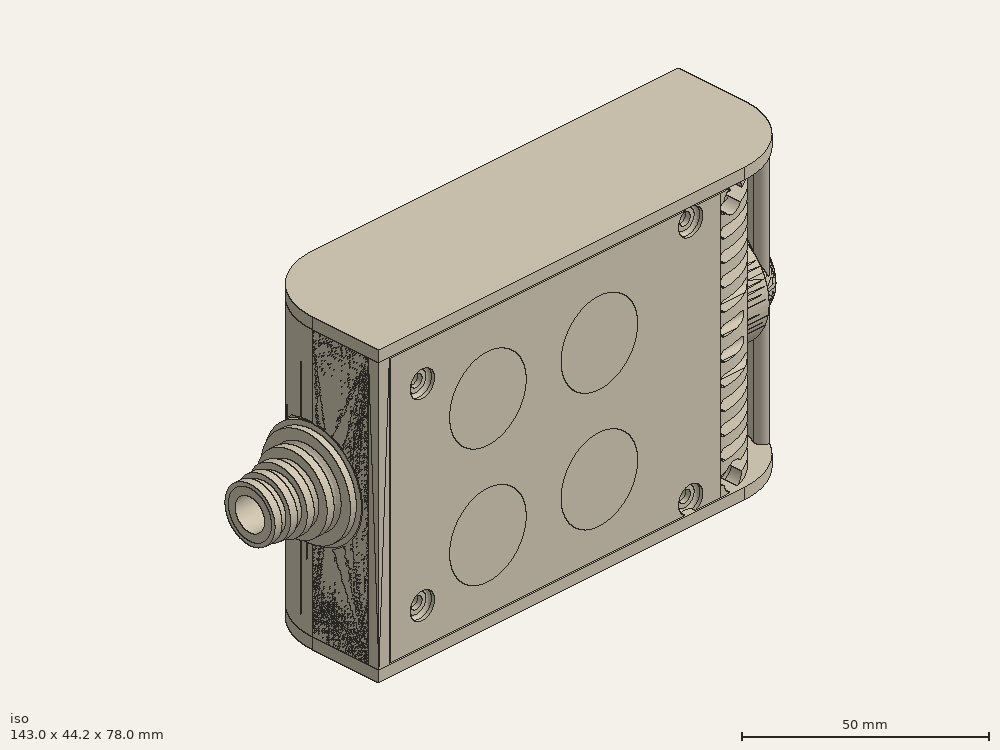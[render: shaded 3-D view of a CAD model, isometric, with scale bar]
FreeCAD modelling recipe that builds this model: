
FCSTD DOCUMENT  (FreeCAD 0.19R0.19.2)
Label: enclosure_134
License: All rights reserved
LicenseURL: http://en.wikipedia.org/wiki/All_rights_reserved
objects: Part::Feature×86, Part::Revolution×86, Part::MultiFuse×65, Sketcher::SketchObject×48, Part::Extrusion×36, Part::Cut×29, Part::Fillet×27, Part::Cylinder×24, Part::Box×17, App::MeasureDistance×4
note: 418 computed .brp shape members not serialized (recipe doc carries the construction recipe); baked Part::Feature solids carry a one-line shape summary decoded from their .brp

FEATURE [Sketcher::SketchObject] Sketch  label="topSketch"
  FullyConstrained = true
  sketch-geometry (20):
    g0: LineSegment StartX=5.21097e-06 StartY=3 StartZ=0 EndX=5.21097e-06 EndY=19 EndZ=0
    g1: ArcOfCircle CenterX=19 CenterY=19 CenterZ=0 NormalX=0 NormalY=0 NormalZ=1 AngleXU=0 Radius=19 StartAngle=1.5708 EndAngle=3.14159
    g2: ArcOfCircle CenterX=19 CenterY=19 CenterZ=0 NormalX=0 NormalY=0 NormalZ=1 AngleXU=0 Radius=16 StartAngle=1.5708 EndAngle=3.14159
    g3: LineSegment StartX=114 StartY=35 StartZ=0 EndX=19 EndY=35 EndZ=0
    g4: LineSegment StartX=5.21097e-06 StartY=3 StartZ=0 EndX=5.21097e-06 EndY=0 EndZ=0
    g5: LineSegment StartX=3 StartY=0 StartZ=0 EndX=5.21097e-06 EndY=0 EndZ=0
    g6: LineSegment StartX=3 StartY=19 StartZ=0 EndX=3 EndY=0 EndZ=0
    g7: LineSegment StartX=19 StartY=38 StartZ=0 EndX=124 EndY=38 EndZ=0
    g8: Circle CenterX=119 CenterY=35 CenterZ=0 NormalX=0 NormalY=0 NormalZ=1 AngleXU=0 Radius=1
    g9: Circle CenterX=121 CenterY=35 CenterZ=0 NormalX=0 NormalY=0 NormalZ=1 AngleXU=0 Radius=1
    g10: Circle CenterX=121 CenterY=33 CenterZ=0 NormalX=0 NormalY=0 NormalZ=1 AngleXU=0 Radius=1
    g11: BSplineCurve PolesCount=3 KnotsCount=2 Degree=2 IsPeriodic=0
    g12: GeomPoint X=119 Y=35 Z=0
    g13: GeomPoint X=121 Y=33 Z=0
    g14: LineSegment StartX=119 StartY=35 StartZ=0 EndX=114 EndY=35 EndZ=0
    g15: ArcOfCircle CenterX=105 CenterY=19 CenterZ=0 NormalX=0 NormalY=0 NormalZ=1 AngleXU=0 Radius=19 StartAngle=5.7297 EndAngle=6.28319
    g16: ArcOfCircle CenterX=105 CenterY=19 CenterZ=0 NormalX=0 NormalY=0 NormalZ=1 AngleXU=0 Radius=16 StartAngle=5.60905 EndAngle=6.28319
    g17: LineSegment StartX=121 StartY=33 StartZ=0 EndX=121 EndY=19 EndZ=0
    g18: LineSegment StartX=124 StartY=38 StartZ=0 EndX=124 EndY=19 EndZ=0
    g19: LineSegment StartX=117.5 StartY=9.01251 StartZ=0 EndX=121.163 EndY=9.0125 EndZ=0
  constraints (46):
    c: Vertical(g0)
    c: Block(g0)
    c: Coincident(g1,g0)
    c: Block(g1)
    c: Coincident(g2,g1)
    c: Block(g2)
    c: Coincident(g3,g2)
    c: Horizontal(g3)
    c: Tangent(g3,g2)
    c: Coincident(g4,g0)
    c: Distance(g4) = 3
    c: Vertical(g4)
    c: Coincident(g5,g4)
    c: Horizontal(g5)
    c: Coincident(g6,g2)
    c: Coincident(g6,g5)
    c: Vertical(g6)
    c: Horizontal(g7)
    c: Distance(g7) = 105
    c: Coincident(g7,g1)
    c: Block(g3)
    c: Weight(g8) = 1
    c: Equal(g8,g9)
    c: Equal(g8,g10)
    c: InternalAlignment(g8,g11)
    c: InternalAlignment(g9,g11)
    c: InternalAlignment(g10,g11)
    c: InternalAlignment(g12,g11)
    c: InternalAlignment(g13,g11)
    c: Block(g11)
    c: Coincident(g14,g11)
    c: Coincident(g14,g3)
    c: Horizontal(g14)
    c: Block(g15)
    c: Coincident(g16,g15)
    c: Block(g16)
    c: Coincident(g17,g11)
    c: Coincident(g17,g16)
    c: Vertical(g17)
    c: Distance(g17) = 14
    c: Coincident(g18,g7)
    c: Coincident(g18,g15)
    c: Vertical(g18)
    c: Distance(g18) = 19
    c: Coincident(g19,g16)
    c: Coincident(g19,g15)
FEATURE [Sketcher::SketchObject] Sketch001  label="bottomSketch"
  FullyConstrained = true
  sketch-geometry (32):
    g0: LineSegment StartX=3.3 StartY=-6.03275e-07 StartZ=0 EndX=98 EndY=-6.03275e-07 EndZ=0
    g1: ArcOfCircle CenterX=98 CenterY=19 CenterZ=0 NormalX=0 NormalY=0 NormalZ=1 AngleXU=0 Radius=19 StartAngle=4.71239 EndAngle=5.71103
    g2: LineSegment StartX=6.3 StartY=8 StartZ=0 EndX=3.3 EndY=8 EndZ=0
    g3: LineSegment StartX=3.3 StartY=8 StartZ=0 EndX=3.3 EndY=-6.03275e-07 EndZ=0
    g4: ArcOfCircle CenterX=8.3 CenterY=5 CenterZ=0 NormalX=0 NormalY=0 NormalZ=1 AngleXU=0 Radius=2 StartAngle=3.14159 EndAngle=4.71239
    g5: LineSegment StartX=6.3 StartY=8 StartZ=0 EndX=6.3 EndY=5 EndZ=0
    g6: ArcOfCircle CenterX=98 CenterY=19 CenterZ=0 NormalX=0 NormalY=0 NormalZ=1 AngleXU=0 Radius=12.7 StartAngle=4.71239 EndAngle=6.28319
    g7: LineSegment StartX=94.7 StartY=3 StartZ=0 EndX=8.3 EndY=3 EndZ=0
    g8-g12: Circle x5 (B-spline internal-alignment scaffolding for g13; pole/knot coordinates omitted)
    g13: BSplineCurve PolesCount=5 KnotsCount=3 Degree=3 IsPeriodic=0
    g14: GeomPoint X=98 Y=6.3 Z=0
    g15: GeomPoint X=96.3938 Y=4.71946 Z=0
    g16: GeomPoint X=94.7 Y=3 Z=0
    g17-g23: Circle x7 (B-spline internal-alignment scaffolding for g24; pole/knot coordinates omitted)
    g24: BSplineCurve PolesCount=7 KnotsCount=5 Degree=3 IsPeriodic=0
    g25-g29: GeomPoint x5 (B-spline internal-alignment scaffolding for g24; pole/knot coordinates omitted)
    g30: ArcOfCircle CenterX=98 CenterY=19 CenterZ=0 NormalX=0 NormalY=0 NormalZ=1 AngleXU=0 Radius=15.7 StartAngle=5.81226 EndAngle=6.28319
    g31: LineSegment StartX=110.7 StartY=19 StartZ=0 EndX=113.7 EndY=19 EndZ=0
  constraints (41):
    c: Horizontal(g0)
    c: Coincident(g1,g0)
    c: Block(g1)
    c: Horizontal(g2)
    c: Distance(g2) = 3
    c: Coincident(g3,g2)
    c: Vertical(g3)
    c: Coincident(g3,g0)
    c: Block(g4)
    c: Block(g2)
    c: Coincident(g5,g2)
    c: Coincident(g5,g4)
    c: Vertical(g5)
    c: Coincident(g6,g1)
    c: Block(g6)
    c: Coincident(g7,g4)
    c: Horizontal(g7)
    c: Block(g0)
    c: Block(g7)
    c: Block(g3)
    c: Coincident(g13,g6)
    c: Weight(g8) = 1
    c: Equal(g8, g9-g12) x4
    c: Coincident(g13,g7)
    c: InternalAlignment(g8-g12 -> g13) x5
    c: InternalAlignment(g14,g13)
    c: InternalAlignment(g15,g13)
    c: InternalAlignment(g16,g13)
    c: Block(g13)
    c: Weight(g17) = 1
    c: Equal(g17, g18-g23) x6
    c: Coincident(g24,g1)
    c: InternalAlignment(g17-g23 -> g24) x7
    c: InternalAlignment(g25-g29 -> g24) x5
    c: Block(g24)
    c: Coincident(g30,g24)
    c: Coincident(g31,g6)
    c: Coincident(g31,g30)
    c: Horizontal(g31)
    c: Block(g31)
    c: Block(g30)
FEATURE [Part::Extrusion] Extrude  label="top"
  Base = -> Sketch
  Dir = (0,0,1)
  DirMode = 2
  FaceMakerClass = Part::FaceMakerBullseye
  LengthFwd = 72
  LengthRev = 0
  Solid = true
  Symmetric = false
FEATURE [Part::Extrusion] Extrude001  label="bottom"
  Base = -> Sketch001
  Dir = (0,0,1)
  DirMode = 2
  FaceMakerClass = Part::FaceMakerBullseye
  LengthFwd = 71.4
  LengthRev = 0
  Placement = pos=(0,0,0.3) rot=(0,0,1;0rad)
  Solid = true
  Symmetric = false
FEATURE [Sketcher::SketchObject] Sketch002  label="topSketch001"
  FullyConstrained = true
  sketch-geometry (6):
    g0: ArcOfCircle CenterX=19 CenterY=19 CenterZ=0 NormalX=0 NormalY=0 NormalZ=1 AngleXU=0 Radius=19 StartAngle=1.5708 EndAngle=3.14159
    g1: LineSegment StartX=5.22862e-06 StartY=19 StartZ=0 EndX=5.22862e-06 EndY=1.19904e-11 EndZ=0
    g2: LineSegment StartX=19 StartY=38 StartZ=0 EndX=124 EndY=38 EndZ=0
    g3: LineSegment StartX=5.22862e-06 StartY=1.19904e-11 StartZ=0 EndX=105 EndY=1.19904e-11 EndZ=0
    g4: ArcOfCircle CenterX=105 CenterY=19 CenterZ=0 NormalX=0 NormalY=0 NormalZ=1 AngleXU=0 Radius=19 StartAngle=4.71239 EndAngle=6.28319
    g5: LineSegment StartX=124 StartY=38 StartZ=0 EndX=124 EndY=19 EndZ=0
  constraints (16):
    c: Block(g0)
    c: Coincident(g1,g0)
    c: Vertical(g1)
    c: Horizontal(g2)
    c: Distance(g2) = 105
    c: Coincident(g2,g0)
    c: Distance(g1) = 19
    c: Coincident(g3,g1)
    c: Horizontal(g3)
    c: Distance(g3) = 105
    c: Block(g4)
    c: Coincident(g4,g3)
    c: Coincident(g5,g2)
    c: Coincident(g5,g4)
    c: Vertical(g5)
    c: Distance(g5) = 19
FEATURE [Part::Extrusion] Extrude002  label="sideA"
  Base = -> Sketch002
  Dir = (0,0,1)
  DirMode = 2
  FaceMakerClass = Part::FaceMakerBullseye
  LengthFwd = 3
  LengthRev = 0
  Placement = pos=(0,0,-3) rot=(0,0,1;0rad)
  Solid = true
  Symmetric = false
FEATURE [Sketcher::SketchObject] Sketch003  label="topSketch002"
  FullyConstrained = true
  sketch-geometry (6):
    g0: LineSegment StartX=19 StartY=38 StartZ=0 EndX=117 EndY=38 EndZ=0
    g1: ArcOfCircle CenterX=19 CenterY=19 CenterZ=0 NormalX=0 NormalY=0 NormalZ=1 AngleXU=0 Radius=19 StartAngle=1.5708 EndAngle=3.14159
    g2: LineSegment StartX=117 StartY=38 StartZ=0 EndX=117 EndY=19 EndZ=0
    g3: LineSegment StartX=98 StartY=1.0161e-12 StartZ=0 EndX=5.22862e-06 EndY=1.0161e-12 EndZ=0
    g4: LineSegment StartX=5.22862e-06 StartY=19 StartZ=0 EndX=5.22862e-06 EndY=1.0161e-12 EndZ=0
    g5: ArcOfCircle CenterX=98 CenterY=19 CenterZ=0 NormalX=0 NormalY=0 NormalZ=1 AngleXU=0 Radius=19 StartAngle=4.71239 EndAngle=6.28319
  constraints (16):
    c: Horizontal(g0)
    c: Distance(g0) = 98
    c: Coincident(g1,g0)
    c: Block(g1)
    c: Coincident(g2,g0)
    c: Vertical(g2)
    c: Distance(g2) = 19
    c: Horizontal(g3)
    c: Coincident(g4,g1)
    c: Vertical(g4)
    c: Coincident(g3,g4)
    c: Block(g3)
    c: Coincident(g5,g2)
    c: Coincident(g5,g3)
    c: Block(g0)
    c: Block(g5)
FEATURE [Sketcher::SketchObject] Sketch004
  FullyConstrained = true
  MapMode = 3
  Placement = pos=(0,0,0) rot=(1,0,0;1.5708rad)
  Support = -> [Extrude]
  sketch-geometry (8):
    g0: Circle CenterX=80.351 CenterY=-67.6202 CenterZ=0 NormalX=0 NormalY=0 NormalZ=1 AngleXU=0 Radius=2
    g1: Circle CenterX=80.351 CenterY=-67.6202 CenterZ=0 NormalX=0 NormalY=0 NormalZ=1 AngleXU=0 Radius=3
    g2: Circle CenterX=80.351 CenterY=-4.92017 CenterZ=0 NormalX=0 NormalY=0 NormalZ=1 AngleXU=0 Radius=2
    g3: Circle CenterX=80.351 CenterY=-4.92017 CenterZ=0 NormalX=0 NormalY=0 NormalZ=1 AngleXU=0 Radius=3
    g4: Circle CenterX=23.851 CenterY=-4.92017 CenterZ=0 NormalX=0 NormalY=0 NormalZ=1 AngleXU=0 Radius=2
    g5: Circle CenterX=23.851 CenterY=-4.92017 CenterZ=0 NormalX=0 NormalY=0 NormalZ=1 AngleXU=0 Radius=3
    g6: Circle CenterX=23.851 CenterY=-67.6202 CenterZ=0 NormalX=0 NormalY=0 NormalZ=1 AngleXU=0 Radius=2
    g7: Circle CenterX=23.851 CenterY=-67.6202 CenterZ=0 NormalX=0 NormalY=0 NormalZ=1 AngleXU=0 Radius=3
  constraints (8):
    c: Block(g3)
    c: Block(g2)
    c: Block(g1)
    c: Block(g0)
    c: Block(g6)
    c: Block(g7)
    c: Block(g4)
    c: Block(g5)
FEATURE [Part::Extrusion] Extrude004
  Base = -> Sketch004
  Dir = (0,-1,2e-16)
  DirMode = 2
  FaceMakerClass = Part::FaceMakerBullseye
  LengthFwd = 6
  LengthRev = 0
  Placement = pos=(0,9,0) rot=(0,0,1;0rad)
  Solid = true
  Symmetric = false
FEATURE [Sketcher::SketchObject] Sketch005
  FullyConstrained = true
  MapMode = 3
  Placement = pos=(0,0,0) rot=(1,0,0;1.5708rad)
  Support = -> [Extrude]
  sketch-geometry (8):
    g0: Circle CenterX=80.351 CenterY=-67.6202 CenterZ=0 NormalX=0 NormalY=0 NormalZ=1 AngleXU=0 Radius=3
    g1: Circle CenterX=80.351 CenterY=-4.92017 CenterZ=0 NormalX=0 NormalY=0 NormalZ=1 AngleXU=0 Radius=3
    g2: Circle CenterX=23.851 CenterY=-4.92017 CenterZ=0 NormalX=0 NormalY=0 NormalZ=1 AngleXU=0 Radius=3
    g3: Circle CenterX=23.851 CenterY=-67.6202 CenterZ=0 NormalX=0 NormalY=0 NormalZ=1 AngleXU=0 Radius=3
    g4: Circle CenterX=23.851 CenterY=-67.6202 CenterZ=0 NormalX=0 NormalY=0 NormalZ=1 AngleXU=0 Radius=5
    g5: Circle CenterX=80.351 CenterY=-67.6202 CenterZ=0 NormalX=0 NormalY=0 NormalZ=1 AngleXU=0 Radius=5
    g6: Circle CenterX=23.851 CenterY=-4.92017 CenterZ=0 NormalX=0 NormalY=0 NormalZ=1 AngleXU=0 Radius=5
    g7: Circle CenterX=80.351 CenterY=-4.92017 CenterZ=0 NormalX=0 NormalY=0 NormalZ=1 AngleXU=0 Radius=5
  constraints (8):
    c: Block(g1)
    c: Block(g0)
    c: Block(g3)
    c: Block(g2)
    c: Block(g5)
    c: Block(g4)
    c: Block(g6)
    c: Block(g7)
FEATURE [Part::Extrusion] Extrude005
  Base = -> Sketch005
  Dir = (0,-1,2e-16)
  DirMode = 2
  FaceMakerClass = Part::FaceMakerBullseye
  LengthFwd = 2
  LengthRev = 0
  Solid = true
  Symmetric = false
FEATURE [Sketcher::SketchObject] Sketch006
  FullyConstrained = true
  MapMode = 3
  Placement = pos=(0,0,0) rot=(1,0,0;1.5708rad)
  sketch-geometry (8):
    g0: Circle CenterX=80.351 CenterY=-67.6202 CenterZ=0 NormalX=0 NormalY=0 NormalZ=1 AngleXU=0 Radius=3
    g1: Circle CenterX=80.351 CenterY=-4.92017 CenterZ=0 NormalX=0 NormalY=0 NormalZ=1 AngleXU=0 Radius=3
    g2: Circle CenterX=23.851 CenterY=-4.92017 CenterZ=0 NormalX=0 NormalY=0 NormalZ=1 AngleXU=0 Radius=3
    g3: Circle CenterX=23.851 CenterY=-67.6202 CenterZ=0 NormalX=0 NormalY=0 NormalZ=1 AngleXU=0 Radius=3
    g4: Circle CenterX=23.851 CenterY=-67.6202 CenterZ=0 NormalX=0 NormalY=0 NormalZ=1 AngleXU=0 Radius=5
    g5: Circle CenterX=80.351 CenterY=-67.6202 CenterZ=0 NormalX=0 NormalY=0 NormalZ=1 AngleXU=0 Radius=5
    g6: Circle CenterX=23.851 CenterY=-4.92017 CenterZ=0 NormalX=0 NormalY=0 NormalZ=1 AngleXU=0 Radius=5
    g7: Circle CenterX=80.351 CenterY=-4.92017 CenterZ=0 NormalX=0 NormalY=0 NormalZ=1 AngleXU=0 Radius=5
  constraints (8):
    c: Block(g1)
    c: Block(g0)
    c: Block(g3)
    c: Block(g2)
    c: Block(g5)
    c: Block(g4)
    c: Block(g6)
    c: Block(g7)
FEATURE [Part::Extrusion] Extrude007
  Base = -> Sketch006
  Dir = (0,-1,2e-16)
  DirMode = 2
  FaceMakerClass = Part::FaceMakerBullseye
  LengthFwd = 2
  LengthRev = 0
  Solid = true
  Symmetric = false
FEATURE [Part::Fillet] Fillet
  Base = -> Extrude007
  Edges = 4 edges r=1.99: [Edge6,Edge12,Edge18,Edge24]
FEATURE [Part::Cut] Cut
  Base = -> Extrude005
  Placement = pos=(0,5,0) rot=(0,0,1;0rad)
  Tool = -> Fillet
FEATURE [Part::MultiFuse] Fusion  label="pCBScrews"
  Placement = pos=(-2.5,0,72.3) rot=(0,0,1;0rad)
  Shapes = -> [Extrude004,Cut]
FEATURE [App::MeasureDistance] Distance  label="Distance: 0.69 mm"
  Distance = 0.685967
  P1 = (24.0138,2.9647,0.3)
  P2 = (23.8901,3,-0.373787)
FEATURE [App::MeasureDistance] Distance001  label="Distance: 0.53 mm"
  Distance = 0.533607
  P1 = (80.2939,3,72.2334)
  P2 = (80.281,2.99661,71.7)
FEATURE [Part::Fillet] Fillet001
  Base = -> Extrude001
  Edges = 1 edges r=2.4: [Edge17]
FEATURE [Part::Fillet] Fillet002  label="bottom001"
  Base = -> Fillet001
  Edges = 1 edges r=2.4: [Edge36]
FEATURE [Part::Fillet] Fillet003  label="top001"
  Base = -> Extrude
  Edges = 1 edges r=2: [Edge1]
FEATURE [Sketcher::SketchObject] Sketch007
  FullyConstrained = true
  sketch-geometry (16):
    g0: LineSegment StartX=4 StartY=0 StartZ=0 EndX=4 EndY=2.4 EndZ=0
    g1: LineSegment StartX=4 StartY=2.4 StartZ=0 EndX=7 EndY=2.4 EndZ=0
    g2: LineSegment StartX=4 StartY=0 StartZ=0 EndX=5.7 EndY=0 EndZ=0
    g3: LineSegment StartX=5.7 StartY=0 StartZ=0 EndX=5.7 EndY=-5.6 EndZ=0
    g4-g8: Circle x5 (B-spline internal-alignment scaffolding for g9; pole/knot coordinates omitted)
    g9: BSplineCurve PolesCount=5 KnotsCount=3 Degree=3 IsPeriodic=0
    g10: GeomPoint X=7 Y=2.4 Z=0
    g11: GeomPoint X=10.4582 Y=-1.55472 Z=0
    g12: GeomPoint X=14 Y=-5.6 Z=0
    g13: LineSegment StartX=14 StartY=-5.6 StartZ=0 EndX=14 EndY=-14.1 EndZ=0
    g14: LineSegment StartX=14 StartY=-14.1 StartZ=0 EndX=6.5 EndY=-14.1 EndZ=0
    g15: LineSegment StartX=5.7 StartY=-5.6 StartZ=0 EndX=6.5 EndY=-14.1 EndZ=0
  constraints (28):
    c: Distance(g0) = 2.4
    c: Vertical(g0)
    c: Block(g0)
    c: Coincident(g1,g0)
    c: Horizontal(g1)
    c: Distance(g1) = 3
    c: Coincident(g2,g0)
    c: Horizontal(g2)
    c: Distance(g2) = 1.7
    c: Coincident(g3,g2)
    c: Vertical(g3)
    c: Distance(g3) = 5.6
    c: Coincident(g9,g1)
    c: Weight(g4) = 1
    c: Equal(g4, g5-g8) x4
    c: InternalAlignment(g4-g8 -> g9) x5
    c: InternalAlignment(g10,g9)
    c: InternalAlignment(g11,g9)
    c: InternalAlignment(g12,g9)
    c: Block(g9)
    c: Coincident(g13,g9)
    c: Vertical(g13)
    c: Distance(g13) = 8.5
    c: Coincident(g14,g13)
    c: Horizontal(g14)
    c: Distance(g14) = 7.5
    c: Coincident(g15,g3)
    c: Coincident(g15,g14)
FEATURE [Part::Feature] Face
  shape: bbox 10 x 16.5 x 2e-07 mm, 1 faces, 0 solids (baked)
FEATURE [Part::Revolution] Revolve  label="plugHousing"
  Angle = 360
  Axis = (0,1,0)
  Base = (0,0,0)
  FaceMakerClass = Part::FaceMakerBullseye
  Placement = pos=(0,0,36.15) rot=(0,0,1;0rad)
  Solid = false
  Source = -> Face
  Symmetric = false
FEATURE [Part::Feature] Face001
  shape: bbox 10 x 16.5 x 2e-07 mm, 1 faces, 0 solids (baked)
FEATURE [Part::Revolution] Revolve001  label="plugHousing001"
  Angle = 360
  Axis = (0,1,0)
  Base = (0,0,0)
  FaceMakerClass = Part::FaceMakerBullseye
  Placement = pos=(0,0,36.15) rot=(0,0,1;0rad)
  Solid = false
  Source = -> Face001
  Symmetric = false
FEATURE [Part::MultiFuse] Fusion001  label="plugHousing002"
  Placement = pos=(0,0,0) rot=(0,0,1;1.5708rad)
  Shapes = -> [Revolve001,Revolve]
FEATURE [Part::Feature] Face002
  shape: bbox 10 x 16.5 x 2e-07 mm, 1 faces, 0 solids (baked)
FEATURE [Part::Revolution] Revolve003  label="plugHousing005"
  Angle = 360
  Axis = (0,1,0)
  Base = (0,0,0)
  FaceMakerClass = Part::FaceMakerBullseye
  Placement = pos=(0,0,36.15) rot=(0,0,1;0rad)
  Solid = false
  Source = -> Face002
  Symmetric = false
FEATURE [Part::Feature] Face003
  shape: bbox 10 x 16.5 x 2e-07 mm, 1 faces, 0 solids (baked)
FEATURE [Part::Revolution] Revolve002  label="plugHousing003"
  Angle = 360
  Axis = (0,1,0)
  Base = (0,0,0)
  FaceMakerClass = Part::FaceMakerBullseye
  Placement = pos=(0,0,36.15) rot=(0,0,1;0rad)
  Solid = false
  Source = -> Face003
  Symmetric = false
FEATURE [Part::MultiFuse] Fusion002  label="plugHousing004"
  Placement = pos=(0,0,0) rot=(0,0,1;1.5708rad)
  Shapes = -> [Revolve002,Revolve003]
FEATURE [Part::MultiFuse] Fusion003  label="plugHousing006"
  Placement = pos=(0,19,0) rot=(0,0,1;3.14159rad)
  Shapes = -> [Fusion002,Fusion001]
FEATURE [Part::Feature] Face004
  shape: bbox 10 x 16.5 x 2e-07 mm, 1 faces, 0 solids (baked)
FEATURE [Part::Revolution] Revolve006  label="plugHousing010"
  Angle = 360
  Axis = (0,1,0)
  Base = (0,0,0)
  FaceMakerClass = Part::FaceMakerBullseye
  Placement = pos=(0,0,36.15) rot=(0,0,1;0rad)
  Solid = false
  Source = -> Face004
  Symmetric = false
FEATURE [Part::Feature] Face005
  shape: bbox 10 x 16.5 x 2e-07 mm, 1 faces, 0 solids (baked)
FEATURE [Part::Revolution] Revolve007  label="plugHousing011"
  Angle = 360
  Axis = (0,1,0)
  Base = (0,0,0)
  FaceMakerClass = Part::FaceMakerBullseye
  Placement = pos=(0,0,36.15) rot=(0,0,1;0rad)
  Solid = false
  Source = -> Face005
  Symmetric = false
FEATURE [Part::Feature] Face006
  shape: bbox 10 x 16.5 x 2e-07 mm, 1 faces, 0 solids (baked)
FEATURE [Part::Revolution] Revolve004  label="plugHousing007"
  Angle = 360
  Axis = (0,1,0)
  Base = (0,0,0)
  FaceMakerClass = Part::FaceMakerBullseye
  Placement = pos=(0,0,36.15) rot=(0,0,1;0rad)
  Solid = false
  Source = -> Face006
  Symmetric = false
FEATURE [Part::MultiFuse] Fusion004  label="plugHousing009"
  Placement = pos=(0,0,0) rot=(0,0,1;1.5708rad)
  Shapes = -> [Revolve004,Revolve007]
FEATURE [Part::Feature] Face007
  shape: bbox 10 x 16.5 x 2e-07 mm, 1 faces, 0 solids (baked)
FEATURE [Part::Revolution] Revolve005  label="plugHousing008"
  Angle = 360
  Axis = (0,1,0)
  Base = (0,0,0)
  FaceMakerClass = Part::FaceMakerBullseye
  Placement = pos=(0,0,36.15) rot=(0,0,1;0rad)
  Solid = false
  Source = -> Face007
  Symmetric = false
FEATURE [Part::MultiFuse] Fusion005  label="plugHousing012"
  Placement = pos=(0,0,0) rot=(0,0,1;1.5708rad)
  Shapes = -> [Revolve006,Revolve005]
FEATURE [Part::MultiFuse] Fusion006  label="plugHousing013"
  Placement = pos=(0,19,0) rot=(0,0,1;3.14159rad)
  Shapes = -> [Fusion005,Fusion004]
FEATURE [Part::MultiFuse] Fusion007  label="plugHousing014"
  Placement = pos=(122.621,0,-0.15) rot=(0,0,1;0rad)
  Shapes = -> [Fusion003,Fusion006]
FEATURE [Part::Cylinder] Cylinder002
  Angle = 360
  AttacherType = Attacher::AttachEngine3D
  Height = 20
  Placement = pos=(0,0,36.15) rot=(0,0,1;0rad)
  Radius = 4
FEATURE [Part::Cylinder] Cylinder003
  Angle = 360
  AttacherType = Attacher::AttachEngine3D
  Height = 10
  Placement = pos=(0,0,36.15) rot=(0,0,1;0rad)
  Radius = 4
FEATURE [Part::MultiFuse] Fusion009  label="removeToCreateHoleForPlugHousing"
  Placement = pos=(70,19,36.15) rot=(0,1,0;1.5708rad)
  Shapes = -> [Cylinder002,Cylinder003]
FEATURE [Part::Cylinder] Cylinder004
  Angle = 360
  AttacherType = Attacher::AttachEngine3D
  Height = 20
  Placement = pos=(0,0,36.15) rot=(0,0,1;0rad)
  Radius = 4
FEATURE [Part::Cylinder] Cylinder005
  Angle = 360
  AttacherType = Attacher::AttachEngine3D
  Height = 10
  Placement = pos=(0,0,36.15) rot=(0,0,1;0rad)
  Radius = 4
FEATURE [Part::MultiFuse] Fusion010  label="removeToCreateHoleForPlugHousing001"
  Placement = pos=(70,19,36.15) rot=(0,1,0;1.5708rad)
  Shapes = -> [Cylinder004,Cylinder005]
FEATURE [Part::Cut] Cut001
  Base = -> Fillet003
  Tool = -> Fusion010
FEATURE [Part::Cut] Cut002  label="Bottom"
  Base = -> Fillet002
  Tool = -> Fusion009
FEATURE [Part::Feature] Face008
  shape: bbox 10 x 16.5 x 2e-07 mm, 1 faces, 0 solids (baked)
FEATURE [Part::Revolution] Revolve011  label="plugHousing021"
  Angle = 360
  Axis = (0,1,0)
  Base = (0,0,0)
  FaceMakerClass = Part::FaceMakerBullseye
  Placement = pos=(0,0,36.15) rot=(0,0,1;0rad)
  Solid = false
  Source = -> Face008
  Symmetric = false
FEATURE [Part::Feature] Face009
  shape: bbox 10 x 16.5 x 2e-07 mm, 1 faces, 0 solids (baked)
FEATURE [Part::Revolution] Revolve012  label="plugHousing022"
  Angle = 360
  Axis = (0,1,0)
  Base = (0,0,0)
  FaceMakerClass = Part::FaceMakerBullseye
  Placement = pos=(0,0,36.15) rot=(0,0,1;0rad)
  Solid = false
  Source = -> Face009
  Symmetric = false
FEATURE [Part::Feature] Face010 .. Face013  x4 (patterned run collapsed; names and placements below)
  shape: bbox 10 x 16.5 x 2e-07 mm, 1 faces, 0 solids (baked)
FEATURE [Part::Revolution] Revolve015  label="plugHousing027"
  Angle = 360
  Axis = (0,1,0)
  Base = (0,0,0)
  FaceMakerClass = Part::FaceMakerBullseye
  Placement = pos=(0,0,36.15) rot=(0,0,1;0rad)
  Solid = false
  Source = -> Face013
  Symmetric = false
FEATURE [Part::Feature] Face014
  shape: bbox 10 x 16.5 x 2e-07 mm, 1 faces, 0 solids (baked)
FEATURE [Part::Feature] Face015
  shape: bbox 10 x 16.5 x 2e-07 mm, 1 faces, 0 solids (baked)
FEATURE [Part::Feature] Face016
  shape: bbox 10 x 16.5 x 2e-07 mm, 1 faces, 0 solids (baked)
FEATURE [Part::Revolution] Revolve019  label="plugHousing033"
  Angle = 360
  Axis = (0,1,0)
  Base = (0,0,0)
  FaceMakerClass = Part::FaceMakerBullseye
  Placement = pos=(0,0,36.15) rot=(0,0,1;0rad)
  Solid = false
  Source = -> Face016
  Symmetric = false
FEATURE [Part::Feature] Face017
  shape: bbox 10 x 16.5 x 2e-07 mm, 1 faces, 0 solids (baked)
FEATURE [Part::Revolution] Revolve020  label="plugHousing034"
  Angle = 360
  Axis = (0,1,0)
  Base = (0,0,0)
  FaceMakerClass = Part::FaceMakerBullseye
  Placement = pos=(0,0,36.15) rot=(0,0,1;0rad)
  Solid = false
  Source = -> Face017
  Symmetric = false
FEATURE [Part::Feature] Face018
  shape: bbox 10 x 16.5 x 2e-07 mm, 1 faces, 0 solids (baked)
FEATURE [Part::Revolution] Revolve016  label="plugHousing030"
  Angle = 360
  Axis = (0,1,0)
  Base = (0,0,0)
  FaceMakerClass = Part::FaceMakerBullseye
  Placement = pos=(0,0,36.15) rot=(0,0,1;0rad)
  Solid = false
  Source = -> Face018
  Symmetric = false
FEATURE [Part::MultiFuse] Fusion020  label="plugHousing038"
  Placement = pos=(0,0,0) rot=(0,0,1;1.5708rad)
  Shapes = -> [Revolve016,Revolve020]
FEATURE [Part::Feature] Face019
  shape: bbox 10 x 16.5 x 2e-07 mm, 1 faces, 0 solids (baked)
FEATURE [Part::Feature] Face020
  shape: bbox 10 x 16.5 x 2e-07 mm, 1 faces, 0 solids (baked)
FEATURE [Part::Revolution] Revolve017  label="plugHousing031"
  Angle = 360
  Axis = (0,1,0)
  Base = (0,0,0)
  FaceMakerClass = Part::FaceMakerBullseye
  Placement = pos=(0,0,36.15) rot=(0,0,1;0rad)
  Solid = false
  Source = -> Face020
  Symmetric = false
FEATURE [Part::MultiFuse] Fusion021  label="plugHousing039"
  Placement = pos=(0,0,0) rot=(0,0,1;1.5708rad)
  Shapes = -> [Revolve019,Revolve017]
FEATURE [Part::MultiFuse] Fusion023  label="plugHousing041"
  Placement = pos=(0,19,0) rot=(0,0,1;3.14159rad)
  Shapes = -> [Fusion021,Fusion020]
FEATURE [Part::Revolution] Revolve022  label="plugHousing043"
  Angle = 360
  Axis = (0,1,0)
  Base = (0,0,0)
  FaceMakerClass = Part::FaceMakerBullseye
  Placement = pos=(0,0,36.15) rot=(0,0,1;0rad)
  Solid = false
  Source = -> Face019
  Symmetric = false
FEATURE [Part::Feature] Face021
  shape: bbox 10 x 16.5 x 2e-07 mm, 1 faces, 0 solids (baked)
FEATURE [Part::Revolution] Revolve023  label="plugHousing044"
  Angle = 360
  Axis = (0,1,0)
  Base = (0,0,0)
  FaceMakerClass = Part::FaceMakerBullseye
  Placement = pos=(0,0,36.15) rot=(0,0,1;0rad)
  Solid = false
  Source = -> Face021
  Symmetric = false
FEATURE [Part::Feature] Face022
  shape: bbox 10 x 16.5 x 2e-07 mm, 1 faces, 0 solids (baked)
FEATURE [Part::Revolution] Revolve018  label="plugHousing032"
  Angle = 360
  Axis = (0,1,0)
  Base = (0,0,0)
  FaceMakerClass = Part::FaceMakerBullseye
  Placement = pos=(0,0,36.15) rot=(0,0,1;0rad)
  Solid = false
  Source = -> Face022
  Symmetric = false
FEATURE [Part::MultiFuse] Fusion022  label="plugHousing040"
  Placement = pos=(0,0,0) rot=(0,0,1;1.5708rad)
  Shapes = -> [Revolve018,Revolve023]
FEATURE [Part::Feature] Face023
  shape: bbox 10 x 16.5 x 2e-07 mm, 1 faces, 0 solids (baked)
FEATURE [Part::Revolution] Revolve021  label="plugHousing035"
  Angle = 360
  Axis = (0,1,0)
  Base = (0,0,0)
  FaceMakerClass = Part::FaceMakerBullseye
  Placement = pos=(0,0,36.15) rot=(0,0,1;0rad)
  Solid = false
  Source = -> Face023
  Symmetric = false
FEATURE [Part::MultiFuse] Fusion018  label="plugHousing036"
  Placement = pos=(0,0,0) rot=(0,0,1;1.5708rad)
  Shapes = -> [Revolve022,Revolve021]
FEATURE [Part::MultiFuse] Fusion019  label="plugHousing037"
  Placement = pos=(0,19,0) rot=(0,0,1;3.14159rad)
  Shapes = -> [Fusion018,Fusion022]
FEATURE [Part::MultiFuse] Fusion024  label="plugHousing042"
  Placement = pos=(122.621,0,-0.15) rot=(0,0,1;0rad)
  Shapes = -> [Fusion023,Fusion019]
FEATURE [Part::Cylinder] Cylinder006
  Angle = 360
  AttacherType = Attacher::AttachEngine3D
  Height = 20
  Placement = pos=(0,0,36.15) rot=(0,0,1;0rad)
  Radius = 14.3
FEATURE [Part::Cylinder] Cylinder007
  Angle = 360
  AttacherType = Attacher::AttachEngine3D
  Height = 10
  Placement = pos=(0,0,36.15) rot=(0,0,1;0rad)
  Radius = 4
FEATURE [Part::MultiFuse] Fusion026  label="removeToCreteHoleForPlugHousing"
  Placement = pos=(70,19,36) rot=(0,1,0;1.5708rad)
  Shapes = -> [Cylinder006,Cylinder007]
FEATURE [Part::Box] Box001  label="Cube001"
  AttacherType = Attacher::AttachEngine3D
  Height = 28
  Length = 3
  Placement = pos=(110.7,19,22) rot=(0,0,1;0rad)
  Width = 15.7
FEATURE [Part::Cut] Cut003  label="top002"
  Base = -> Cut001
  Tool = -> Fusion007
FEATURE [Part::Revolution] Revolve008  label="plugHousing015"
  Angle = 360
  Axis = (0,1,0)
  Base = (0,0,0)
  FaceMakerClass = Part::FaceMakerBullseye
  Placement = pos=(0,0,36.15) rot=(0,0,1;0rad)
  Solid = false
  Source = -> Face010
  Symmetric = false
FEATURE [Part::MultiFuse] Fusion013  label="plugHousing020"
  Placement = pos=(0,0,0) rot=(0,0,1;1.5708rad)
  Shapes = -> [Revolve008,Revolve012]
FEATURE [Part::Cut] Cut004  label="top003"
  Base = -> Cut003
  Placement = pos=(1,0,0) rot=(0,0,1;0rad)
  Tool = -> Fusion026
FEATURE [Part::Cylinder] Cylinder008
  Angle = 360
  AttacherType = Attacher::AttachEngine3D
  Height = 20
  Placement = pos=(0,0,36.15) rot=(0,0,1;0rad)
  Radius = 10.3
FEATURE [Part::Cylinder] Cylinder009
  Angle = 360
  AttacherType = Attacher::AttachEngine3D
  Height = 10
  Placement = pos=(0,0,36.15) rot=(0,0,1;0rad)
  Radius = 4
FEATURE [Part::MultiFuse] Fusion027  label="removeToCreteHoleForPlugHousing001"
  Placement = pos=(70,19,36) rot=(0,1,0;1.5708rad)
  Shapes = -> [Cylinder008,Cylinder009]
FEATURE [Part::Cut] Cut005  label="plugHousingTab"
  Base = -> Box001
  Tool = -> Fusion027
FEATURE [Part::MultiFuse] Fusion028  label="plugHousing045"
  Shapes = -> [Fusion024,Cut005]
FEATURE [Part::Box] Box002  label="Cube002"
  AttacherType = Attacher::AttachEngine3D
  Height = 28.8
  Length = 3
  Placement = pos=(107.3,28,21.6) rot=(0,0,1;0rad)
  Width = 7
FEATURE [Part::Box] Box003  label="Cube003"
  AttacherType = Attacher::AttachEngine3D
  Height = 3
  Length = 6.4
  Placement = pos=(107.3,28,18.6) rot=(0,0,1;0rad)
  Width = 7
FEATURE [Part::Box] Box004  label="Cube004"
  AttacherType = Attacher::AttachEngine3D
  Height = 3
  Length = 6.4
  Placement = pos=(107.3,28,50.4) rot=(0,0,1;0rad)
  Width = 7
FEATURE [Part::MultiFuse] Fusion029  label="plugHousingBracketHolder"
  Shapes = -> [Box004,Box002,Box003]
FEATURE [Part::Cylinder] Cylinder010
  Angle = 360
  AttacherType = Attacher::AttachEngine3D
  Height = 20
  Placement = pos=(0,0,36.15) rot=(0,0,1;0rad)
  Radius = 14.3
FEATURE [Part::Cylinder] Cylinder011
  Angle = 360
  AttacherType = Attacher::AttachEngine3D
  Height = 10
  Placement = pos=(0,0,36.15) rot=(0,0,1;0rad)
  Radius = 4
FEATURE [Part::MultiFuse] Fusion030  label="removeToCreteHoleForPlugHousing002"
  Placement = pos=(70,19,36) rot=(0,1,0;1.5708rad)
  Shapes = -> [Cylinder010,Cylinder011]
FEATURE [Part::Cut] Cut006  label="plugHousingBracketHolder001"
  Base = -> Fusion029
  Tool = -> Fusion030
FEATURE [Part::Cylinder] Cylinder012
  Angle = 360
  AttacherType = Attacher::AttachEngine3D
  Height = 20
  Placement = pos=(0,0,36.15) rot=(0,0,1;0rad)
  Radius = 7
FEATURE [Part::Cylinder] Cylinder013
  Angle = 360
  AttacherType = Attacher::AttachEngine3D
  Height = 10
  Placement = pos=(0,0,36.15) rot=(0,0,1;0rad)
  Radius = 4
FEATURE [Part::MultiFuse] Fusion032  label="removeToCreteHoleForPlugHousing003"
  Placement = pos=(70,19,36) rot=(0,1,0;1.5708rad)
  Shapes = -> [Cylinder012,Cylinder013]
FEATURE [Part::Cut] Cut007  label="bottom002"
  Base = -> Cut002
  Tool = -> Fusion032
FEATURE [Sketcher::SketchObject] Sketch008
  FullyConstrained = true
  sketch-geometry (54):
    g0: LineSegment StartX=-4.2 StartY=0 StartZ=0 EndX=-6.2 EndY=0 EndZ=0
    g1: LineSegment StartX=-14 StartY=-18 StartZ=0 EndX=-14 EndY=-26.5 EndZ=0
    g2: LineSegment StartX=-4.2 StartY=0 StartZ=0 EndX=-4.2 EndY=-13.4877 EndZ=0
    g3: Circle CenterX=-4.2 CenterY=-13.4877 CenterZ=0 NormalX=0 NormalY=0 NormalZ=1 AngleXU=0 Radius=1
    g4: Circle CenterX=-4.2 CenterY=-26.5 CenterZ=0 NormalX=0 NormalY=0 NormalZ=1 AngleXU=0 Radius=1
    g5: Circle CenterX=-8.2 CenterY=-26.5 CenterZ=0 NormalX=0 NormalY=0 NormalZ=1 AngleXU=0 Radius=1
    g6: BSplineCurve PolesCount=3 KnotsCount=2 Degree=2 IsPeriodic=0
    g7: GeomPoint X=-4.2 Y=-13.4877 Z=0
    g8: GeomPoint X=-8.2 Y=-26.5 Z=0
    g9: LineSegment StartX=-14 StartY=-26.5 StartZ=0 EndX=-8.2 EndY=-26.5 EndZ=0
    g10: LineSegment StartX=-10.15 StartY=-12 StartZ=0 EndX=-10.15 EndY=-14 EndZ=0
    g11: LineSegment StartX=-12.8401 StartY=-16 StartZ=0 EndX=-10.1571 EndY=-16 EndZ=0
    g12: LineSegment StartX=-10.15 StartY=-14 StartZ=0 EndX=-8.70761 EndY=-14 EndZ=0
    g13: LineSegment StartX=-12.8401 StartY=-16 StartZ=0 EndX=-12.8401 EndY=-17.6958 EndZ=0
    g14: LineSegment StartX=-10.15 StartY=-12 StartZ=0 EndX=-7.79258 EndY=-12 EndZ=0
    g15: Circle CenterX=-6.2215 CenterY=-2 CenterZ=0 NormalX=0 NormalY=0 NormalZ=1 AngleXU=0 Radius=1
    g16: Circle CenterX=-6.22762 CenterY=-2.58724 CenterZ=0 NormalX=0 NormalY=0 NormalZ=1 AngleXU=0 Radius=1
    g17: Circle CenterX=-6.32538 CenterY=-4 CenterZ=0 NormalX=0 NormalY=0 NormalZ=1 AngleXU=0 Radius=1
    g18: BSplineCurve PolesCount=3 KnotsCount=2 Degree=2 IsPeriodic=0
    g19: GeomPoint X=-6.2215 Y=-2 Z=0
    g20: GeomPoint X=-6.32538 Y=-4 Z=0
    g21: Circle CenterX=-6.48644 CenterY=-5.99526 CenterZ=0 NormalX=0 NormalY=0 NormalZ=1 AngleXU=0 Radius=1
    g22: Circle CenterX=-6.58486 CenterY=-6.99526 CenterZ=0 NormalX=0 NormalY=0 NormalZ=1 AngleXU=0 Radius=1
    g23: Circle CenterX=-6.77343 CenterY=-8 CenterZ=0 NormalX=0 NormalY=0 NormalZ=1 AngleXU=0 Radius=1
    g24: BSplineCurve PolesCount=3 KnotsCount=2 Degree=2 IsPeriodic=0
    g25: GeomPoint X=-6.48644 Y=-5.99526 Z=0
    g26: GeomPoint X=-6.77343 Y=-8 Z=0
    g27: Circle CenterX=-7.19003 CenterY=-10 CenterZ=0 NormalX=0 NormalY=0 NormalZ=1 AngleXU=0 Radius=1
    g28: Circle CenterX=-7.44407 CenterY=-11.0915 CenterZ=0 NormalX=0 NormalY=0 NormalZ=1 AngleXU=0 Radius=1
    g29: Circle CenterX=-7.79258 CenterY=-12 CenterZ=0 NormalX=0 NormalY=0 NormalZ=1 AngleXU=0 Radius=1
    g30: BSplineCurve PolesCount=3 KnotsCount=2 Degree=2 IsPeriodic=0
    g31: GeomPoint X=-7.19003 Y=-10 Z=0
    g32: GeomPoint X=-7.79258 Y=-12 Z=0
    g33: Circle CenterX=-8.70761 CenterY=-14 CenterZ=0 NormalX=0 NormalY=0 NormalZ=1 AngleXU=0 Radius=1
    g34: Circle CenterX=-9.33087 CenterY=-15.1837 CenterZ=0 NormalX=0 NormalY=0 NormalZ=1 AngleXU=0 Radius=1
    g35: Circle CenterX=-10.1571 CenterY=-16 CenterZ=0 NormalX=0 NormalY=0 NormalZ=1 AngleXU=0 Radius=1
    g36: BSplineCurve PolesCount=3 KnotsCount=2 Degree=2 IsPeriodic=0
    g37: GeomPoint X=-8.70761 Y=-14 Z=0
    g38: GeomPoint X=-10.1571 Y=-16 Z=0
    g39: Circle CenterX=-12.8401 CenterY=-17.6958 CenterZ=0 NormalX=0 NormalY=0 NormalZ=1 AngleXU=0 Radius=1
    g40: Circle CenterX=-13.3521 CenterY=-17.9027 CenterZ=0 NormalX=0 NormalY=0 NormalZ=1 AngleXU=0 Radius=1
    g41: Circle CenterX=-14 CenterY=-18 CenterZ=0 NormalX=0 NormalY=0 NormalZ=1 AngleXU=0 Radius=1
    g42: BSplineCurve PolesCount=3 KnotsCount=2 Degree=2 IsPeriodic=0
    g43: GeomPoint X=-12.8401 Y=-17.6958 Z=0
    g44: GeomPoint X=-14 Y=-18 Z=0
    g45: LineSegment StartX=-6.2 StartY=0 StartZ=0 EndX=-7.2 EndY=0 EndZ=0
    g46: LineSegment StartX=-7.2 StartY=0 StartZ=0 EndX=-7.2 EndY=-2 EndZ=0
    g47: LineSegment StartX=-7.2 StartY=-2 StartZ=0 EndX=-6.2215 EndY=-2 EndZ=0
    g48: LineSegment StartX=-6.32538 StartY=-4 StartZ=0 EndX=-7.65538 EndY=-4 EndZ=0
    g49: LineSegment StartX=-7.65538 StartY=-4 StartZ=0 EndX=-7.65538 EndY=-5.99526 EndZ=0
    g50: LineSegment StartX=-7.65538 StartY=-5.99526 StartZ=0 EndX=-6.48644 EndY=-5.99526 EndZ=0
    g51: LineSegment StartX=-6.77343 StartY=-8 StartZ=0 EndX=-8.43343 EndY=-8 EndZ=0
    g52: LineSegment StartX=-8.43343 StartY=-8 StartZ=0 EndX=-8.43343 EndY=-10 EndZ=0
    g53: LineSegment StartX=-8.43343 StartY=-10 StartZ=0 EndX=-7.19003 EndY=-10 EndZ=0
  constraints (112):
    c: Horizontal(g0)
    c: Distance(g0) = 2
    c: Block(g0)
    c: Vertical(g1)
    c: Coincident(g2,g0)
    c: Vertical(g2)
    c: Block(g2)
    c: Coincident(g6,g2)
    c: Weight(g3) = 1
    c: Equal(g3,g4)
    c: Equal(g3,g5)
    c: InternalAlignment(g3,g6)
    c: InternalAlignment(g4,g6)
    c: InternalAlignment(g5,g6)
    c: InternalAlignment(g7,g6)
    c: InternalAlignment(g8,g6)
    c: Block(g6)
    c: Coincident(g9,g1)
    c: Coincident(g9,g6)
    c: Horizontal(g9)
    c: Vertical(g10)
    c: Block(g10)
    c: Horizontal(g11)
    c: Block(g11)
    c: Coincident(g12,g10)
    c: Horizontal(g12)
    c: Block(g12)
    c: Coincident(g13,g11)
    c: Vertical(g13)
    c: Block(g13)
    c: Coincident(g14,g10)
    c: Horizontal(g14)
    c: Block(g14)
    c: Block(g9)
    c: Block(g1)
    c: Weight(g15) = 1
    c: Equal(g15,g16)
    c: Equal(g15,g17)
    c: InternalAlignment(g15,g18)
    c: InternalAlignment(g16,g18)
    c: InternalAlignment(g17,g18)
    c: InternalAlignment(g19,g18)
    c: InternalAlignment(g20,g18)
    c: Weight(g21) = 1
    c: Equal(g21,g22)
    c: Equal(g21,g23)
    c: InternalAlignment(g21,g24)
    c: InternalAlignment(g22,g24)
    c: InternalAlignment(g23,g24)
    c: InternalAlignment(g25,g24)
    c: InternalAlignment(g26,g24)
    c: Weight(g27) = 1
    c: Equal(g27,g28)
    c: Equal(g27,g29)
    c: Coincident(g30,g14)
    c: InternalAlignment(g27,g30)
    c: InternalAlignment(g28,g30)
    c: InternalAlignment(g29,g30)
    c: InternalAlignment(g31,g30)
    c: InternalAlignment(g32,g30)
    c: Coincident(g36,g12)
    c: Weight(g33) = 1
    c: Equal(g33,g34)
    c: Equal(g33,g35)
    c: Coincident(g36,g11)
    c: InternalAlignment(g33,g36)
    c: InternalAlignment(g34,g36)
    c: InternalAlignment(g35,g36)
    c: InternalAlignment(g37,g36)
    c: InternalAlignment(g38,g36)
    c: Coincident(g42,g13)
    c: Weight(g39) = 1
    c: Equal(g39,g40)
    c: Equal(g39,g41)
    c: Coincident(g42,g1)
    c: InternalAlignment(g39,g42)
    c: InternalAlignment(g40,g42)
    c: InternalAlignment(g41,g42)
    c: InternalAlignment(g43,g42)
    c: InternalAlignment(g44,g42)
    c: Block(g18)
    c: Block(g24)
    c: Block(g30)
    c: Block(g36)
    c: Block(g42)
    c: Horizontal(g45)
    c: Coincident(g45,g0)
    c: Vertical(g46)
    c: Coincident(g46,g45)
    c: Coincident(g47,g46)
    c: Coincident(g47,g18)
    c: Horizontal(g47)
    c: Block(g46)
    c: Coincident(g48,g18)
    c: Horizontal(g48)
    c: Distance(g48) = 1.33
    c: Vertical(g49)
    c: Coincident(g49,g48)
    c: Coincident(g50,g49)
    c: Coincident(g50,g24)
    c: Horizontal(g50)
    c: Tangent(g50,g22)
    c: Horizontal(g51)
    c: Coincident(g51,g24)
    c: Block(g51)
    c: Vertical(g52)
    c: Block(g52)
    c: Coincident(g52,g51)
    c: Coincident(g53,g52)
    c: Coincident(g53,g30)
    c: Horizontal(g53)
    c: Distance(g1) = 8.5
FEATURE [Part::Feature] Face024
  shape: bbox 9.8 x 26.5 x 2e-07 mm, 1 faces, 0 solids (baked)
FEATURE [Part::Revolution] Revolve024
  Angle = 360
  Axis = (0,1,0)
  Base = (0,0,0)
  FaceMakerClass = Part::FaceMakerBullseye
  Placement = pos=(0,0,0) rot=(0,0,1;1.5708rad)
  Solid = false
  Source = -> Face024
  Symmetric = false
FEATURE [Part::Feature] Face025
  shape: bbox 9.8 x 26.5 x 2e-07 mm, 1 faces, 0 solids (baked)
FEATURE [Part::Revolution] Revolve025
  Angle = 360
  Axis = (0,1,0)
  Base = (0,0,0)
  FaceMakerClass = Part::FaceMakerBullseye
  Placement = pos=(0,0,0) rot=(0,0,1;1.5708rad)
  Solid = false
  Source = -> Face025
  Symmetric = false
FEATURE [Part::MultiFuse] Fusion033
  Placement = pos=(-18,19,36) rot=(0,0,1;0rad)
  Shapes = -> [Revolve025,Revolve024]
FEATURE [Part::Cylinder] Cylinder014
  Angle = 360
  AttacherType = Attacher::AttachEngine3D
  Height = 20
  Placement = pos=(0,0,36.15) rot=(0,0,1;0rad)
  Radius = 14.3
FEATURE [Part::Cylinder] Cylinder015
  Angle = 360
  AttacherType = Attacher::AttachEngine3D
  Height = 10
  Placement = pos=(0,0,36.15) rot=(0,0,1;0rad)
  Radius = 4
FEATURE [Part::MultiFuse] Fusion034  label="removeToCreteHoleForPlugHousing004"
  Placement = pos=(-42,19,36) rot=(0,1,0;1.5708rad)
  Shapes = -> [Cylinder014,Cylinder015]
FEATURE [Part::Cut] Cut008  label="top004"
  Base = -> Cut004
  Placement = pos=(-1,0,0) rot=(0,0,1;0rad)
  Tool = -> Fusion034
FEATURE [Part::Box] Box005  label="Cube005"
  AttacherType = Attacher::AttachEngine3D
  Height = 28
  Length = 3
  Placement = pos=(110.7,19,22) rot=(0,0,1;0rad)
  Width = 15.7
FEATURE [Part::Cylinder] Cylinder016
  Angle = 360
  AttacherType = Attacher::AttachEngine3D
  Height = 10
  Placement = pos=(0,0,36.15) rot=(0,0,1;0rad)
  Radius = 4
FEATURE [Part::Cylinder] Cylinder017
  Angle = 360
  AttacherType = Attacher::AttachEngine3D
  Height = 20
  Placement = pos=(0,0,36.15) rot=(0,0,1;0rad)
  Radius = 10.3
FEATURE [Part::MultiFuse] Fusion035  label="removeToCreteHoleForPlugHousing005"
  Placement = pos=(70,19,36) rot=(0,1,0;1.5708rad)
  Shapes = -> [Cylinder017,Cylinder016]
FEATURE [Part::Cut] Cut009  label="plugHousingTab001"
  Base = -> Box005
  Placement = pos=(-107.4,-14,0) rot=(0,0,1;0rad)
  Tool = -> Fusion035
FEATURE [Part::Box] Box006  label="Cube006"
  AttacherType = Attacher::AttachEngine3D
  Height = 28
  Length = 3
  Placement = pos=(110.7,19,22) rot=(0,0,1;0rad)
  Width = 15.7
FEATURE [Part::Cylinder] Cylinder018
  Angle = 360
  AttacherType = Attacher::AttachEngine3D
  Height = 10
  Placement = pos=(0,0,36.15) rot=(0,0,1;0rad)
  Radius = 4
FEATURE [Part::Cylinder] Cylinder019
  Angle = 360
  AttacherType = Attacher::AttachEngine3D
  Height = 20
  Placement = pos=(0,0,36.15) rot=(0,0,1;0rad)
  Radius = 10.3
FEATURE [Part::MultiFuse] Fusion036  label="removeToCreteHoleForPlugHousing006"
  Placement = pos=(70,19,36) rot=(0,1,0;1.5708rad)
  Shapes = -> [Cylinder019,Cylinder018]
FEATURE [Part::Cut] Cut010  label="plugHousingTab002"
  Base = -> Box006
  Placement = pos=(-107.4,-14,0) rot=(0,0,1;0rad)
  Tool = -> Fusion036
FEATURE [Part::MultiFuse] Fusion037
  Placement = pos=(9.6,23,0) rot=(0,0,1;3.14159rad)
  Shapes = -> [Cut009,Cut010]
FEATURE [Part::Box] Box  label="Cube"
  AttacherType = Attacher::AttachEngine3D
  Height = 10
  Length = 3
  Placement = pos=(3.3,4,12) rot=(0,0,1;0rad)
  Width = 10
FEATURE [Part::Fillet] Fillet004
  Base = -> Fusion028
  Edges = 1 edges r=2: [Edge25]
FEATURE [Part::Fillet] Fillet005  label="plugHousing046"
  Base = -> Fillet004
  Edges = 1 edges r=2: [Edge8]
FEATURE [Part::Fillet] Fillet006
  Base = -> Box
  Edges = 1 edges r=2: [Edge11]
FEATURE [Part::Box] Box007  label="Cube007"
  AttacherType = Attacher::AttachEngine3D
  Height = 10
  Length = 3
  Placement = pos=(3.3,4,50) rot=(0,0,1;0rad)
  Width = 10
FEATURE [Part::Fillet] Fillet007
  Base = -> Box007
  Edges = 1 edges r=2: [Edge12]
FEATURE [Part::Box] Box008  label="Cube008"
  AttacherType = Attacher::AttachEngine3D
  Height = 28
  Length = 4
  Placement = pos=(5,0,22) rot=(0,0,1;0rad)
  Width = 10
FEATURE [Part::Fillet] Fillet008
  Base = -> Box008
  Edges = 1 edges r=1: [Edge7]
FEATURE [Part::Fillet] Fillet009
  Base = -> Fillet008
  Edges = 1 edges r=2: [Edge5]
FEATURE [Part::Fillet] Fillet010
  Base = -> Fillet009
  Edges = 1 edges r=2: [Edge2]
FEATURE [Sketcher::SketchObject] Sketch009  label="topSketch003"
  FullyConstrained = true
  sketch-geometry (4):
    g0: LineSegment StartX=16.8446 StartY=31.512 StartZ=0 EndX=16.3251 EndY=34.4666 EndZ=0
    g1: ArcOfCircle CenterX=19 CenterY=19.2524 CenterZ=0 NormalX=0 NormalY=0 NormalZ=1 AngleXU=0 Radius=15.4476 StartAngle=1.74483 EndAngle=2.72717
    g2: ArcOfCircle CenterX=19 CenterY=19.2524 CenterZ=0 NormalX=0 NormalY=0 NormalZ=1 AngleXU=0 Radius=12.4476 StartAngle=1.74483 EndAngle=2.73189
    g3: LineSegment StartX=4.86004 StartY=25.4725 StartZ=0 EndX=7.58253 EndY=24.2107 EndZ=0
  constraints (7):
    c: Block(g0)
    c: Coincident(g1,g0)
    c: Coincident(g2,g0)
    c: Coincident(g3,g1)
    c: Coincident(g3,g2)
    c: Block(g1)
    c: Block(g2)
FEATURE [Part::Extrusion] Extrude008
  Base = -> Sketch009
  Dir = (0,0,1)
  DirMode = 2
  FaceMakerClass = Part::FaceMakerBullseye
  LengthFwd = 10
  LengthRev = 0
  Placement = pos=(0,0,31) rot=(0,0,1;0rad)
  Solid = true
  Symmetric = false
FEATURE [Part::Cylinder] Cylinder020
  Angle = 360
  AttacherType = Attacher::AttachEngine3D
  Height = 20
  Placement = pos=(0,0,36.15) rot=(0,0,1;0rad)
  Radius = 8.2
FEATURE [Part::Cylinder] Cylinder021
  Angle = 360
  AttacherType = Attacher::AttachEngine3D
  Height = 10
  Placement = pos=(0,0,36.15) rot=(0,0,1;0rad)
  Radius = 4
FEATURE [Part::MultiFuse] Fusion038  label="removeToCreteHoleForPlugHousing007"
  Placement = pos=(-42,19,36) rot=(0,1,0;1.5708rad)
  Shapes = -> [Cylinder020,Cylinder021]
FEATURE [Part::Cut] Cut011
  Base = -> Extrude008
  Tool = -> Fusion038
FEATURE [Part::Fillet] Fillet011
  Base = -> Cut011
  Edges = 1 edges r=2: [Edge1]
FEATURE [Part::Fillet] Fillet012
  Base = -> Fillet011
  Edges = 1 edges r=2.5: [Edge1]
FEATURE [Part::Fillet] Fillet013
  Base = -> Fillet012
  Edges = 1 edges r=2.5: [Edge2]
FEATURE [Part::Box] Box010  label="Cube010"
  AttacherType = Attacher::AttachEngine3D
  Height = 16
  Length = 8
  Placement = pos=(12.7,31.52,28) rot=(0,0,1;0rad)
  Width = 4
FEATURE [Sketcher::SketchObject] Sketch010  label="topSketch004"
  FullyConstrained = true
  sketch-geometry (4):
    g0: LineSegment StartX=16.8446 StartY=31.512 StartZ=0 EndX=16.3251 EndY=34.4666 EndZ=0
    g1: ArcOfCircle CenterX=19 CenterY=19.2524 CenterZ=0 NormalX=0 NormalY=0 NormalZ=1 AngleXU=0 Radius=15.4476 StartAngle=1.74483 EndAngle=2.72717
    g2: ArcOfCircle CenterX=19 CenterY=19.2524 CenterZ=0 NormalX=0 NormalY=0 NormalZ=1 AngleXU=0 Radius=12.4476 StartAngle=1.74483 EndAngle=2.73189
    g3: LineSegment StartX=4.86004 StartY=25.4725 StartZ=0 EndX=7.58253 EndY=24.2107 EndZ=0
  constraints (7):
    c: Block(g0)
    c: Coincident(g1,g0)
    c: Coincident(g2,g0)
    c: Coincident(g3,g1)
    c: Coincident(g3,g2)
    c: Block(g1)
    c: Block(g2)
FEATURE [Part::Cylinder] Cylinder022
  Angle = 360
  AttacherType = Attacher::AttachEngine3D
  Height = 10
  Placement = pos=(0,0,36.15) rot=(0,0,1;0rad)
  Radius = 4
FEATURE [Sketcher::SketchObject] Sketch011  label="topSketch005"
  FullyConstrained = true
  sketch-geometry (4):
    g0: LineSegment StartX=16.8446 StartY=31.512 StartZ=0 EndX=16.3251 EndY=34.4666 EndZ=0
    g1: ArcOfCircle CenterX=19 CenterY=19.2524 CenterZ=0 NormalX=0 NormalY=0 NormalZ=1 AngleXU=0 Radius=15.4476 StartAngle=1.74483 EndAngle=2.72717
    g2: ArcOfCircle CenterX=19 CenterY=19.2524 CenterZ=0 NormalX=0 NormalY=0 NormalZ=1 AngleXU=0 Radius=12.4476 StartAngle=1.74483 EndAngle=2.73189
    g3: LineSegment StartX=4.86004 StartY=25.4725 StartZ=0 EndX=7.58253 EndY=24.2107 EndZ=0
  constraints (7):
    c: Block(g0)
    c: Coincident(g1,g0)
    c: Coincident(g2,g0)
    c: Coincident(g3,g1)
    c: Coincident(g3,g2)
    c: Block(g1)
    c: Block(g2)
FEATURE [Part::Extrusion] Extrude010
  Base = -> Sketch011
  Dir = (0,0,1)
  DirMode = 2
  FaceMakerClass = Part::FaceMakerBullseye
  LengthFwd = 10.6
  LengthRev = 0
  Placement = pos=(0,0,31) rot=(0,0,1;0rad)
  Solid = true
  Symmetric = false
FEATURE [Part::Cylinder] Cylinder023
  Angle = 360
  AttacherType = Attacher::AttachEngine3D
  Height = 20
  Placement = pos=(0,0,36.15) rot=(0,0,1;0rad)
  Radius = 8.2
FEATURE [Part::MultiFuse] Fusion039  label="removeToCreteHoleForPlugHousing008"
  Placement = pos=(-42,19,36) rot=(0,1,0;1.5708rad)
  Shapes = -> [Cylinder023,Cylinder022]
FEATURE [Part::Cut] Cut012
  Base = -> Extrude010
  Placement = pos=(0,0,-0.3) rot=(0,0,1;0rad)
  Tool = -> Fusion039
FEATURE [Part::Cut] Cut013
  Base = -> Box010
  Tool = -> Cut012
FEATURE [Part::Fillet] Fillet014
  Base = -> Cut013
  Edges = 1 edges r=0.7: [Edge13]
FEATURE [Part::Fillet] Fillet015
  Base = -> Fillet014
  Edges = 1 edges r=0.7: [Edge13]
FEATURE [Part::Fillet] Fillet016
  Base = -> Fillet015
  Edges = 1 edges r=0.7: [Edge16]
FEATURE [Part::Fillet] Fillet017
  Base = -> Fillet016
  Edges = 1 edges r=0.7: [Edge11]
FEATURE [Part::Fillet] Fillet018
  Base = -> Fillet017
  Edges = 1 edges r=0.7: [Edge10]
FEATURE [Part::Fillet] Fillet019
  Base = -> Fillet018
  Edges = 1 edges r=1.2: [Edge5]
FEATURE [Part::Fillet] Fillet020
  Base = -> Fillet019
  Edges = 1 edges r=1.2: [Edge12]
FEATURE [Part::Fillet] Fillet021
  Base = -> Fillet020
  Edges = 1 edges r=2: [Edge1]
  Placement = pos=(0.3,0,0) rot=(0,0,1;0rad)
FEATURE [Part::MultiFuse] Fusion040  label="top005"
  Shapes = -> [Cut008,Fillet021]
FEATURE [Part::MultiFuse] Fusion041  label="wireHolder"
  Shapes = -> [Fusion033,Fillet013]
FEATURE [Part::MultiFuse] Fusion042
  Shapes = -> [Fillet007,Fusion041]
FEATURE [Part::MultiFuse] Fusion043  label="wireHolder001"
  Shapes = -> [Fusion042,Fillet010]
FEATURE [Part::MultiFuse] Fusion044  label="wireHolder002"
  Shapes = -> [Fillet006,Fusion037,Fusion043]
FEATURE [Part::Feature] Face026
  shape: bbox 11 x 6 x 2e-07 mm, 1 faces, 0 solids (baked)
FEATURE [Part::Revolution] Revolve026
  Angle = 360
  Axis = (0,1,0)
  Base = (0,0,0)
  FaceMakerClass = Part::FaceMakerBullseye
  Placement = pos=(30.3,-1,19.7) rot=(0,0,1;0rad)
  Solid = false
  Source = -> Face026
  Symmetric = false
FEATURE [Sketcher::SketchObject] Sketch013  label="topSketch006"
  FullyConstrained = true
  sketch-geometry (13):
    g0: LineSegment StartX=117 StartY=19 StartZ=0 EndX=117 EndY=38 EndZ=0
    g1: ArcOfCircle CenterX=98 CenterY=19 CenterZ=0 NormalX=0 NormalY=0 NormalZ=1 AngleXU=0 Radius=19 StartAngle=5.7297 EndAngle=6.28319
    g2: LineSegment StartX=0 StartY=3 StartZ=0 EndX=0 EndY=19 EndZ=0
    g3: LineSegment StartX=19 StartY=38 StartZ=0 EndX=117 EndY=38 EndZ=0
    g4: ArcOfCircle CenterX=19 CenterY=19 CenterZ=0 NormalX=0 NormalY=0 NormalZ=1 AngleXU=0 Radius=19 StartAngle=1.5708 EndAngle=3.14159
    g5: ArcOfCircle CenterX=19 CenterY=19 CenterZ=0 NormalX=0 NormalY=0 NormalZ=1 AngleXU=0 Radius=16 StartAngle=1.5708 EndAngle=3.14159
    g6: ArcOfCircle CenterX=98 CenterY=19 CenterZ=0 NormalX=0 NormalY=0 NormalZ=1 AngleXU=0 Radius=16 StartAngle=5.60905 EndAngle=6.28319
    g7: LineSegment StartX=114 StartY=19 StartZ=0 EndX=114 EndY=35 EndZ=0
    g8: LineSegment StartX=110.5 StartY=9.01251 StartZ=0 EndX=114.163 EndY=9.01251 EndZ=0
    g9: LineSegment StartX=114 StartY=35 StartZ=0 EndX=19 EndY=35 EndZ=0
    g10: LineSegment StartX=0 StartY=3 StartZ=0 EndX=0 EndY=0 EndZ=0
    g11: LineSegment StartX=3 StartY=0 StartZ=0 EndX=0 EndY=0 EndZ=0
    g12: LineSegment StartX=3 StartY=19 StartZ=0 EndX=3 EndY=0 EndZ=0
  constraints (33):
    c: Vertical(g0)
    c: Distance(g0) = 19
    c: Block(g0)
    c: Coincident(g1,g0)
    c: Block(g1)
    c: Vertical(g2)
    c: Block(g2)
    c: Coincident(g3,g0)
    c: Horizontal(g3)
    c: Distance(g3) = 98
    c: Coincident(g4,g3)
    c: Coincident(g4,g2)
    c: Block(g4)
    c: Coincident(g5,g4)
    c: Coincident(g6,g1)
    c: Block(g6)
    c: Block(g5)
    c: Coincident(g7,g6)
    c: Vertical(g7)
    c: Coincident(g8,g6)
    c: Coincident(g8,g1)
    c: Coincident(g9,g7)
    c: Coincident(g9,g5)
    c: Horizontal(g9)
    c: Tangent(g9,g5)
    c: Coincident(g10,g2)
    c: Distance(g10) = 3
    c: Vertical(g10)
    c: Coincident(g11,g10)
    c: Horizontal(g11)
    c: Coincident(g12,g5)
    c: Coincident(g12,g11)
    c: Vertical(g12)
FEATURE [Part::Extrusion] Extrude011  label="top006"
  Base = -> Sketch013
  Dir = (0,0,1)
  DirMode = 2
  FaceMakerClass = Part::FaceMakerBullseye
  LengthFwd = 72
  LengthRev = 0
  Solid = true
  Symmetric = false
FEATURE [Sketcher::SketchObject] Sketch014
  FullyConstrained = true
  MapMode = 3
  Placement = pos=(0,0,0) rot=(1,0,0;1.5708rad)
  Support = -> [Extrude011]
  sketch-geometry (8):
    g0: Circle CenterX=80.351 CenterY=-67.6202 CenterZ=0 NormalX=0 NormalY=0 NormalZ=1 AngleXU=0 Radius=2
    g1: Circle CenterX=80.351 CenterY=-67.6202 CenterZ=0 NormalX=0 NormalY=0 NormalZ=1 AngleXU=0 Radius=3
    g2: Circle CenterX=80.351 CenterY=-4.92017 CenterZ=0 NormalX=0 NormalY=0 NormalZ=1 AngleXU=0 Radius=2
    g3: Circle CenterX=80.351 CenterY=-4.92017 CenterZ=0 NormalX=0 NormalY=0 NormalZ=1 AngleXU=0 Radius=3
    g4: Circle CenterX=23.851 CenterY=-4.92017 CenterZ=0 NormalX=0 NormalY=0 NormalZ=1 AngleXU=0 Radius=2
    g5: Circle CenterX=23.851 CenterY=-4.92017 CenterZ=0 NormalX=0 NormalY=0 NormalZ=1 AngleXU=0 Radius=3
    g6: Circle CenterX=23.851 CenterY=-67.6202 CenterZ=0 NormalX=0 NormalY=0 NormalZ=1 AngleXU=0 Radius=2
    g7: Circle CenterX=23.851 CenterY=-67.6202 CenterZ=0 NormalX=0 NormalY=0 NormalZ=1 AngleXU=0 Radius=3
  constraints (8):
    c: Block(g3)
    c: Block(g2)
    c: Block(g1)
    c: Block(g0)
    c: Block(g6)
    c: Block(g7)
    c: Block(g4)
    c: Block(g5)
FEATURE [Part::Feature] Face027
  shape: bbox 11 x 6 x 2e-07 mm, 1 faces, 0 solids (baked)
FEATURE [Part::Revolution] Revolve027
  Angle = 360
  Axis = (0,1,0)
  Base = (0,0,0)
  FaceMakerClass = Part::FaceMakerBullseye
  Placement = pos=(30.3,-1,51.7) rot=(0,0,1;0rad)
  Solid = false
  Source = -> Face027
  Symmetric = false
FEATURE [Part::Feature] Face028
  shape: bbox 11 x 6 x 2e-07 mm, 1 faces, 0 solids (baked)
FEATURE [Part::Revolution] Revolve028
  Angle = 360
  Axis = (0,1,0)
  Base = (0,0,0)
  FaceMakerClass = Part::FaceMakerBullseye
  Placement = pos=(62.3,-1,19.7) rot=(0,0,1;0rad)
  Solid = false
  Source = -> Face028
  Symmetric = false
FEATURE [Part::Feature] Face029
  shape: bbox 11 x 6 x 2e-07 mm, 1 faces, 0 solids (baked)
FEATURE [Part::Revolution] Revolve029
  Angle = 360
  Axis = (0,1,0)
  Base = (0,0,0)
  FaceMakerClass = Part::FaceMakerBullseye
  Placement = pos=(62.3,-1,51.7) rot=(0,0,1;0rad)
  Solid = false
  Source = -> Face029
  Symmetric = false
FEATURE [Part::Feature] Wire
  shape: bbox 11 x 5.2 x 2e-07 mm, 0 faces, 0 solids (baked)
FEATURE [Part::Revolution] Revolve030
  Angle = 360
  Axis = (0,1,0)
  Base = (0,0,0)
  FaceMakerClass = Part::FaceMakerBullseye
  Placement = pos=(30.3,38,19.7) rot=(0,0,1;0rad)
  Solid = true
  Source = -> Wire
  Symmetric = false
FEATURE [Part::Feature] Wire001
  shape: bbox 11 x 5.2 x 2e-07 mm, 0 faces, 0 solids (baked)
FEATURE [Part::Revolution] Revolve031
  Angle = 360
  Axis = (0,1,0)
  Base = (0,0,0)
  FaceMakerClass = Part::FaceMakerBullseye
  Placement = pos=(30.3,38,51.7) rot=(0,0,1;0rad)
  Solid = true
  Source = -> Wire001
  Symmetric = false
FEATURE [Part::Feature] Wire002
  shape: bbox 11 x 5.2 x 2e-07 mm, 0 faces, 0 solids (baked)
FEATURE [Part::Revolution] Revolve032
  Angle = 360
  Axis = (0,1,0)
  Base = (0,0,0)
  FaceMakerClass = Part::FaceMakerBullseye
  Placement = pos=(62.3,38,51.7) rot=(0,0,1;0rad)
  Solid = true
  Source = -> Wire002
  Symmetric = false
FEATURE [Part::Feature] Wire003
  shape: bbox 11 x 5.2 x 2e-07 mm, 0 faces, 0 solids (baked)
FEATURE [Part::Revolution] Revolve033
  Angle = 360
  Axis = (0,1,0)
  Base = (0,0,0)
  FaceMakerClass = Part::FaceMakerBullseye
  Placement = pos=(62.3,38,19.7) rot=(0,0,1;0rad)
  Solid = true
  Source = -> Wire003
  Symmetric = false
FEATURE [Part::MultiFuse] Fusion045  label="altRandScrewHousing"
  Shapes = -> [Revolve029,Revolve027,Revolve028,Revolve026]
FEATURE [Part::MultiFuse] Fusion046  label="fanScrewHousing"
  Shapes = -> [Revolve033,Revolve032,Revolve031,Revolve030]
FEATURE [Sketcher::SketchObject] Sketch015
  FullyConstrained = true
  sketch-geometry (17):
    g0: Circle CenterX=-3.5 CenterY=23.5 CenterZ=0 NormalX=0 NormalY=0 NormalZ=1 AngleXU=0 Radius=1
    g1: Circle CenterX=-1 CenterY=15.25 CenterZ=0 NormalX=0 NormalY=0 NormalZ=1 AngleXU=0 Radius=1
    g2: Circle CenterX=-3.5 CenterY=7 CenterZ=0 NormalX=0 NormalY=0 NormalZ=1 AngleXU=0 Radius=1
    g3: BSplineCurve PolesCount=3 KnotsCount=2 Degree=2 IsPeriodic=0
    g4: GeomPoint X=-3.5 Y=23.5 Z=0
    g5: GeomPoint X=-3.5 Y=7 Z=0
    g6: Circle CenterX=-4.8 CenterY=30.5 CenterZ=0 NormalX=0 NormalY=0 NormalZ=1 AngleXU=0 Radius=1
    g7: Circle CenterX=-3.5 CenterY=30.5 CenterZ=0 NormalX=0 NormalY=0 NormalZ=1 AngleXU=0 Radius=1
    g8: Circle CenterX=-3.5 CenterY=29.2 CenterZ=0 NormalX=0 NormalY=0 NormalZ=1 AngleXU=0 Radius=1
    g9: BSplineCurve PolesCount=3 KnotsCount=2 Degree=2 IsPeriodic=0
    g10: GeomPoint X=-4.8 Y=30.5 Z=0
    g11: GeomPoint X=-3.5 Y=29.2 Z=0
    g12: LineSegment StartX=-3.5 StartY=29.2 StartZ=0 EndX=-3.5 EndY=23.5 EndZ=0
    g13: LineSegment StartX=-4.8 StartY=30.5 StartZ=0 EndX=0 EndY=30.5 EndZ=0
    g14: LineSegment StartX=-3.5 StartY=0.3 StartZ=0 EndX=0 EndY=0.3 EndZ=0
    g15: LineSegment StartX=-3.5 StartY=0.3 StartZ=0 EndX=-3.5 EndY=7 EndZ=0
    g16: LineSegment StartX=0 StartY=0.3 StartZ=0 EndX=0 EndY=30.5 EndZ=0
  constraints (33):
    c: Weight(g0) = 1
    c: Equal(g0,g1)
    c: Equal(g0,g2)
    c: InternalAlignment(g0,g3)
    c: InternalAlignment(g1,g3)
    c: InternalAlignment(g2,g3)
    c: InternalAlignment(g4,g3)
    c: InternalAlignment(g5,g3)
    c: Block(g3)
    c: Weight(g6) = 1
    c: Equal(g6,g7)
    c: Equal(g6,g8)
    c: InternalAlignment(g6,g9)
    c: InternalAlignment(g7,g9)
    c: InternalAlignment(g8,g9)
    c: InternalAlignment(g10,g9)
    c: InternalAlignment(g11,g9)
    c: Block(g9)
    c: Coincident(g12,g9)
    c: Coincident(g12,g3)
    c: Vertical(g12)
    c: Coincident(g13,g9)
    c: Horizontal(g13)
    c: Distance(g13) = 4.8
    c: Horizontal(g14)
    c: Block(g14)
    c: Coincident(g15,g14)
    c: Coincident(g15,g3)
    c: Vertical(g15)
    c: Coincident(g16,g14)
    c: Coincident(g16,g13)
    c: Vertical(g16)
    c: Tangent(g16,g1)
FEATURE [Sketcher::SketchObject] Sketch016
  FullyConstrained = true
  sketch-geometry (16):
    g0: Circle CenterX=-3.5 CenterY=23.5 CenterZ=0 NormalX=0 NormalY=0 NormalZ=1 AngleXU=0 Radius=1
    g1: Circle CenterX=-1 CenterY=15.25 CenterZ=0 NormalX=0 NormalY=0 NormalZ=1 AngleXU=0 Radius=1
    g2: Circle CenterX=-3.5 CenterY=7 CenterZ=0 NormalX=0 NormalY=0 NormalZ=1 AngleXU=0 Radius=1
    g3: BSplineCurve PolesCount=3 KnotsCount=2 Degree=2 IsPeriodic=0
    g4: GeomPoint X=-3.5 Y=23.5 Z=0
    g5: GeomPoint X=-3.5 Y=7 Z=0
    g6: LineSegment StartX=-3.5 StartY=28.2 StartZ=0 EndX=-3.5 EndY=23.5 EndZ=0
    g7: LineSegment StartX=0 StartY=29.5 StartZ=0 EndX=0 EndY=30 EndZ=0
    g8: LineSegment StartX=-3.5 StartY=28.2 StartZ=0 EndX=-3.5 EndY=30 EndZ=0
    g9: LineSegment StartX=0 StartY=30 StartZ=0 EndX=0 EndY=30.5 EndZ=0
    g10: LineSegment StartX=0 StartY=30.5 StartZ=0 EndX=-3.5 EndY=30.5 EndZ=0
    g11: LineSegment StartX=-3.5 StartY=30.5 StartZ=0 EndX=-3.5 EndY=30 EndZ=0
    g12: LineSegment StartX=0 StartY=29.5 StartZ=0 EndX=0 EndY=5 EndZ=0
    g13: LineSegment StartX=-3.5 StartY=0.3 StartZ=0 EndX=-3.5 EndY=7 EndZ=0
    g14: LineSegment StartX=-3.5 StartY=0.3 StartZ=0 EndX=0 EndY=0.3 EndZ=0
    g15: LineSegment StartX=0 StartY=5 StartZ=0 EndX=0 EndY=0.3 EndZ=0
  constraints (39):
    c: Weight(g0) = 1
    c: Equal(g0,g1)
    c: Equal(g0,g2)
    c: InternalAlignment(g0,g3)
    c: InternalAlignment(g1,g3)
    c: InternalAlignment(g2,g3)
    c: InternalAlignment(g4,g3)
    c: InternalAlignment(g5,g3)
    c: Block(g3)
    c: Coincident(g6,g3)
    c: Vertical(g6)
    c: Vertical(g7)
    c: Distance(g7) = 0.5
    c: Coincident(g8,g6)
    c: Vertical(g8)
    c: Block(g6)
    c: Block(g7)
    c: Vertical(g9)
    c: Equal(g7,g9) = 0.5
    c: Block(g9)
    c: Coincident(g9,g7)
    c: Horizontal(g10)
    c: Coincident(g10,g9)
    c: Coincident(g11,g10)
    c: Coincident(g11,g8)
    c: Vertical(g11)
    c: Block(g11)
    c: Coincident(g12,g7)
    c: Vertical(g12)
    c: Coincident(g13,g3)
    c: Vertical(g13)
    c: Distance(g13) = 6.7
    c: Coincident(g14,g13)
    c: Horizontal(g14)
    c: Block(g14)
    c: Coincident(g15,g12)
    c: Coincident(g15,g14)
    c: Vertical(g15)
    c: Block(g15)
FEATURE [Sketcher::SketchObject] Sketch017
  FullyConstrained = true
  sketch-geometry (11):
    g0: LineSegment StartX=-3.5 StartY=1e-16 StartZ=0 EndX=-1.6 EndY=1e-16 EndZ=0
    g1: LineSegment StartX=-1.6 StartY=1e-16 StartZ=0 EndX=-1.6 EndY=1.5 EndZ=0
    g2: LineSegment StartX=-3.5 StartY=1.5 StartZ=0 EndX=-1.6 EndY=1.5 EndZ=0
    g3: LineSegment StartX=-3.5 StartY=1e-16 StartZ=0 EndX=-4.8 EndY=1e-16 EndZ=0
    g4: Circle CenterX=-3.5 CenterY=1.3 CenterZ=0 NormalX=0 NormalY=0 NormalZ=1 AngleXU=0 Radius=1
    g5: Circle CenterX=-3.5 CenterY=1e-16 CenterZ=0 NormalX=0 NormalY=0 NormalZ=1 AngleXU=0 Radius=1
    g6: Circle CenterX=-4.8 CenterY=1e-16 CenterZ=0 NormalX=0 NormalY=0 NormalZ=1 AngleXU=0 Radius=1
    g7: BSplineCurve PolesCount=3 KnotsCount=2 Degree=2 IsPeriodic=0
    g8: GeomPoint X=-3.5 Y=1.3 Z=0
    g9: GeomPoint X=-4.8 Y=1e-16 Z=0
    g10: LineSegment StartX=-3.5 StartY=1.3 StartZ=0 EndX=-3.5 EndY=1.5 EndZ=0
  constraints (24):
    c: Horizontal(g0)
    c: Distance(g0) = 1.9
    c: Block(g0)
    c: Coincident(g1,g0)
    c: Vertical(g1)
    c: Coincident(g2,g1)
    c: Horizontal(g2)
    c: Coincident(g3,g0)
    c: Horizontal(g3)
    c: Distance(g3) = 1.3
    c: Weight(g4) = 1
    c: Equal(g4,g5)
    c: Coincident(g5,g0)
    c: Equal(g4,g6)
    c: Coincident(g7,g3)
    c: InternalAlignment(g4,g7)
    c: InternalAlignment(g5,g7)
    c: InternalAlignment(g6,g7)
    c: InternalAlignment(g8,g7)
    c: InternalAlignment(g9,g7)
    c: Coincident(g10,g7)
    c: Coincident(g10,g2)
    c: Vertical(g10)
    c: Block(g10)
FEATURE [Part::Feature] Face035
  shape: bbox 3.2 x 1.5 x 2e-07 mm, 1 faces, 0 solids (baked)
FEATURE [Part::Revolution] Revolve039  label="backCaseScrewRetainer"
  Angle = 360
  Axis = (0,1,0)
  Base = (0,0,0)
  FaceMakerClass = Part::FaceMakerBullseye
  Placement = pos=(12.5,3,62) rot=(0,0,1;0rad)
  Solid = false
  Source = -> Face035
  Symmetric = false
FEATURE [Part::Feature] Face036
  shape: bbox 3.2 x 1.5 x 2e-07 mm, 1 faces, 0 solids (baked)
FEATURE [Part::Feature] Face039
  shape: bbox 4.8 x 30.2 x 2e-07 mm, 1 faces, 0 solids (baked)
FEATURE [Part::Revolution] Revolve043  label="frontCaseScrewPost002"
  Angle = 360
  Axis = (0,1,0)
  Base = (0,0,0)
  FaceMakerClass = Part::FaceMakerBullseye
  Placement = pos=(89.5,4.5,3.5) rot=(0,0,1;0rad)
  Solid = false
  Source = -> Face039
  Symmetric = false
FEATURE [Part::Feature] Face042
  shape: bbox 4.8 x 30.2 x 2e-07 mm, 1 faces, 0 solids (baked)
FEATURE [Part::Revolution] Revolve046  label="frontCaseScrewPost003"
  Angle = 360
  Axis = (0,1,0)
  Base = (0,0,0)
  FaceMakerClass = Part::FaceMakerBullseye
  Placement = pos=(89.5,4.5,68.5) rot=(0,0,1;0rad)
  Solid = false
  Source = -> Face042
  Symmetric = false
FEATURE [Part::Feature] Face043
  shape: bbox 3.2 x 1.5 x 2e-07 mm, 1 faces, 0 solids (baked)
FEATURE [Part::Revolution] Revolve047  label="frontCaseScrewRetainer002"
  Angle = 360
  Axis = (0,1,0)
  Base = (0,0,0)
  FaceMakerClass = Part::FaceMakerBullseye
  Placement = pos=(89.5,3,68.5) rot=(0,0,1;0rad)
  Solid = false
  Source = -> Face043
  Symmetric = false
FEATURE [Part::Feature] Face044
  shape: bbox 3.2 x 1.5 x 2e-07 mm, 1 faces, 0 solids (baked)
FEATURE [Part::Revolution] Revolve048  label="frontCaseScrewRetainer003"
  Angle = 360
  Axis = (0,1,0)
  Base = (0,0,0)
  FaceMakerClass = Part::FaceMakerBullseye
  Placement = pos=(89.5,3,3.5) rot=(0,0,1;0rad)
  Solid = false
  Source = -> Face044
  Symmetric = false
FEATURE [App::MeasureDistance] Distance002  label="Distance: 1.67 mm"
  Distance = 1.66921
  P1 = (99.2361,4.7524,71.7)
  P2 = (99.2347,6.42161,71.7)
FEATURE [Sketcher::SketchObject] Sketch018
  FullyConstrained = true
  sketch-geometry (7):
    g0: LineSegment StartX=0 StartY=0 StartZ=0 EndX=0 EndY=6 EndZ=0
    g1: Circle CenterX=0 CenterY=0 CenterZ=0 NormalX=0 NormalY=0 NormalZ=1 AngleXU=0 Radius=1
    g2: Circle CenterX=8 CenterY=6 CenterZ=0 NormalX=0 NormalY=0 NormalZ=1 AngleXU=0 Radius=1
    g3: BSplineCurve PolesCount=3 KnotsCount=2 Degree=2 IsPeriodic=0
    g4: GeomPoint X=0 Y=0 Z=0
    g5: GeomPoint X=8 Y=6 Z=0
    g6: LineSegment StartX=0 StartY=6 StartZ=0 EndX=8 EndY=6 EndZ=0
  constraints (14):
    c: Coincident(g0,g-1)
    c: Distance(g0) = 6
    c: Vertical(g0)
    c: Coincident(g3,g0)
    c: Weight(g1) = 1
    c: Equal(g1,g2)
    c: InternalAlignment(g1,g3)
    c: InternalAlignment(g2,g3)
    c: InternalAlignment(g4,g3)
    c: InternalAlignment(g5,g3)
    c: Block(g3)
    c: Coincident(g6,g0)
    c: Coincident(g6,g3)
    c: Horizontal(g6)
FEATURE [Part::Extrusion] Extrude012  label="caseScrewPillarBracket"
  Base = -> Sketch018
  Dir = (0,0,1)
  DirMode = 2
  FaceMakerClass = Part::FaceMakerBullseye
  LengthFwd = 2.4
  LengthRev = 0
  Placement = pos=(15.76,29,8.8) rot=(0,1,0;0rad)
  Solid = true
  Symmetric = false
FEATURE [Sketcher::SketchObject] Sketch019
  FullyConstrained = true
  sketch-geometry (7):
    g0: LineSegment StartX=0 StartY=0 StartZ=0 EndX=0 EndY=6 EndZ=0
    g1: Circle CenterX=0 CenterY=0 CenterZ=0 NormalX=0 NormalY=0 NormalZ=1 AngleXU=0 Radius=1
    g2: Circle CenterX=8 CenterY=6 CenterZ=0 NormalX=0 NormalY=0 NormalZ=1 AngleXU=0 Radius=1
    g3: BSplineCurve PolesCount=3 KnotsCount=2 Degree=2 IsPeriodic=0
    g4: GeomPoint X=0 Y=0 Z=0
    g5: GeomPoint X=8 Y=6 Z=0
    g6: LineSegment StartX=0 StartY=6 StartZ=0 EndX=8 EndY=6 EndZ=0
  constraints (14):
    c: Coincident(g0,g-1)
    c: Distance(g0) = 6
    c: Vertical(g0)
    c: Coincident(g3,g0)
    c: Weight(g1) = 1
    c: Equal(g1,g2)
    c: InternalAlignment(g1,g3)
    c: InternalAlignment(g2,g3)
    c: InternalAlignment(g4,g3)
    c: InternalAlignment(g5,g3)
    c: Block(g3)
    c: Coincident(g6,g0)
    c: Coincident(g6,g3)
    c: Horizontal(g6)
FEATURE [Part::Extrusion] Extrude013  label="caseScrewPillarBracket001"
  Base = -> Sketch019
  Dir = (0,0,1)
  DirMode = 2
  FaceMakerClass = Part::FaceMakerBullseye
  LengthFwd = 2.4
  LengthRev = 0
  Placement = pos=(15.76,29,60.8) rot=(0,0,1;0rad)
  Solid = true
  Symmetric = false
FEATURE [Sketcher::SketchObject] Sketch020
  FullyConstrained = true
  sketch-geometry (7):
    g0: LineSegment StartX=0 StartY=0 StartZ=0 EndX=0 EndY=6 EndZ=0
    g1: Circle CenterX=0 CenterY=0 CenterZ=0 NormalX=0 NormalY=0 NormalZ=1 AngleXU=0 Radius=1
    g2: Circle CenterX=8 CenterY=6 CenterZ=0 NormalX=0 NormalY=0 NormalZ=1 AngleXU=0 Radius=1
    g3: BSplineCurve PolesCount=3 KnotsCount=2 Degree=2 IsPeriodic=0
    g4: GeomPoint X=0 Y=0 Z=0
    g5: GeomPoint X=8 Y=6 Z=0
    g6: LineSegment StartX=0 StartY=6 StartZ=0 EndX=8 EndY=6 EndZ=0
  constraints (14):
    c: Coincident(g0,g-1)
    c: Distance(g0) = 6
    c: Vertical(g0)
    c: Coincident(g3,g0)
    c: Weight(g1) = 1
    c: Equal(g1,g2)
    c: InternalAlignment(g1,g3)
    c: InternalAlignment(g2,g3)
    c: InternalAlignment(g4,g3)
    c: InternalAlignment(g5,g3)
    c: Block(g3)
    c: Coincident(g6,g0)
    c: Coincident(g6,g3)
    c: Horizontal(g6)
FEATURE [Part::Extrusion] Extrude014  label="caseScrewPillarBracket002"
  Base = -> Sketch020
  Dir = (0,0,1)
  DirMode = 2
  FaceMakerClass = Part::FaceMakerBullseye
  LengthFwd = 2.4
  LengthRev = 0
  Placement = pos=(13.7,29,13.26) rot=(0,-1,0;1.5708rad)
  Solid = true
  Symmetric = false
FEATURE [Sketcher::SketchObject] Sketch021
  FullyConstrained = true
  sketch-geometry (7):
    g0: LineSegment StartX=0 StartY=0 StartZ=0 EndX=0 EndY=6 EndZ=0
    g1: Circle CenterX=0 CenterY=0 CenterZ=0 NormalX=0 NormalY=0 NormalZ=1 AngleXU=0 Radius=1
    g2: Circle CenterX=8 CenterY=6 CenterZ=0 NormalX=0 NormalY=0 NormalZ=1 AngleXU=0 Radius=1
    g3: BSplineCurve PolesCount=3 KnotsCount=2 Degree=2 IsPeriodic=0
    g4: GeomPoint X=0 Y=0 Z=0
    g5: GeomPoint X=8 Y=6 Z=0
    g6: LineSegment StartX=0 StartY=6 StartZ=0 EndX=8 EndY=6 EndZ=0
  constraints (14):
    c: Coincident(g0,g-1)
    c: Distance(g0) = 6
    c: Vertical(g0)
    c: Coincident(g3,g0)
    c: Weight(g1) = 1
    c: Equal(g1,g2)
    c: InternalAlignment(g1,g3)
    c: InternalAlignment(g2,g3)
    c: InternalAlignment(g4,g3)
    c: InternalAlignment(g5,g3)
    c: Block(g3)
    c: Coincident(g6,g0)
    c: Coincident(g6,g3)
    c: Horizontal(g6)
FEATURE [Part::Extrusion] Extrude015  label="caseScrewPillarBracket003"
  Base = -> Sketch021
  Dir = (0,0,1)
  DirMode = 2
  FaceMakerClass = Part::FaceMakerBullseye
  LengthFwd = 2.4
  LengthRev = 0
  Placement = pos=(11.3,29,58.74) rot=(0,1,0;1.5708rad)
  Solid = true
  Symmetric = false
FEATURE [Sketcher::SketchObject] Sketch022
  FullyConstrained = true
  sketch-geometry (7):
    g0: LineSegment StartX=0 StartY=0 StartZ=0 EndX=0 EndY=6 EndZ=0
    g1: Circle CenterX=0 CenterY=0 CenterZ=0 NormalX=0 NormalY=0 NormalZ=1 AngleXU=0 Radius=1
    g2: Circle CenterX=8 CenterY=6 CenterZ=0 NormalX=0 NormalY=0 NormalZ=1 AngleXU=0 Radius=1
    g3: BSplineCurve PolesCount=3 KnotsCount=2 Degree=2 IsPeriodic=0
    g4: GeomPoint X=0 Y=0 Z=0
    g5: GeomPoint X=8 Y=6 Z=0
    g6: LineSegment StartX=0 StartY=6 StartZ=0 EndX=8 EndY=6 EndZ=0
  constraints (14):
    c: Coincident(g0,g-1)
    c: Distance(g0) = 6
    c: Vertical(g0)
    c: Coincident(g3,g0)
    c: Weight(g1) = 1
    c: Equal(g1,g2)
    c: InternalAlignment(g1,g3)
    c: InternalAlignment(g2,g3)
    c: InternalAlignment(g4,g3)
    c: InternalAlignment(g5,g3)
    c: Block(g3)
    c: Coincident(g6,g0)
    c: Coincident(g6,g3)
    c: Horizontal(g6)
FEATURE [Part::Extrusion] Extrude016  label="caseScrewPillarBracket004"
  Base = -> Sketch022
  Dir = (0,0,1)
  DirMode = 2
  FaceMakerClass = Part::FaceMakerBullseye
  LengthFwd = 2.4
  LengthRev = 0
  Placement = pos=(88.3,29,65.23) rot=(0,1,0;1.5708rad)
  Solid = true
  Symmetric = false
FEATURE [Sketcher::SketchObject] Sketch023
  FullyConstrained = true
  sketch-geometry (7):
    g0: LineSegment StartX=0 StartY=0 StartZ=0 EndX=0 EndY=6 EndZ=0
    g1: Circle CenterX=0 CenterY=0 CenterZ=0 NormalX=0 NormalY=0 NormalZ=1 AngleXU=0 Radius=1
    g2: Circle CenterX=8 CenterY=6 CenterZ=0 NormalX=0 NormalY=0 NormalZ=1 AngleXU=0 Radius=1
    g3: BSplineCurve PolesCount=3 KnotsCount=2 Degree=2 IsPeriodic=0
    g4: GeomPoint X=0 Y=0 Z=0
    g5: GeomPoint X=8 Y=6 Z=0
    g6: LineSegment StartX=0 StartY=6 StartZ=0 EndX=8 EndY=6 EndZ=0
  constraints (14):
    c: Coincident(g0,g-1)
    c: Distance(g0) = 6
    c: Vertical(g0)
    c: Coincident(g3,g0)
    c: Weight(g1) = 1
    c: Equal(g1,g2)
    c: InternalAlignment(g1,g3)
    c: InternalAlignment(g2,g3)
    c: InternalAlignment(g4,g3)
    c: InternalAlignment(g5,g3)
    c: Block(g3)
    c: Coincident(g6,g0)
    c: Coincident(g6,g3)
    c: Horizontal(g6)
FEATURE [Part::Extrusion] Extrude017  label="caseScrewPillarBracket005"
  Base = -> Sketch023
  Dir = (0,0,1)
  DirMode = 2
  FaceMakerClass = Part::FaceMakerBullseye
  LengthFwd = 2.4
  LengthRev = 0
  Placement = pos=(90.7,29,6.77) rot=(0,-1,0;1.5708rad)
  Solid = true
  Symmetric = false
FEATURE [Sketcher::SketchObject] Sketch024
  FullyConstrained = true
  sketch-geometry (7):
    g0: LineSegment StartX=0 StartY=0 StartZ=0 EndX=0 EndY=6 EndZ=0
    g1: Circle CenterX=0 CenterY=0 CenterZ=0 NormalX=0 NormalY=0 NormalZ=1 AngleXU=0 Radius=1
    g2: Circle CenterX=8 CenterY=6 CenterZ=0 NormalX=0 NormalY=0 NormalZ=1 AngleXU=0 Radius=1
    g3: BSplineCurve PolesCount=3 KnotsCount=2 Degree=2 IsPeriodic=0
    g4: GeomPoint X=0 Y=0 Z=0
    g5: GeomPoint X=8 Y=6 Z=0
    g6: LineSegment StartX=0 StartY=6 StartZ=0 EndX=8 EndY=6 EndZ=0
  constraints (14):
    c: Coincident(g0,g-1)
    c: Distance(g0) = 6
    c: Vertical(g0)
    c: Coincident(g3,g0)
    c: Weight(g1) = 1
    c: Equal(g1,g2)
    c: InternalAlignment(g1,g3)
    c: InternalAlignment(g2,g3)
    c: InternalAlignment(g4,g3)
    c: InternalAlignment(g5,g3)
    c: Block(g3)
    c: Coincident(g6,g0)
    c: Coincident(g6,g3)
    c: Horizontal(g6)
FEATURE [Part::Extrusion] Extrude018  label="caseScrewPillarBracket006"
  Base = -> Sketch024
  Dir = (0,0,1)
  DirMode = 2
  FaceMakerClass = Part::FaceMakerBullseye
  LengthFwd = 2.4
  LengthRev = 0
  Placement = pos=(103.7,29,6.77) rot=(0,-1,0;1.5708rad)
  Solid = true
  Symmetric = false
FEATURE [Sketcher::SketchObject] Sketch025
  FullyConstrained = true
  sketch-geometry (7):
    g0: LineSegment StartX=0 StartY=0 StartZ=0 EndX=0 EndY=6 EndZ=0
    g1: Circle CenterX=0 CenterY=0 CenterZ=0 NormalX=0 NormalY=0 NormalZ=1 AngleXU=0 Radius=1
    g2: Circle CenterX=8 CenterY=6 CenterZ=0 NormalX=0 NormalY=0 NormalZ=1 AngleXU=0 Radius=1
    g3: BSplineCurve PolesCount=3 KnotsCount=2 Degree=2 IsPeriodic=0
    g4: GeomPoint X=0 Y=0 Z=0
    g5: GeomPoint X=8 Y=6 Z=0
    g6: LineSegment StartX=0 StartY=6 StartZ=0 EndX=8 EndY=6 EndZ=0
  constraints (14):
    c: Coincident(g0,g-1)
    c: Distance(g0) = 6
    c: Vertical(g0)
    c: Coincident(g3,g0)
    c: Weight(g1) = 1
    c: Equal(g1,g2)
    c: InternalAlignment(g1,g3)
    c: InternalAlignment(g2,g3)
    c: InternalAlignment(g4,g3)
    c: InternalAlignment(g5,g3)
    c: Block(g3)
    c: Coincident(g6,g0)
    c: Coincident(g6,g3)
    c: Horizontal(g6)
FEATURE [Part::Extrusion] Extrude019  label="caseScrewPillarBracket007"
  Base = -> Sketch025
  Dir = (0,0,1)
  DirMode = 2
  FaceMakerClass = Part::FaceMakerBullseye
  LengthFwd = 2.4
  LengthRev = 0
  Placement = pos=(101.3,29,65.23) rot=(0,1,0;1.5708rad)
  Solid = true
  Symmetric = false
FEATURE [Part::Box] Box011  label="frontCaseScrewPillarBracket"
  AttacherType = Attacher::AttachEngine3D
  Height = 2.4
  Length = 16
  Placement = pos=(87,28,2.3) rot=(0,0,1;0rad)
  Width = 7
FEATURE [Part::Box] Box012  label="frontCaseScrewPillarBracket001"
  AttacherType = Attacher::AttachEngine3D
  Height = 2.4
  Length = 16
  Placement = pos=(87,28,67.3) rot=(0,0,1;0rad)
  Width = 7
FEATURE [Sketcher::SketchObject] Sketch026
  FullyConstrained = true
  sketch-geometry (17):
    g0: Circle CenterX=-3.5 CenterY=23.5 CenterZ=0 NormalX=0 NormalY=0 NormalZ=1 AngleXU=0 Radius=1
    g1: Circle CenterX=-1 CenterY=15.25 CenterZ=0 NormalX=0 NormalY=0 NormalZ=1 AngleXU=0 Radius=1
    g2: Circle CenterX=-3.5 CenterY=7 CenterZ=0 NormalX=0 NormalY=0 NormalZ=1 AngleXU=0 Radius=1
    g3: BSplineCurve PolesCount=3 KnotsCount=2 Degree=2 IsPeriodic=0
    g4: GeomPoint X=-3.5 Y=23.5 Z=0
    g5: GeomPoint X=-3.5 Y=7 Z=0
    g6: Circle CenterX=-4.8 CenterY=30.5 CenterZ=0 NormalX=0 NormalY=0 NormalZ=1 AngleXU=0 Radius=1
    g7: Circle CenterX=-3.5 CenterY=30.5 CenterZ=0 NormalX=0 NormalY=0 NormalZ=1 AngleXU=0 Radius=1
    g8: Circle CenterX=-3.5 CenterY=29.2 CenterZ=0 NormalX=0 NormalY=0 NormalZ=1 AngleXU=0 Radius=1
    g9: BSplineCurve PolesCount=3 KnotsCount=2 Degree=2 IsPeriodic=0
    g10: GeomPoint X=-4.8 Y=30.5 Z=0
    g11: GeomPoint X=-3.5 Y=29.2 Z=0
    g12: LineSegment StartX=-3.5 StartY=29.2 StartZ=0 EndX=-3.5 EndY=23.5 EndZ=0
    g13: LineSegment StartX=-4.8 StartY=30.5 StartZ=0 EndX=0 EndY=30.5 EndZ=0
    g14: LineSegment StartX=-3.5 StartY=5 StartZ=0 EndX=-3.5 EndY=7 EndZ=0
    g15: LineSegment StartX=0 StartY=5 StartZ=0 EndX=0 EndY=30.5 EndZ=0
    g16: LineSegment StartX=-3.5 StartY=5 StartZ=0 EndX=0 EndY=5 EndZ=0
  constraints (33):
    c: Weight(g0) = 1
    c: Equal(g0,g1)
    c: Equal(g0,g2)
    c: InternalAlignment(g0,g3)
    c: InternalAlignment(g1,g3)
    c: InternalAlignment(g2,g3)
    c: InternalAlignment(g4,g3)
    c: InternalAlignment(g5,g3)
    c: Block(g3)
    c: Weight(g6) = 1
    c: Equal(g6,g7)
    c: Equal(g6,g8)
    c: InternalAlignment(g6,g9)
    c: InternalAlignment(g7,g9)
    c: InternalAlignment(g8,g9)
    c: InternalAlignment(g10,g9)
    c: InternalAlignment(g11,g9)
    c: Block(g9)
    c: Coincident(g12,g9)
    c: Coincident(g12,g3)
    c: Vertical(g12)
    c: Coincident(g13,g9)
    c: Horizontal(g13)
    c: Distance(g13) = 4.8
    c: Coincident(g14,g3)
    c: Vertical(g14)
    c: Coincident(g15,g13)
    c: Vertical(g15)
    c: Tangent(g15,g1)
    c: Distance(g14) = 2
    c: Coincident(g16,g14)
    c: Horizontal(g16)
    c: Coincident(g15,g16)
FEATURE [Part::Feature] Face050
  shape: bbox 4.8 x 25.5 x 2e-07 mm, 1 faces, 0 solids (baked)
FEATURE [Part::Revolution] Revolve054  label="moreFrontCaseScrewPost001"
  Angle = 360
  Axis = (0,1,0)
  Base = (0,0,0)
  FaceMakerClass = Part::FaceMakerBullseye
  Placement = pos=(102.5,4.5,3.5) rot=(0,0,1;0rad)
  Solid = false
  Source = -> Face050
  Symmetric = false
FEATURE [Part::Feature] Face051
  shape: bbox 4.8 x 25.5 x 2e-07 mm, 1 faces, 0 solids (baked)
FEATURE [Part::Revolution] Revolve055  label="moreFrontCaseScrewPost002"
  Angle = 360
  Axis = (0,1,0)
  Base = (0,0,0)
  FaceMakerClass = Part::FaceMakerBullseye
  Placement = pos=(102.5,4.5,68.5) rot=(0,0,1;0rad)
  Solid = false
  Source = -> Face051
  Symmetric = false
FEATURE [Sketcher::SketchObject] Sketch027
  FullyConstrained = true
  sketch-geometry (10):
    g0: LineSegment StartX=-1.6 StartY=4.7 StartZ=0 EndX=-1.6 EndY=1.7 EndZ=0
    g1: LineSegment StartX=-3.5 StartY=4.7 StartZ=0 EndX=-1.6 EndY=4.7 EndZ=0
    g2: LineSegment StartX=-1.6 StartY=1.7 StartZ=0 EndX=-1.6 EndY=1.5 EndZ=0
    g3: LineSegment StartX=-1.6 StartY=1.5 StartZ=0 EndX=-5.2 EndY=1.5 EndZ=0
    g4: Circle CenterX=-3.5 CenterY=4.7 CenterZ=0 NormalX=0 NormalY=0 NormalZ=1 AngleXU=0 Radius=1
    g5: Circle CenterX=-3.59627 CenterY=2.99743 CenterZ=0 NormalX=0 NormalY=0 NormalZ=1 AngleXU=0 Radius=1
    g6: Circle CenterX=-5.2 CenterY=1.5 CenterZ=0 NormalX=0 NormalY=0 NormalZ=1 AngleXU=0 Radius=1
    g7: BSplineCurve PolesCount=3 KnotsCount=2 Degree=2 IsPeriodic=0
    g8: GeomPoint X=-3.5 Y=4.7 Z=0
    g9: GeomPoint X=-5.2 Y=1.5 Z=0
  constraints (23):
    c: Vertical(g0)
    c: Distance(g0) = 3
    c: Coincident(g1,g0)
    c: Horizontal(g1)
    c: Block(g0)
    c: Block(g1)
    c: Coincident(g2,g0)
    c: Vertical(g2)
    c: Distance(g2) = 0.2
    c: Coincident(g3,g2)
    c: Horizontal(g3)
    c: Block(g3)
    c: Coincident(g7,g1)
    c: Weight(g4) = 1
    c: Equal(g4,g5)
    c: Equal(g4,g6)
    c: Coincident(g7,g3)
    c: InternalAlignment(g4,g7)
    c: InternalAlignment(g5,g7)
    c: InternalAlignment(g6,g7)
    c: InternalAlignment(g8,g7)
    c: InternalAlignment(g9,g7)
    c: Block(g7)
FEATURE [Sketcher::SketchObject] Sketch028
  FullyConstrained = true
  sketch-geometry (18):
    g0: LineSegment StartX=0 StartY=3e-16 StartZ=0 EndX=0 EndY=1.7 EndZ=0
    g1: LineSegment StartX=-3.5 StartY=0 StartZ=0 EndX=-3.5 EndY=0.9 EndZ=0
    g2: Circle CenterX=-2.7 CenterY=1.7 CenterZ=0 NormalX=0 NormalY=0 NormalZ=1 AngleXU=0 Radius=1
    g3: Circle CenterX=-3.5 CenterY=1.7 CenterZ=0 NormalX=0 NormalY=0 NormalZ=1 AngleXU=0 Radius=1
    g4: Circle CenterX=-3.5 CenterY=0.9 CenterZ=0 NormalX=0 NormalY=0 NormalZ=1 AngleXU=0 Radius=1
    g5: BSplineCurve PolesCount=3 KnotsCount=2 Degree=2 IsPeriodic=0
    g6: GeomPoint X=-2.7 Y=1.7 Z=0
    g7: GeomPoint X=-3.5 Y=0.9 Z=0
    g8: LineSegment StartX=-3.5 StartY=0 StartZ=0 EndX=-3.5 EndY=-7 EndZ=0
    g9: LineSegment StartX=0 StartY=3e-16 StartZ=0 EndX=0 EndY=-7 EndZ=0
    g10: LineSegment StartX=-3.5 StartY=-7 StartZ=0 EndX=0 EndY=-7 EndZ=0
    g11: LineSegment StartX=-2.7 StartY=1.7 StartZ=0 EndX=-1.6 EndY=1.7 EndZ=0
    g12: LineSegment StartX=0 StartY=1.7 StartZ=0 EndX=0 EndY=4.5 EndZ=0
    g13: LineSegment StartX=0 StartY=4.5 StartZ=0 EndX=0 EndY=10.8 EndZ=0
    g14: LineSegment StartX=0 StartY=10.8 StartZ=0 EndX=-2 EndY=10.8 EndZ=0
    g15: LineSegment StartX=-1.6 StartY=4.7 StartZ=0 EndX=-1.6 EndY=1.7 EndZ=0
    g16: LineSegment StartX=-1.6 StartY=4.7 StartZ=0 EndX=-2 EndY=4.7 EndZ=0
    g17: LineSegment StartX=-2 StartY=4.7 StartZ=0 EndX=-2 EndY=10.8 EndZ=0
  constraints (44):
    c: Vertical(g0)
    c: Vertical(g1)
    c: Distance(g1) = 0.9
    c: Block(g0)
    c: Distance(g0) = 1.7
    c: Weight(g2) = 1
    c: Equal(g2,g3)
    c: Equal(g2,g4)
    c: Coincident(g5,g1)
    c: InternalAlignment(g2,g5)
    c: InternalAlignment(g3,g5)
    c: InternalAlignment(g4,g5)
    c: InternalAlignment(g6,g5)
    c: InternalAlignment(g7,g5)
    c: Block(g5)
    c: Coincident(g8,g1)
    c: Vertical(g8)
    c: Distance(g8) = 7
    c: Vertical(g9)
    c: Equal(g8,g9) = 7
    c: Coincident(g9,g0)
    c: Coincident(g10,g8)
    c: Coincident(g10,g9)
    c: Horizontal(g10)
    c: Coincident(g11,g5)
    c: Horizontal(g11)
    c: Coincident(g12,g0)
    c: Vertical(g12)
    c: Distance(g12) = 2.8
    c: Coincident(g13,g12)
    c: Vertical(g13)
    c: Distance(g13) = 6.3
    c: Coincident(g14,g13)
    c: Horizontal(g14)
    c: Distance(g14) = 2
    c: Vertical(g15)
    c: Distance(g15) = 3
    c: Block(g11)
    c: Coincident(g15,g11)
    c: Coincident(g16,g15)
    c: Horizontal(g16)
    c: Coincident(g17,g16)
    c: Coincident(g17,g14)
    c: Vertical(g17)
FEATURE [Part::Revolution] Revolve040  label="backCaseScrewRetainer001"
  Angle = 360
  Axis = (0,1,0)
  Base = (0,0,0)
  FaceMakerClass = Part::FaceMakerBullseye
  Placement = pos=(12.5,3,10) rot=(0,0,1;0rad)
  Solid = false
  Source = -> Face036
  Symmetric = false
FEATURE [Part::Feature] Face055
  shape: bbox 3.5 x 30.2 x 2e-07 mm, 1 faces, 0 solids (baked)
FEATURE [Part::Revolution] Revolve059  label="backCaseScrewPost"
  Angle = 360
  Axis = (0,1,0)
  Base = (0,0,0)
  FaceMakerClass = Part::FaceMakerBullseye
  Placement = pos=(12.5,4.5,10) rot=(0,0,1;0rad)
  Solid = false
  Source = -> Face055
  Symmetric = false
FEATURE [Part::Feature] Face056
  shape: bbox 3.5 x 30.2 x 2e-07 mm, 1 faces, 0 solids (baked)
FEATURE [Part::Revolution] Revolve060  label="backCaseScrewPost001"
  Angle = 360
  Axis = (0,1,0)
  Base = (0,0,0)
  FaceMakerClass = Part::FaceMakerBullseye
  Placement = pos=(12.5,4.5,62) rot=(0,0,1;0rad)
  Solid = false
  Source = -> Face056
  Symmetric = false
FEATURE [Part::Feature] Face057
  shape: bbox 3.5 x 17.8 x 2e-07 mm, 1 faces, 0 solids (baked)
FEATURE [Part::Revolution] Revolve061  label="removeToCreateScrewAndThreadedInsertHole"
  Angle = 360
  Axis = (0,1,0)
  Base = (0,0,0)
  FaceMakerClass = Part::FaceMakerBullseye
  Placement = pos=(12.5,0,10) rot=(0,0,1;0rad)
  Solid = false
  Source = -> Face057
  Symmetric = false
FEATURE [Part::Feature] Face058
  shape: bbox 3.5 x 17.8 x 2e-07 mm, 1 faces, 0 solids (baked)
FEATURE [Part::Revolution] Revolve062  label="removeToCreateScrewAndThreadedInsertHole001"
  Angle = 360
  Axis = (0,1,0)
  Base = (0,0,0)
  FaceMakerClass = Part::FaceMakerBullseye
  Placement = pos=(12.5,0,62) rot=(0,0,1;0rad)
  Solid = false
  Source = -> Face058
  Symmetric = false
FEATURE [Part::Feature] Face059
  shape: bbox 3.5 x 17.8 x 2e-07 mm, 1 faces, 0 solids (baked)
FEATURE [Part::Revolution] Revolve063  label="removeToCreateScrewAndThreadedInsertHole002"
  Angle = 360
  Axis = (0,1,0)
  Base = (0,0,0)
  FaceMakerClass = Part::FaceMakerBullseye
  Placement = pos=(89.5,0,68.5) rot=(0,0,1;0rad)
  Solid = false
  Source = -> Face059
  Symmetric = false
FEATURE [Part::Feature] Face060
  shape: bbox 3.5 x 17.8 x 2e-07 mm, 1 faces, 0 solids (baked)
FEATURE [Part::Revolution] Revolve064  label="removeToCreateScrewAndThreadedInsertHole003"
  Angle = 360
  Axis = (0,1,0)
  Base = (0,0,0)
  FaceMakerClass = Part::FaceMakerBullseye
  Placement = pos=(89.5,0,3.5) rot=(0,0,1;0rad)
  Solid = false
  Source = -> Face060
  Symmetric = false
FEATURE [Part::Feature] Face061
  shape: bbox 3.5 x 17.8 x 2e-07 mm, 1 faces, 0 solids (baked)
FEATURE [Part::Revolution] Revolve065  label="removeToCreateScrewAndThreadedInsertHole004"
  Angle = 360
  Axis = (0,1,0)
  Base = (0,0,0)
  FaceMakerClass = Part::FaceMakerBullseye
  Placement = pos=(102.5,4.7,3.5) rot=(0,0,1;0rad)
  Solid = false
  Source = -> Face061
  Symmetric = false
FEATURE [Part::Feature] Face062
  shape: bbox 3.5 x 17.8 x 2e-07 mm, 1 faces, 0 solids (baked)
FEATURE [Part::Revolution] Revolve066  label="removeToCreateScrewAndThreadedInsertHole005"
  Angle = 360
  Axis = (0,1,0)
  Base = (0,0,0)
  FaceMakerClass = Part::FaceMakerBullseye
  Placement = pos=(102.5,4.7,68.5) rot=(0,0,1;0rad)
  Solid = false
  Source = -> Face062
  Symmetric = false
FEATURE [Part::MultiFuse] Fusion047  label="makeHoles"
  Shapes = -> [Revolve066,Revolve065,Revolve064,Revolve063,Revolve062,Revolve061]
FEATURE [Part::Feature] Face063
  shape: bbox 3.6 x 3.2 x 2e-07 mm, 1 faces, 0 solids (baked)
FEATURE [Part::Revolution] Revolve067  label="moreFrontCaseScrewRetainer002"
  Angle = 360
  Axis = (0,1,0)
  Base = (0,0,0)
  FaceMakerClass = Part::FaceMakerBullseye
  Placement = pos=(102.5,4.5,68.5) rot=(0,0,1;0rad)
  Solid = false
  Source = -> Face063
  Symmetric = false
FEATURE [Part::Feature] Face064
  shape: bbox 3.6 x 3.2 x 2e-07 mm, 1 faces, 0 solids (baked)
FEATURE [Part::Revolution] Revolve068  label="moreFrontCaseScrewRetainer003"
  Angle = 360
  Axis = (0,1,0)
  Base = (0,0,0)
  FaceMakerClass = Part::FaceMakerBullseye
  Placement = pos=(102.5,4.5,3.5) rot=(0,0,1;0rad)
  Solid = false
  Source = -> Face064
  Symmetric = false
FEATURE [Part::Feature] Face065
  shape: bbox 3.5 x 17.8 x 2e-07 mm, 1 faces, 0 solids (baked)
FEATURE [Part::Revolution] Revolve069  label="removeToCreateScrewAndThreadedInsertHole006"
  Angle = 360
  Axis = (0,1,0)
  Base = (0,0,0)
  FaceMakerClass = Part::FaceMakerBullseye
  Placement = pos=(12.5,0,10) rot=(0,0,1;0rad)
  Solid = false
  Source = -> Face065
  Symmetric = false
FEATURE [Part::Feature] Face066
  shape: bbox 3.5 x 17.8 x 2e-07 mm, 1 faces, 0 solids (baked)
FEATURE [Part::Revolution] Revolve070  label="removeToCreateScrewAndThreadedInsertHole007"
  Angle = 360
  Axis = (0,1,0)
  Base = (0,0,0)
  FaceMakerClass = Part::FaceMakerBullseye
  Placement = pos=(12.5,0,62) rot=(0,0,1;0rad)
  Solid = false
  Source = -> Face066
  Symmetric = false
FEATURE [Part::Feature] Face067
  shape: bbox 3.5 x 17.8 x 2e-07 mm, 1 faces, 0 solids (baked)
FEATURE [Part::Revolution] Revolve071  label="removeToCreateScrewAndThreadedInsertHole008"
  Angle = 360
  Axis = (0,1,0)
  Base = (0,0,0)
  FaceMakerClass = Part::FaceMakerBullseye
  Placement = pos=(89.5,0,68.5) rot=(0,0,1;0rad)
  Solid = false
  Source = -> Face067
  Symmetric = false
FEATURE [Part::Feature] Face068
  shape: bbox 3.5 x 17.8 x 2e-07 mm, 1 faces, 0 solids (baked)
FEATURE [Part::Revolution] Revolve072  label="removeToCreateScrewAndThreadedInsertHole009"
  Angle = 360
  Axis = (0,1,0)
  Base = (0,0,0)
  FaceMakerClass = Part::FaceMakerBullseye
  Placement = pos=(89.5,0,3.5) rot=(0,0,1;0rad)
  Solid = false
  Source = -> Face068
  Symmetric = false
FEATURE [Part::Feature] Face069
  shape: bbox 3.5 x 17.8 x 2e-07 mm, 1 faces, 0 solids (baked)
FEATURE [Part::Feature] Face070
  shape: bbox 3.5 x 17.8 x 2e-07 mm, 1 faces, 0 solids (baked)
FEATURE [Part::Revolution] Revolve073  label="removeToCreateScrewAndThreadedInsertHole010"
  Angle = 360
  Axis = (0,1,0)
  Base = (0,0,0)
  FaceMakerClass = Part::FaceMakerBullseye
  Placement = pos=(102.5,4.7,3.5) rot=(0,0,1;0rad)
  Solid = false
  Source = -> Face069
  Symmetric = false
FEATURE [Part::Revolution] Revolve074  label="removeToCreateScrewAndThreadedInsertHole011"
  Angle = 360
  Axis = (0,1,0)
  Base = (0,0,0)
  FaceMakerClass = Part::FaceMakerBullseye
  Placement = pos=(102.5,4.7,68.5) rot=(0,0,1;0rad)
  Solid = false
  Source = -> Face070
  Symmetric = false
FEATURE [Part::MultiFuse] Fusion048  label="makeHoles001"
  Shapes = -> [Revolve074,Revolve073,Revolve072,Revolve071,Revolve070,Revolve069]
FEATURE [Part::MultiFuse] Fusion049  label="caseScrewRetainers"
  Shapes = -> [Revolve067,Revolve068,Revolve048,Revolve047,Revolve039,Revolve040]
FEATURE [Part::Cut] Cut015  label="caseScrewRetainers001"
  Base = -> Fusion049
  Tool = -> Fusion048
FEATURE [Part::MultiFuse] Fusion050  label="casePillars"
  Shapes = -> [Revolve055,Revolve054,Revolve043,Revolve046,Revolve059,Revolve060]
FEATURE [Part::Feature] Face071 .. Face076  x6 (patterned run collapsed; names and placements below)
  shape: bbox 3.5 x 17.8 x 2e-07 mm, 1 faces, 0 solids (baked)
FEATURE [Part::Revolution] Revolve075  label="removeToCreateScrewAndThreadedInsertHole012"
  Angle = 360
  Axis = (0,1,0)
  Base = (0,0,0)
  FaceMakerClass = Part::FaceMakerBullseye
  Placement = pos=(12.5,0,10) rot=(0,0,1;0rad)
  Solid = false
  Source = -> Face071
  Symmetric = false
FEATURE [Part::Revolution] Revolve076  label="removeToCreateScrewAndThreadedInsertHole013"
  Angle = 360
  Axis = (0,1,0)
  Base = (0,0,0)
  FaceMakerClass = Part::FaceMakerBullseye
  Placement = pos=(12.5,0,62) rot=(0,0,1;0rad)
  Solid = false
  Source = -> Face072
  Symmetric = false
FEATURE [Part::Revolution] Revolve077  label="removeToCreateScrewAndThreadedInsertHole014"
  Angle = 360
  Axis = (0,1,0)
  Base = (0,0,0)
  FaceMakerClass = Part::FaceMakerBullseye
  Placement = pos=(89.5,0,68.5) rot=(0,0,1;0rad)
  Solid = false
  Source = -> Face073
  Symmetric = false
FEATURE [Part::Revolution] Revolve078  label="removeToCreateScrewAndThreadedInsertHole015"
  Angle = 360
  Axis = (0,1,0)
  Base = (0,0,0)
  FaceMakerClass = Part::FaceMakerBullseye
  Placement = pos=(89.5,0,3.5) rot=(0,0,1;0rad)
  Solid = false
  Source = -> Face074
  Symmetric = false
FEATURE [Part::Revolution] Revolve079  label="removeToCreateScrewAndThreadedInsertHole016"
  Angle = 360
  Axis = (0,1,0)
  Base = (0,0,0)
  FaceMakerClass = Part::FaceMakerBullseye
  Placement = pos=(102.5,4.7,3.5) rot=(0,0,1;0rad)
  Solid = false
  Source = -> Face075
  Symmetric = false
FEATURE [Part::Revolution] Revolve080  label="removeToCreateScrewAndThreadedInsertHole017"
  Angle = 360
  Axis = (0,1,0)
  Base = (0,0,0)
  FaceMakerClass = Part::FaceMakerBullseye
  Placement = pos=(102.5,4.7,68.5) rot=(0,0,1;0rad)
  Solid = false
  Source = -> Face076
  Symmetric = false
FEATURE [Part::MultiFuse] Fusion051  label="makeHoles002"
  Shapes = -> [Revolve080,Revolve079,Revolve078,Revolve077,Revolve076,Revolve075]
FEATURE [Part::Cut] Cut016  label="caesPillars"
  Base = -> Fusion050
  Tool = -> Fusion051
FEATURE [Part::Revolution] Revolve009  label="plugHousing016"
  Angle = 360
  Axis = (0,1,0)
  Base = (0,0,0)
  FaceMakerClass = Part::FaceMakerBullseye
  Placement = pos=(0,0,36.15) rot=(0,0,1;0rad)
  Solid = false
  Source = -> Face012
  Symmetric = false
FEATURE [Part::MultiFuse] Fusion014  label="plugHousing023"
  Placement = pos=(0,0,0) rot=(0,0,1;1.5708rad)
  Shapes = -> [Revolve011,Revolve009]
FEATURE [Part::Revolution] Revolve010  label="plugHousing017"
  Angle = 360
  Axis = (0,1,0)
  Base = (0,0,0)
  FaceMakerClass = Part::FaceMakerBullseye
  Placement = pos=(0,0,36.15) rot=(0,0,1;0rad)
  Solid = false
  Source = -> Face014
  Symmetric = false
FEATURE [Part::MultiFuse] Fusion015  label="plugHousing024"
  Placement = pos=(0,0,0) rot=(0,0,1;1.5708rad)
  Shapes = -> [Revolve010,Revolve015]
FEATURE [Part::Revolution] Revolve014  label="plugHousing026"
  Angle = 360
  Axis = (0,1,0)
  Base = (0,0,0)
  FaceMakerClass = Part::FaceMakerBullseye
  Placement = pos=(0,0,36.15) rot=(0,0,1;0rad)
  Solid = false
  Source = -> Face011
  Symmetric = false
FEATURE [Part::Revolution] Revolve013  label="plugHousing025"
  Angle = 360
  Axis = (0,1,0)
  Base = (0,0,0)
  FaceMakerClass = Part::FaceMakerBullseye
  Placement = pos=(0,0,36.15) rot=(0,0,1;0rad)
  Solid = false
  Source = -> Face015
  Symmetric = false
FEATURE [Part::MultiFuse] Fusion016  label="plugHousing028"
  Placement = pos=(0,19,0) rot=(0,0,1;3.14159rad)
  Shapes = -> [Fusion014,Fusion013]
FEATURE [Part::MultiFuse] Fusion011  label="plugHousing018"
  Placement = pos=(0,0,0) rot=(0,0,1;1.5708rad)
  Shapes = -> [Revolve014,Revolve013]
FEATURE [Part::MultiFuse] Fusion012  label="plugHousing019"
  Placement = pos=(0,19,0) rot=(0,0,1;3.14159rad)
  Shapes = -> [Fusion011,Fusion015]
FEATURE [Part::MultiFuse] Fusion017  label="plugHousing029"
  Placement = pos=(122.621,0,-0.15) rot=(0,0,1;0rad)
  Shapes = -> [Fusion016,Fusion012]
FEATURE [Part::MultiFuse] Fusion052  label="casePillarRetainers"
  Shapes = -> [Extrude012,Extrude013,Extrude014,Extrude015,Extrude016,Extrude017,Extrude018,Extrude019,Box011,Box012]
FEATURE [Part::Feature] Face077
  shape: bbox 3.5 x 17.8 x 2e-07 mm, 1 faces, 0 solids (baked)
FEATURE [Part::Revolution] Revolve081  label="removeToCreateScrewAndThreadedInsertHole018"
  Angle = 360
  Axis = (0,1,0)
  Base = (0,0,0)
  FaceMakerClass = Part::FaceMakerBullseye
  Placement = pos=(62.3,30.3,19.7) rot=(0,0,1;0rad)
  Solid = false
  Source = -> Face077
  Symmetric = false
FEATURE [Part::Feature] Face078
  shape: bbox 3.5 x 17.8 x 2e-07 mm, 1 faces, 0 solids (baked)
FEATURE [Part::Revolution] Revolve082  label="removeToCreateScrewAndThreadedInsertHole019"
  Angle = 360
  Axis = (0,1,0)
  Base = (0,0,0)
  FaceMakerClass = Part::FaceMakerBullseye
  Placement = pos=(62.3,30.3,51.7) rot=(0,0,1;0rad)
  Solid = false
  Source = -> Face078
  Symmetric = false
FEATURE [Part::Feature] Face079
  shape: bbox 3.5 x 17.8 x 2e-07 mm, 1 faces, 0 solids (baked)
FEATURE [Part::Revolution] Revolve083  label="removeToCreateScrewAndThreadedInsertHole020"
  Angle = 360
  Axis = (0,1,0)
  Base = (0,0,0)
  FaceMakerClass = Part::FaceMakerBullseye
  Placement = pos=(30.3,30.3,19.7) rot=(0,0,1;0rad)
  Solid = false
  Source = -> Face079
  Symmetric = false
FEATURE [Part::Feature] Face080
  shape: bbox 3.5 x 17.8 x 2e-07 mm, 1 faces, 0 solids (baked)
FEATURE [Part::Revolution] Revolve084  label="removeToCreateScrewAndThreadedInsertHole021"
  Angle = 360
  Axis = (0,1,0)
  Base = (0,0,0)
  FaceMakerClass = Part::FaceMakerBullseye
  Placement = pos=(30.3,30.3,51.7) rot=(0,0,1;0rad)
  Solid = false
  Source = -> Face080
  Symmetric = false
FEATURE [Part::MultiFuse] Fusion053  label="createThreadedInsertHolesForFan"
  Shapes = -> [Revolve081,Revolve082,Revolve083,Revolve084]
FEATURE [Part::Cut] Cut017  label="fanScrewHousing001"
  Base = -> Fusion046
  Tool = -> Fusion053
FEATURE [Part::Feature] Face081
  shape: bbox 3.5 x 17.8 x 2e-07 mm, 1 faces, 0 solids (baked)
FEATURE [Part::Revolution] Revolve085  label="removeToCreateScrewAndThreadedInsertHole022"
  Angle = 360
  Axis = (0,1,0)
  Base = (0,0,0)
  FaceMakerClass = Part::FaceMakerBullseye
  Placement = pos=(62.3,30.3,19.7) rot=(0,0,1;0rad)
  Solid = false
  Source = -> Face081
  Symmetric = false
FEATURE [Part::Feature] Face082
  shape: bbox 3.5 x 17.8 x 2e-07 mm, 1 faces, 0 solids (baked)
FEATURE [Part::Revolution] Revolve086  label="removeToCreateScrewAndThreadedInsertHole023"
  Angle = 360
  Axis = (0,1,0)
  Base = (0,0,0)
  FaceMakerClass = Part::FaceMakerBullseye
  Placement = pos=(62.3,30.3,51.7) rot=(0,0,1;0rad)
  Solid = false
  Source = -> Face082
  Symmetric = false
FEATURE [Part::Feature] Face083
  shape: bbox 3.5 x 17.8 x 2e-07 mm, 1 faces, 0 solids (baked)
FEATURE [Part::Revolution] Revolve087  label="removeToCreateScrewAndThreadedInsertHole024"
  Angle = 360
  Axis = (0,1,0)
  Base = (0,0,0)
  FaceMakerClass = Part::FaceMakerBullseye
  Placement = pos=(30.3,30.3,19.7) rot=(0,0,1;0rad)
  Solid = false
  Source = -> Face083
  Symmetric = false
FEATURE [Part::Feature] Face084
  shape: bbox 3.5 x 17.8 x 2e-07 mm, 1 faces, 0 solids (baked)
FEATURE [Part::Revolution] Revolve088  label="removeToCreateScrewAndThreadedInsertHole025"
  Angle = 360
  Axis = (0,1,0)
  Base = (0,0,0)
  FaceMakerClass = Part::FaceMakerBullseye
  Placement = pos=(30.3,30.3,51.7) rot=(0,0,1;0rad)
  Solid = false
  Source = -> Face084
  Symmetric = false
FEATURE [Part::MultiFuse] Fusion054  label="createThreadedInsertHolesForFan001"
  Shapes = -> [Revolve085,Revolve086,Revolve087,Revolve088]
FEATURE [Part::Cut] Cut018  label="top007"
  Base = -> Fusion040
  Tool = -> Fusion054
FEATURE [Sketcher::SketchObject] Sketch029
  FullyConstrained = false
  Placement = pos=(0,0,0) rot=(1,0,0;1.5708rad)
  sketch-geometry (24):
    g0: ArcOfCircle CenterX=-4 CenterY=-10.5 CenterZ=0 NormalX=0 NormalY=0 NormalZ=1 AngleXU=0 Radius=1.5 StartAngle=6e-16 EndAngle=3.14159
    g1: ArcOfCircle CenterX=-34.2 CenterY=-10.5 CenterZ=0 NormalX=0 NormalY=0 NormalZ=1 AngleXU=0 Radius=1.5 StartAngle=0 EndAngle=3.14159
    g2: ArcOfCircle CenterX=-34.2 CenterY=-27.7 CenterZ=0 NormalX=0 NormalY=0 NormalZ=1 AngleXU=0 Radius=1.5 StartAngle=3.14159 EndAngle=6.28319
    g3: ArcOfCircle CenterX=-4 CenterY=-27.7 CenterZ=0 NormalX=0 NormalY=0 NormalZ=1 AngleXU=0 Radius=1.5 StartAngle=3.1416 EndAngle=6.28319
    g4: ArcOfCircle CenterX=-10 CenterY=-4.3 CenterZ=0 NormalX=0 NormalY=0 NormalZ=1 AngleXU=0 Radius=1.5 StartAngle=2e-16 EndAngle=3.14159
    g5: ArcOfCircle CenterX=-16.1 CenterY=-1.8 CenterZ=0 NormalX=0 NormalY=0 NormalZ=1 AngleXU=0 Radius=1.5 StartAngle=5e-16 EndAngle=3.14159
    g6: ArcOfCircle CenterX=-22.1 CenterY=-1.8 CenterZ=0 NormalX=0 NormalY=0 NormalZ=1 AngleXU=0 Radius=1.5 StartAngle=5e-16 EndAngle=3.14159
    g7: ArcOfCircle CenterX=-28.2 CenterY=-4.3 CenterZ=0 NormalX=0 NormalY=0 NormalZ=1 AngleXU=0 Radius=1.5 StartAngle=2e-16 EndAngle=3.14159
    g8: ArcOfCircle CenterX=-10 CenterY=-33.9 CenterZ=0 NormalX=0 NormalY=0 NormalZ=1 AngleXU=0 Radius=1.5 StartAngle=3.14159 EndAngle=6.28319
    g9: ArcOfCircle CenterX=-16.1 CenterY=-36.4 CenterZ=0 NormalX=0 NormalY=0 NormalZ=1 AngleXU=0 Radius=1.5 StartAngle=3.14159 EndAngle=6.28319
    g10: ArcOfCircle CenterX=-22.1 CenterY=-36.4 CenterZ=0 NormalX=0 NormalY=0 NormalZ=1 AngleXU=0 Radius=1.5 StartAngle=3.14159 EndAngle=6.28319
    g11: ArcOfCircle CenterX=-28.2 CenterY=-33.9 CenterZ=0 NormalX=0 NormalY=0 NormalZ=1 AngleXU=0 Radius=1.5 StartAngle=3.14159 EndAngle=6.28319
    g12: LineSegment StartX=-35.7 StartY=-10.5 StartZ=0 EndX=-35.7 EndY=-27.7 EndZ=0
    g13: LineSegment StartX=-32.7 StartY=-10.5 StartZ=0 EndX=-32.7 EndY=-27.7 EndZ=0
    g14: LineSegment StartX=-29.7 StartY=-33.9 StartZ=0 EndX=-29.7 EndY=-4.3 EndZ=0
    g15: LineSegment StartX=-26.7 StartY=-33.9 StartZ=0 EndX=-26.7 EndY=-4.3 EndZ=0
    g16: LineSegment StartX=-2.5 StartY=-10.5 StartZ=0 EndX=-2.5 EndY=-27.7 EndZ=0
    g17: LineSegment StartX=-8.5 StartY=-4.3 StartZ=0 EndX=-8.5 EndY=-33.9 EndZ=0
    g18: LineSegment StartX=-5.5 StartY=-10.5 StartZ=0 EndX=-5.5 EndY=-27.7 EndZ=0
    g19: LineSegment StartX=-11.5 StartY=-4.3 StartZ=0 EndX=-11.5 EndY=-33.9 EndZ=0
    g20: LineSegment StartX=-14.6 StartY=-1.8 StartZ=0 EndX=-14.6 EndY=-36.4 EndZ=0
    g21: LineSegment StartX=-17.6 StartY=-1.8 StartZ=0 EndX=-17.6 EndY=-36.4 EndZ=0
    g22: LineSegment StartX=-20.6 StartY=-36.4 StartZ=0 EndX=-20.6 EndY=-1.8 EndZ=0
    g23: LineSegment StartX=-23.6 StartY=-1.8 StartZ=0 EndX=-23.6 EndY=-36.4 EndZ=0
  constraints (48):
    c: Block(g0)
    c: Block(g1)
    c: Block(g2)
    c: Block(g3)
    c: Block(g4)
    c: Block(g5)
    c: Block(g6)
    c: Block(g7)
    c: Block(g8)
    c: Block(g9)
    c: Block(g10)
    c: Block(g11)
    c: Coincident(g12,g1)
    c: Coincident(g12,g2)
    c: Vertical(g12)
    c: Coincident(g13,g1)
    c: Coincident(g13,g2)
    c: Vertical(g13)
    c: Coincident(g14,g11)
    c: Coincident(g14,g7)
    c: Vertical(g14)
    c: Coincident(g15,g11)
    c: Coincident(g15,g7)
    c: Vertical(g15)
    c: Coincident(g16,g0)
    c: Coincident(g16,g3)
    c: Vertical(g16)
    c: Coincident(g17,g4)
    c: Coincident(g17,g8)
    c: Vertical(g17)
    c: Coincident(g18,g0)
    c: Coincident(g18,g3)
    c: Vertical(g18)
    c: Coincident(g19,g4)
    c: Coincident(g19,g8)
    c: Vertical(g19)
    c: Coincident(g20,g5)
    c: Coincident(g20,g9)
    c: Vertical(g20)
    c: Coincident(g21,g5)
    c: Coincident(g21,g9)
    c: Vertical(g21)
    c: Coincident(g22,g10)
    c: Coincident(g22,g6)
    c: Vertical(g22)
    c: Coincident(g23,g6)
    c: Coincident(g23,g10)
    c: Vertical(g23)
FEATURE [Part::Extrusion] Extrude020  label="removeToCreateFanGrillHoles"
  Base = -> Sketch029
  Dir = (0,-1,6e-16)
  DirMode = 2
  FaceMakerClass = Part::FaceMakerBullseye
  LengthFwd = 10
  LengthRev = 0
  Placement = pos=(65.4,44,54.82) rot=(0,0,1;0rad)
  Solid = true
  Symmetric = false
FEATURE [Part::MultiFuse] Fusion055  label="top008"
  Shapes = -> [Cut017,Cut018]
FEATURE [Part::Cut] Cut019  label="top009"
  Base = -> Fusion055
  Tool = -> Extrude020
FEATURE [App::MeasureDistance] Distance003  label="Distance: 71.95 mm"
  Distance = 71.9513
  P1 = (117,38,72)
  P2 = (117,38,0.0487319)
FEATURE [Sketcher::SketchObject] Sketch030
  FullyConstrained = true
  Placement = pos=(117,19,0) rot=(0.57735,0.57735,0.57735;2.0944rad)
  sketch-geometry (48):
    g0: LineSegment StartX=-49.19 StartY=69.25 StartZ=0 EndX=-49.19 EndY=66.25 EndZ=0
    g1: LineSegment StartX=-49.19 StartY=63.5 StartZ=0 EndX=-49.19 EndY=60.5 EndZ=0
    g2: LineSegment StartX=-49.19 StartY=57.75 StartZ=0 EndX=-49.19 EndY=54.75 EndZ=0
    g3: LineSegment StartX=-49.19 StartY=52 StartZ=0 EndX=-49.19 EndY=49 EndZ=0
    g4: LineSegment StartX=-49.19 StartY=46.25 StartZ=0 EndX=-49.19 EndY=43.25 EndZ=0
    g5: LineSegment StartX=-49.19 StartY=40.5 StartZ=0 EndX=-49.19 EndY=37.5 EndZ=0
    g6: LineSegment StartX=-49.19 StartY=34.5 StartZ=0 EndX=-49.19 EndY=31.5 EndZ=0
    g7: LineSegment StartX=-49.19 StartY=28.75 StartZ=0 EndX=-49.19 EndY=25.75 EndZ=0
    g8: LineSegment StartX=-49.19 StartY=23 StartZ=0 EndX=-49.19 EndY=20 EndZ=0
    g9: LineSegment StartX=-49.19 StartY=17.25 StartZ=0 EndX=-49.19 EndY=14.25 EndZ=0
    g10: LineSegment StartX=-49.19 StartY=11.5 StartZ=0 EndX=-49.19 EndY=8.5 EndZ=0
    g11: LineSegment StartX=-49.19 StartY=5.75 StartZ=0 EndX=-49.19 EndY=2.75 EndZ=0
    g12: ArcOfCircle CenterX=-1.5 CenterY=67.75 CenterZ=0 NormalX=0 NormalY=0 NormalZ=1 AngleXU=0 Radius=1.5 StartAngle=4.71239 EndAngle=7.85398
    g13: ArcOfCircle CenterX=-1.5 CenterY=62 CenterZ=0 NormalX=0 NormalY=0 NormalZ=1 AngleXU=0 Radius=1.5 StartAngle=4.71239 EndAngle=7.85398
    g14: ArcOfCircle CenterX=-1.5 CenterY=56.25 CenterZ=0 NormalX=0 NormalY=0 NormalZ=1 AngleXU=0 Radius=1.5 StartAngle=4.71239 EndAngle=7.85398
    g15: ArcOfCircle CenterX=-11.49 CenterY=50.5 CenterZ=0 NormalX=0 NormalY=0 NormalZ=1 AngleXU=0 Radius=1.5 StartAngle=4.71239 EndAngle=7.85398
    g16: ArcOfCircle CenterX=-16.28 CenterY=44.75 CenterZ=0 NormalX=0 NormalY=0 NormalZ=1 AngleXU=0 Radius=1.5 StartAngle=4.71239 EndAngle=7.85398
    g17: ArcOfCircle CenterX=-18.2337 CenterY=39 CenterZ=0 NormalX=0 NormalY=0 NormalZ=1 AngleXU=0 Radius=1.5 StartAngle=4.71485 EndAngle=7.85398
    g18: ArcOfCircle CenterX=-16.2837 CenterY=27.25 CenterZ=0 NormalX=0 NormalY=0 NormalZ=1 AngleXU=0 Radius=1.5 StartAngle=4.71485 EndAngle=7.85398
    g19: ArcOfCircle CenterX=-18.2337 CenterY=33 CenterZ=0 NormalX=0 NormalY=0 NormalZ=1 AngleXU=0 Radius=1.5 StartAngle=4.71485 EndAngle=7.85398
    g20: ArcOfCircle CenterX=-11.49 CenterY=21.5 CenterZ=0 NormalX=0 NormalY=0 NormalZ=1 AngleXU=0 Radius=1.5 StartAngle=4.71239 EndAngle=7.85398
    g21: ArcOfCircle CenterX=-1.5 CenterY=4.25 CenterZ=0 NormalX=0 NormalY=0 NormalZ=1 AngleXU=0 Radius=1.5 StartAngle=4.71239 EndAngle=7.85398
    g22: ArcOfCircle CenterX=-1.5 CenterY=10 CenterZ=0 NormalX=0 NormalY=0 NormalZ=1 AngleXU=0 Radius=1.5 StartAngle=4.71239 EndAngle=7.85398
    g23: ArcOfCircle CenterX=-1.5 CenterY=15.75 CenterZ=0 NormalX=0 NormalY=0 NormalZ=1 AngleXU=0 Radius=1.5 StartAngle=4.71239 EndAngle=7.85398
    g24: LineSegment StartX=-49.19 StartY=69.25 StartZ=0 EndX=-1.5 EndY=69.25 EndZ=0
    g25: LineSegment StartX=-49.19 StartY=66.25 StartZ=0 EndX=-1.5 EndY=66.25 EndZ=0
    g26: LineSegment StartX=-49.19 StartY=63.5 StartZ=0 EndX=-1.5 EndY=63.5 EndZ=0
    g27: LineSegment StartX=-49.19 StartY=60.5 StartZ=0 EndX=-1.5 EndY=60.5 EndZ=0
    g28: LineSegment StartX=-49.19 StartY=57.75 StartZ=0 EndX=-1.5 EndY=57.75 EndZ=0
    g29: LineSegment StartX=-49.19 StartY=54.75 StartZ=0 EndX=-1.5 EndY=54.75 EndZ=0
    g30: LineSegment StartX=-49.19 StartY=52 StartZ=0 EndX=-11.49 EndY=52 EndZ=0
    g31: LineSegment StartX=-49.19 StartY=49 StartZ=0 EndX=-11.49 EndY=49 EndZ=0
    g32: LineSegment StartX=-49.19 StartY=46.25 StartZ=0 EndX=-16.28 EndY=46.25 EndZ=0
    g33: LineSegment StartX=-49.19 StartY=43.25 StartZ=0 EndX=-16.28 EndY=43.25 EndZ=0
    g34: LineSegment StartX=-49.19 StartY=40.5 StartZ=0 EndX=-18.2337 EndY=40.5 EndZ=0
    g35: LineSegment StartX=-49.19 StartY=37.5 StartZ=0 EndX=-18.23 EndY=37.5 EndZ=0
    g36: LineSegment StartX=-49.19 StartY=34.5 StartZ=0 EndX=-18.2337 EndY=34.5 EndZ=0
    g37: LineSegment StartX=-49.19 StartY=31.5 StartZ=0 EndX=-18.23 EndY=31.5 EndZ=0
    g38: LineSegment StartX=-49.19 StartY=28.75 StartZ=0 EndX=-16.2837 EndY=28.75 EndZ=0
    g39: LineSegment StartX=-49.19 StartY=25.75 StartZ=0 EndX=-16.28 EndY=25.75 EndZ=0
    g40: LineSegment StartX=-49.19 StartY=23 StartZ=0 EndX=-11.49 EndY=23 EndZ=0
    g41: LineSegment StartX=-49.19 StartY=20 StartZ=0 EndX=-11.49 EndY=20 EndZ=0
    g42: LineSegment StartX=-49.19 StartY=17.25 StartZ=0 EndX=-1.5 EndY=17.25 EndZ=0
    g43: LineSegment StartX=-49.19 StartY=14.25 StartZ=0 EndX=-1.5 EndY=14.25 EndZ=0
    g44: LineSegment StartX=-49.19 StartY=11.5 StartZ=0 EndX=-1.5 EndY=11.5 EndZ=0
    g45: LineSegment StartX=-49.19 StartY=8.5 StartZ=0 EndX=-1.5 EndY=8.5 EndZ=0
    g46: LineSegment StartX=-49.19 StartY=5.75 StartZ=0 EndX=-1.5 EndY=5.75 EndZ=0
    g47: LineSegment StartX=-49.19 StartY=2.75 StartZ=0 EndX=-1.5 EndY=2.75 EndZ=0
  constraints (120):
    c: Vertical(g0)
    c: Distance(g0) = 3
    c: Block(g0)
    c: Vertical(g1)
    c: Distance(g1) = 3
    c: Vertical(g2)
    c: Equal(g0,g2) = 3
    c: Block(g2)
    c: Vertical(g3)
    c: Equal(g1,g3) = 3
    c: Vertical(g4)
    c: Equal(g0,g4) = 3
    c: Block(g4)
    c: Vertical(g5)
    c: Equal(g1,g5) = 3
    c: Vertical(g6)
    c: Equal(g0,g6) = 3
    c: Block(g6)
    c: Vertical(g7)
    c: Equal(g1,g7) = 3
    c: Vertical(g8)
    c: Equal(g0,g8) = 3
    c: Block(g8)
    c: Vertical(g9)
    c: Equal(g1,g9) = 3
    c: Vertical(g10)
    c: Equal(g0,g10) = 3
    c: Block(g10)
    c: Vertical(g11)
    c: Equal(g1,g11) = 3
    c: Block(g12)
    c: Block(g13)
    c: Block(g14)
    c: Block(g15)
    c: Block(g16)
    c: Block(g17)
    c: Block(g18)
    c: Block(g19)
    c: Block(g20)
    c: Block(g21)
    c: Block(g22)
    c: Block(g23)
    c: Block(g11)
    c: Block(g9)
    c: Block(g7)
    c: Block(g5)
    c: Block(g3)
    c: Block(g1)
    c: Coincident(g24,g0)
    c: Coincident(g24,g12)
    c: Horizontal(g24)
    c: Coincident(g25,g0)
    c: Coincident(g25,g12)
    c: Horizontal(g25)
    c: Coincident(g26,g1)
    c: Coincident(g26,g13)
    c: Horizontal(g26)
    c: Coincident(g27,g1)
    c: Coincident(g27,g13)
    c: Horizontal(g27)
    c: Coincident(g28,g2)
    c: Coincident(g28,g14)
    c: Horizontal(g28)
    c: Coincident(g29,g2)
    c: Coincident(g29,g14)
    c: Horizontal(g29)
    c: Coincident(g30,g3)
    c: Coincident(g30,g15)
    c: Horizontal(g30)
    c: Coincident(g31,g3)
    c: Coincident(g31,g15)
    c: Horizontal(g31)
    c: Coincident(g32,g4)
    c: Coincident(g32,g16)
    c: Horizontal(g32)
    c: Coincident(g33,g4)
    c: Coincident(g33,g16)
    c: Horizontal(g33)
    c: Coincident(g34,g5)
    c: Coincident(g34,g17)
    c: Horizontal(g34)
    c: Coincident(g35,g5)
    c: Coincident(g35,g17)
    c: Horizontal(g35)
    c: Coincident(g36,g6)
    c: Coincident(g36,g19)
    c: Horizontal(g36)
    c: Coincident(g37,g6)
    c: Coincident(g37,g19)
    c: Horizontal(g37)
    c: Coincident(g38,g7)
    c: Coincident(g38,g18)
    c: Horizontal(g38)
    c: Coincident(g39,g7)
    c: Coincident(g39,g18)
    c: Horizontal(g39)
    c: Coincident(g40,g8)
    c: Coincident(g40,g20)
    c: Horizontal(g40)
    c: Coincident(g41,g8)
    c: Coincident(g41,g20)
    c: Horizontal(g41)
    c: Coincident(g42,g9)
    c: Coincident(g42,g23)
    c: Horizontal(g42)
    c: Coincident(g43,g9)
    c: Coincident(g43,g23)
    c: Horizontal(g43)
    c: Coincident(g44,g10)
    c: Coincident(g44,g22)
    c: Horizontal(g44)
    c: Coincident(g45,g10)
    c: Coincident(g45,g22)
    c: Horizontal(g45)
    c: Coincident(g46,g11)
    c: Coincident(g46,g21)
    c: Horizontal(g46)
    c: Coincident(g47,g11)
    c: Coincident(g47,g21)
    c: Horizontal(g47)
FEATURE [Sketcher::SketchObject] Sketch031
  FullyConstrained = true
  Placement = pos=(117,19,0) rot=(0.57735,0.57735,0.57735;2.0944rad)
  sketch-geometry (24):
    g0: ArcOfCircle CenterX=-49.19 CenterY=67.75 CenterZ=0 NormalX=0 NormalY=0 NormalZ=1 AngleXU=0 Radius=1.5 StartAngle=1.5708 EndAngle=4.71239
    g1: ArcOfCircle CenterX=-49.19 CenterY=62 CenterZ=0 NormalX=0 NormalY=0 NormalZ=1 AngleXU=0 Radius=1.5 StartAngle=1.5708 EndAngle=4.71239
    g2: ArcOfCircle CenterX=-49.19 CenterY=56.25 CenterZ=0 NormalX=0 NormalY=0 NormalZ=1 AngleXU=0 Radius=1.5 StartAngle=1.5708 EndAngle=4.71239
    g3: ArcOfCircle CenterX=-49.19 CenterY=50.5 CenterZ=0 NormalX=0 NormalY=0 NormalZ=1 AngleXU=0 Radius=1.5 StartAngle=1.5708 EndAngle=4.71239
    g4: ArcOfCircle CenterX=-49.19 CenterY=44.75 CenterZ=0 NormalX=0 NormalY=0 NormalZ=1 AngleXU=0 Radius=1.5 StartAngle=1.5708 EndAngle=4.71239
    g5: ArcOfCircle CenterX=-49.19 CenterY=39 CenterZ=0 NormalX=0 NormalY=0 NormalZ=1 AngleXU=0 Radius=1.5 StartAngle=1.5708 EndAngle=4.71239
    g6: ArcOfCircle CenterX=-49.19 CenterY=33 CenterZ=0 NormalX=0 NormalY=0 NormalZ=1 AngleXU=0 Radius=1.5 StartAngle=1.5708 EndAngle=4.71239
    g7: ArcOfCircle CenterX=-49.19 CenterY=27.25 CenterZ=0 NormalX=0 NormalY=0 NormalZ=1 AngleXU=0 Radius=1.5 StartAngle=1.5708 EndAngle=4.71239
    g8: ArcOfCircle CenterX=-49.19 CenterY=21.5 CenterZ=0 NormalX=0 NormalY=0 NormalZ=1 AngleXU=0 Radius=1.5 StartAngle=1.5708 EndAngle=4.71239
    g9: ArcOfCircle CenterX=-49.19 CenterY=15.75 CenterZ=0 NormalX=0 NormalY=0 NormalZ=1 AngleXU=0 Radius=1.5 StartAngle=1.5708 EndAngle=4.71239
    g10: ArcOfCircle CenterX=-49.19 CenterY=10 CenterZ=0 NormalX=0 NormalY=0 NormalZ=1 AngleXU=0 Radius=1.5 StartAngle=1.5708 EndAngle=4.71239
    g11: ArcOfCircle CenterX=-49.19 CenterY=4.25 CenterZ=0 NormalX=0 NormalY=0 NormalZ=1 AngleXU=0 Radius=1.5 StartAngle=1.5708 EndAngle=4.71239
    g12: LineSegment StartX=-49.19 StartY=69.25 StartZ=0 EndX=-49.19 EndY=66.25 EndZ=0
    g13: LineSegment StartX=-49.19 StartY=63.5 StartZ=0 EndX=-49.19 EndY=60.5 EndZ=0
    g14: LineSegment StartX=-49.19 StartY=57.75 StartZ=0 EndX=-49.19 EndY=54.75 EndZ=0
    g15: LineSegment StartX=-49.19 StartY=52 StartZ=0 EndX=-49.19 EndY=49 EndZ=0
    g16: LineSegment StartX=-49.19 StartY=46.25 StartZ=0 EndX=-49.19 EndY=43.25 EndZ=0
    g17: LineSegment StartX=-49.19 StartY=40.5 StartZ=0 EndX=-49.19 EndY=37.5 EndZ=0
    g18: LineSegment StartX=-49.19 StartY=34.5 StartZ=0 EndX=-49.19 EndY=31.5 EndZ=0
    g19: LineSegment StartX=-49.19 StartY=28.75 StartZ=0 EndX=-49.19 EndY=25.75 EndZ=0
    g20: LineSegment StartX=-49.19 StartY=23 StartZ=0 EndX=-49.19 EndY=20 EndZ=0
    g21: LineSegment StartX=-49.19 StartY=17.25 StartZ=0 EndX=-49.19 EndY=14.25 EndZ=0
    g22: LineSegment StartX=-49.19 StartY=11.5 StartZ=0 EndX=-49.19 EndY=8.5 EndZ=0
    g23: LineSegment StartX=-49.19 StartY=5.75 StartZ=0 EndX=-49.19 EndY=2.75 EndZ=0
  constraints (48):
    c: Block(g0)
    c: Block(g1)
    c: Block(g2)
    c: Block(g3)
    c: Block(g4)
    c: Block(g5)
    c: Block(g6)
    c: Block(g7)
    c: Block(g8)
    c: Block(g9)
    c: Block(g10)
    c: Block(g11)
    c: Coincident(g12,g0)
    c: Coincident(g12,g0)
    c: Vertical(g12)
    c: Vertical(g13)
    c: Coincident(g13,g1)
    c: Vertical(g14)
    c: Coincident(g14,g2)
    c: Vertical(g15)
    c: Coincident(g15,g3)
    c: Vertical(g16)
    c: Coincident(g16,g4)
    c: Vertical(g17)
    c: Coincident(g17,g5)
    c: Vertical(g18)
    c: Coincident(g18,g6)
    c: Vertical(g19)
    c: Coincident(g19,g7)
    c: Vertical(g20)
    c: Coincident(g20,g8)
    c: Vertical(g21)
    c: Coincident(g21,g9)
    c: Vertical(g22)
    c: Coincident(g22,g10)
    c: Vertical(g23)
    c: Coincident(g23,g11)
    c: Block(g23)
    c: Block(g22)
    c: Block(g21)
    c: Block(g20)
    c: Block(g13)
    c: Block(g14)
    c: Block(g15)
    c: Block(g16)
    c: Block(g17)
    c: Block(g18)
    c: Block(g19)
FEATURE [Part::Extrusion] Extrude022
  Base = -> Sketch030
  Dir = (1,-2e-16,2e-16)
  DirMode = 2
  FaceMakerClass = Part::FaceMakerBullseye
  LengthFwd = 19
  LengthRev = 0
  Placement = pos=(-19,0,0) rot=(0,0,1;0rad)
  Solid = true
  Symmetric = false
FEATURE [Part::Fillet] Fillet022
  Base = -> Extrude022
  Edges = 24 edges r=1.49: [Edge6,Edge11,Edge18,Edge23,Edge30,Edge35,Edge42,Edge47,Edge54,Edge59,Edge66,Edge71,Edge78,Edge83,Edge90,Edge95,Edge102,Edge107,Edge114,Edge119,Edge126,Edge131,Edge138,Edge143]
FEATURE [Part::Cut] Cut020  label="top010"
  Base = -> Cut019
  Tool = -> Fillet022
FEATURE [Sketcher::SketchObject] Sketch032
  FullyConstrained = true
  Placement = pos=(117,19,0) rot=(0.57735,0.57735,0.57735;2.0944rad)
  sketch-geometry (48):
    g0: LineSegment StartX=-49.19 StartY=69.25 StartZ=0 EndX=-49.19 EndY=66.25 EndZ=0
    g1: LineSegment StartX=-49.19 StartY=63.5 StartZ=0 EndX=-49.19 EndY=60.5 EndZ=0
    g2: LineSegment StartX=-49.19 StartY=57.75 StartZ=0 EndX=-49.19 EndY=54.75 EndZ=0
    g3: LineSegment StartX=-49.19 StartY=52 StartZ=0 EndX=-49.19 EndY=49 EndZ=0
    g4: LineSegment StartX=-49.19 StartY=46.25 StartZ=0 EndX=-49.19 EndY=43.25 EndZ=0
    g5: LineSegment StartX=-49.19 StartY=40.5 StartZ=0 EndX=-49.19 EndY=37.5 EndZ=0
    g6: LineSegment StartX=-49.19 StartY=34.5 StartZ=0 EndX=-49.19 EndY=31.5 EndZ=0
    g7: LineSegment StartX=-49.19 StartY=28.75 StartZ=0 EndX=-49.19 EndY=25.75 EndZ=0
    g8: LineSegment StartX=-49.19 StartY=23 StartZ=0 EndX=-49.19 EndY=20 EndZ=0
    g9: LineSegment StartX=-49.19 StartY=17.25 StartZ=0 EndX=-49.19 EndY=14.25 EndZ=0
    g10: LineSegment StartX=-49.19 StartY=11.5 StartZ=0 EndX=-49.19 EndY=8.5 EndZ=0
    g11: LineSegment StartX=-49.19 StartY=5.75 StartZ=0 EndX=-49.19 EndY=2.75 EndZ=0
    g12: ArcOfCircle CenterX=-1.5 CenterY=67.75 CenterZ=0 NormalX=0 NormalY=0 NormalZ=1 AngleXU=0 Radius=1.5 StartAngle=4.71239 EndAngle=7.85398
    g13: ArcOfCircle CenterX=-1.5 CenterY=62 CenterZ=0 NormalX=0 NormalY=0 NormalZ=1 AngleXU=0 Radius=1.5 StartAngle=4.71239 EndAngle=7.85398
    g14: ArcOfCircle CenterX=-1.5 CenterY=56.25 CenterZ=0 NormalX=0 NormalY=0 NormalZ=1 AngleXU=0 Radius=1.5 StartAngle=4.71239 EndAngle=7.85398
    g15: ArcOfCircle CenterX=-11.49 CenterY=50.5 CenterZ=0 NormalX=0 NormalY=0 NormalZ=1 AngleXU=0 Radius=1.5 StartAngle=4.71239 EndAngle=7.85398
    g16: ArcOfCircle CenterX=-16.28 CenterY=44.75 CenterZ=0 NormalX=0 NormalY=0 NormalZ=1 AngleXU=0 Radius=1.5 StartAngle=4.71239 EndAngle=7.85398
    g17: ArcOfCircle CenterX=-18.2337 CenterY=39 CenterZ=0 NormalX=0 NormalY=0 NormalZ=1 AngleXU=0 Radius=1.5 StartAngle=4.71485 EndAngle=7.85398
    g18: ArcOfCircle CenterX=-16.2837 CenterY=27.25 CenterZ=0 NormalX=0 NormalY=0 NormalZ=1 AngleXU=0 Radius=1.5 StartAngle=4.71485 EndAngle=7.85398
    g19: ArcOfCircle CenterX=-18.2337 CenterY=33 CenterZ=0 NormalX=0 NormalY=0 NormalZ=1 AngleXU=0 Radius=1.5 StartAngle=4.71485 EndAngle=7.85398
    g20: ArcOfCircle CenterX=-11.49 CenterY=21.5 CenterZ=0 NormalX=0 NormalY=0 NormalZ=1 AngleXU=0 Radius=1.5 StartAngle=4.71239 EndAngle=7.85398
    g21: ArcOfCircle CenterX=-1.5 CenterY=4.25 CenterZ=0 NormalX=0 NormalY=0 NormalZ=1 AngleXU=0 Radius=1.5 StartAngle=4.71239 EndAngle=7.85398
    g22: ArcOfCircle CenterX=-1.5 CenterY=10 CenterZ=0 NormalX=0 NormalY=0 NormalZ=1 AngleXU=0 Radius=1.5 StartAngle=4.71239 EndAngle=7.85398
    g23: ArcOfCircle CenterX=-1.5 CenterY=15.75 CenterZ=0 NormalX=0 NormalY=0 NormalZ=1 AngleXU=0 Radius=1.5 StartAngle=4.71239 EndAngle=7.85398
    g24: LineSegment StartX=-49.19 StartY=69.25 StartZ=0 EndX=-1.5 EndY=69.25 EndZ=0
    g25: LineSegment StartX=-49.19 StartY=66.25 StartZ=0 EndX=-1.5 EndY=66.25 EndZ=0
    g26: LineSegment StartX=-49.19 StartY=63.5 StartZ=0 EndX=-1.5 EndY=63.5 EndZ=0
    g27: LineSegment StartX=-49.19 StartY=60.5 StartZ=0 EndX=-1.5 EndY=60.5 EndZ=0
    g28: LineSegment StartX=-49.19 StartY=57.75 StartZ=0 EndX=-1.5 EndY=57.75 EndZ=0
    g29: LineSegment StartX=-49.19 StartY=54.75 StartZ=0 EndX=-1.5 EndY=54.75 EndZ=0
    g30: LineSegment StartX=-49.19 StartY=52 StartZ=0 EndX=-11.49 EndY=52 EndZ=0
    g31: LineSegment StartX=-49.19 StartY=49 StartZ=0 EndX=-11.49 EndY=49 EndZ=0
    g32: LineSegment StartX=-49.19 StartY=46.25 StartZ=0 EndX=-16.28 EndY=46.25 EndZ=0
    g33: LineSegment StartX=-49.19 StartY=43.25 StartZ=0 EndX=-16.28 EndY=43.25 EndZ=0
    g34: LineSegment StartX=-49.19 StartY=40.5 StartZ=0 EndX=-18.2337 EndY=40.5 EndZ=0
    g35: LineSegment StartX=-49.19 StartY=37.5 StartZ=0 EndX=-18.23 EndY=37.5 EndZ=0
    g36: LineSegment StartX=-49.19 StartY=34.5 StartZ=0 EndX=-18.2337 EndY=34.5 EndZ=0
    g37: LineSegment StartX=-49.19 StartY=31.5 StartZ=0 EndX=-18.23 EndY=31.5 EndZ=0
    g38: LineSegment StartX=-49.19 StartY=28.75 StartZ=0 EndX=-16.2837 EndY=28.75 EndZ=0
    g39: LineSegment StartX=-49.19 StartY=25.75 StartZ=0 EndX=-16.28 EndY=25.75 EndZ=0
    g40: LineSegment StartX=-49.19 StartY=23 StartZ=0 EndX=-11.49 EndY=23 EndZ=0
    g41: LineSegment StartX=-49.19 StartY=20 StartZ=0 EndX=-11.49 EndY=20 EndZ=0
    g42: LineSegment StartX=-49.19 StartY=17.25 StartZ=0 EndX=-1.5 EndY=17.25 EndZ=0
    g43: LineSegment StartX=-49.19 StartY=14.25 StartZ=0 EndX=-1.5 EndY=14.25 EndZ=0
    g44: LineSegment StartX=-49.19 StartY=11.5 StartZ=0 EndX=-1.5 EndY=11.5 EndZ=0
    g45: LineSegment StartX=-49.19 StartY=8.5 StartZ=0 EndX=-1.5 EndY=8.5 EndZ=0
    g46: LineSegment StartX=-49.19 StartY=5.75 StartZ=0 EndX=-1.5 EndY=5.75 EndZ=0
    g47: LineSegment StartX=-49.19 StartY=2.75 StartZ=0 EndX=-1.5 EndY=2.75 EndZ=0
  constraints (120):
    c: Vertical(g0)
    c: Distance(g0) = 3
    c: Block(g0)
    c: Vertical(g1)
    c: Distance(g1) = 3
    c: Vertical(g2)
    c: Equal(g0,g2) = 3
    c: Block(g2)
    c: Vertical(g3)
    c: Equal(g1,g3) = 3
    c: Vertical(g4)
    c: Equal(g0,g4) = 3
    c: Block(g4)
    c: Vertical(g5)
    c: Equal(g1,g5) = 3
    c: Vertical(g6)
    c: Equal(g0,g6) = 3
    c: Block(g6)
    c: Vertical(g7)
    c: Equal(g1,g7) = 3
    c: Vertical(g8)
    c: Equal(g0,g8) = 3
    c: Block(g8)
    c: Vertical(g9)
    c: Equal(g1,g9) = 3
    c: Vertical(g10)
    c: Equal(g0,g10) = 3
    c: Block(g10)
    c: Vertical(g11)
    c: Equal(g1,g11) = 3
    c: Block(g12)
    c: Block(g13)
    c: Block(g14)
    c: Block(g15)
    c: Block(g16)
    c: Block(g17)
    c: Block(g18)
    c: Block(g19)
    c: Block(g20)
    c: Block(g21)
    c: Block(g22)
    c: Block(g23)
    c: Block(g11)
    c: Block(g9)
    c: Block(g7)
    c: Block(g5)
    c: Block(g3)
    c: Block(g1)
    c: Coincident(g24,g0)
    c: Coincident(g24,g12)
    c: Horizontal(g24)
    c: Coincident(g25,g0)
    c: Coincident(g25,g12)
    c: Horizontal(g25)
    c: Coincident(g26,g1)
    c: Coincident(g26,g13)
    c: Horizontal(g26)
    c: Coincident(g27,g1)
    c: Coincident(g27,g13)
    c: Horizontal(g27)
    c: Coincident(g28,g2)
    c: Coincident(g28,g14)
    c: Horizontal(g28)
    c: Coincident(g29,g2)
    c: Coincident(g29,g14)
    c: Horizontal(g29)
    c: Coincident(g30,g3)
    c: Coincident(g30,g15)
    c: Horizontal(g30)
    c: Coincident(g31,g3)
    c: Coincident(g31,g15)
    c: Horizontal(g31)
    c: Coincident(g32,g4)
    c: Coincident(g32,g16)
    c: Horizontal(g32)
    c: Coincident(g33,g4)
    c: Coincident(g33,g16)
    c: Horizontal(g33)
    c: Coincident(g34,g5)
    c: Coincident(g34,g17)
    c: Horizontal(g34)
    c: Coincident(g35,g5)
    c: Coincident(g35,g17)
    c: Horizontal(g35)
    c: Coincident(g36,g6)
    c: Coincident(g36,g19)
    c: Horizontal(g36)
    c: Coincident(g37,g6)
    c: Coincident(g37,g19)
    c: Horizontal(g37)
    c: Coincident(g38,g7)
    c: Coincident(g38,g18)
    c: Horizontal(g38)
    c: Coincident(g39,g7)
    c: Coincident(g39,g18)
    c: Horizontal(g39)
    c: Coincident(g40,g8)
    c: Coincident(g40,g20)
    c: Horizontal(g40)
    c: Coincident(g41,g8)
    c: Coincident(g41,g20)
    c: Horizontal(g41)
    c: Coincident(g42,g9)
    c: Coincident(g42,g23)
    c: Horizontal(g42)
    c: Coincident(g43,g9)
    c: Coincident(g43,g23)
    c: Horizontal(g43)
    c: Coincident(g44,g10)
    c: Coincident(g44,g22)
    c: Horizontal(g44)
    c: Coincident(g45,g10)
    c: Coincident(g45,g22)
    c: Horizontal(g45)
    c: Coincident(g46,g11)
    c: Coincident(g46,g21)
    c: Horizontal(g46)
    c: Coincident(g47,g11)
    c: Coincident(g47,g21)
    c: Horizontal(g47)
FEATURE [Part::Extrusion] Extrude023
  Base = -> Sketch032
  Dir = (1,-2e-16,2e-16)
  DirMode = 2
  FaceMakerClass = Part::FaceMakerBullseye
  LengthFwd = 19
  LengthRev = 0
  Placement = pos=(-19,0,0) rot=(0,0,1;0rad)
  Solid = true
  Symmetric = false
FEATURE [Part::Fillet] Fillet023
  Base = -> Extrude023
  Edges = 24 edges r=1.49: [Edge6,Edge11,Edge18,Edge23,Edge30,Edge35,Edge42,Edge47,Edge54,Edge59,Edge66,Edge71,Edge78,Edge83,Edge90,Edge95,Edge102,Edge107,Edge114,Edge119,Edge126,Edge131,Edge138,Edge143]
  Placement = pos=(0,0.05,0) rot=(0,0,1;0rad)
FEATURE [Part::Cut] Cut014  label="bottom003"
  Base = -> Cut007
  Tool = -> Fusion047
FEATURE [Part::Cut] Cut021  label="bottom004"
  Base = -> Cut014
  Tool = -> Fillet023
FEATURE [Sketcher::SketchObject] Sketch033
  FullyConstrained = true
  Placement = pos=(117,19,0) rot=(0.57735,0.57735,0.57735;2.0944rad)
  sketch-geometry (8):
    g0: LineSegment StartX=-49.19 StartY=69.25 StartZ=0 EndX=-49.19 EndY=66.25 EndZ=0
    g1: LineSegment StartX=-49.19 StartY=5.75 StartZ=0 EndX=-49.19 EndY=2.75 EndZ=0
    g2: ArcOfCircle CenterX=-1.5 CenterY=67.75 CenterZ=0 NormalX=0 NormalY=0 NormalZ=1 AngleXU=0 Radius=1.5 StartAngle=4.71239 EndAngle=7.85398
    g3: ArcOfCircle CenterX=-1.5 CenterY=4.25 CenterZ=0 NormalX=0 NormalY=0 NormalZ=1 AngleXU=0 Radius=1.5 StartAngle=4.71239 EndAngle=7.85398
    g4: LineSegment StartX=-49.19 StartY=69.25 StartZ=0 EndX=-1.5 EndY=69.25 EndZ=0
    g5: LineSegment StartX=-49.19 StartY=66.25 StartZ=0 EndX=-1.5 EndY=66.25 EndZ=0
    g6: LineSegment StartX=-49.19 StartY=5.75 StartZ=0 EndX=-1.5 EndY=5.75 EndZ=0
    g7: LineSegment StartX=-49.19 StartY=2.75 StartZ=0 EndX=-1.5 EndY=2.75 EndZ=0
  constraints (19):
    c: Vertical(g0)
    c: Distance(g0) = 3
    c: Block(g0)
    c: Vertical(g1)
    c: Block(g2)
    c: Block(g3)
    c: Block(g1)
    c: Coincident(g4,g0)
    c: Coincident(g4,g2)
    c: Horizontal(g4)
    c: Coincident(g5,g0)
    c: Coincident(g5,g2)
    c: Horizontal(g5)
    c: Coincident(g6,g1)
    c: Coincident(g6,g3)
    c: Horizontal(g6)
    c: Coincident(g7,g1)
    c: Coincident(g7,g3)
    c: Horizontal(g7)
FEATURE [Sketcher::SketchObject] Sketch034
  FullyConstrained = true
  Placement = pos=(117,19,0) rot=(0.57735,0.57735,0.57735;2.0944rad)
  sketch-geometry (8):
    g0: LineSegment StartX=-49.19 StartY=63.5 StartZ=0 EndX=-49.19 EndY=60.5 EndZ=0
    g1: LineSegment StartX=-49.19 StartY=11.5 StartZ=0 EndX=-49.19 EndY=8.5 EndZ=0
    g2: ArcOfCircle CenterX=-1.5 CenterY=62 CenterZ=0 NormalX=0 NormalY=0 NormalZ=1 AngleXU=0 Radius=1.5 StartAngle=4.71239 EndAngle=7.85398
    g3: ArcOfCircle CenterX=-1.5 CenterY=10 CenterZ=0 NormalX=0 NormalY=0 NormalZ=1 AngleXU=0 Radius=1.5 StartAngle=4.71239 EndAngle=7.85398
    g4: LineSegment StartX=-49.19 StartY=63.5 StartZ=0 EndX=-1.5 EndY=63.5 EndZ=0
    g5: LineSegment StartX=-49.19 StartY=60.5 StartZ=0 EndX=-1.5 EndY=60.5 EndZ=0
    g6: LineSegment StartX=-49.19 StartY=11.5 StartZ=0 EndX=-1.5 EndY=11.5 EndZ=0
    g7: LineSegment StartX=-49.19 StartY=8.5 StartZ=0 EndX=-1.5 EndY=8.5 EndZ=0
  constraints (19):
    c: Vertical(g0)
    c: Distance(g0) = 3
    c: Vertical(g1)
    c: Block(g1)
    c: Block(g2)
    c: Block(g3)
    c: Block(g0)
    c: Coincident(g4,g0)
    c: Coincident(g4,g2)
    c: Horizontal(g4)
    c: Coincident(g5,g0)
    c: Coincident(g5,g2)
    c: Horizontal(g5)
    c: Coincident(g6,g1)
    c: Coincident(g6,g3)
    c: Horizontal(g6)
    c: Coincident(g7,g1)
    c: Coincident(g7,g3)
    c: Horizontal(g7)
FEATURE [Part::Extrusion] Extrude024
  Base = -> Sketch033
  Dir = (1,0,0)
  DirMode = 2
  FaceMakerClass = Part::FaceMakerBullseye
  LengthFwd = 10
  LengthRev = 0
  Solid = true
  Symmetric = false
FEATURE [Part::Extrusion] Extrude025
  Base = -> Sketch034
  Dir = (1,0,0)
  DirMode = 2
  FaceMakerClass = Part::FaceMakerBullseye
  LengthFwd = 10
  LengthRev = 0
  Solid = true
  Symmetric = false
FEATURE [Part::Fillet] Fillet024  label="removeFromtMoreFrontCaseScrewRetainers"
  Base = -> Extrude024
  Edges = 4 edges r=1.49: [Edge6,Edge11,Edge18,Edge23]
  Placement = pos=(-11,0,0) rot=(0,0,1;0rad)
FEATURE [Part::Fillet] Fillet025  label="removeFromtMoreFrontCaseScrewRetainers001"
  Base = -> Extrude025
  Edges = 4 edges r=1.49: [Edge6,Edge11,Edge18,Edge23]
  Placement = pos=(-19,0,0) rot=(0,0,1;0rad)
FEATURE [Part::Cut] Cut022
  Base = -> Cut015
  Tool = -> Fillet025
FEATURE [Part::Cut] Cut023  label="screwRetainers"
  Base = -> Cut022
  Tool = -> Fillet024
FEATURE [Part::MultiFuse] Fusion056  label="bottom005"
  Shapes = -> [Fusion044,Cut021]
FEATURE [Part::MultiFuse] Fusion057  label="casePillars001"
  Shapes = -> [Cut016,Fusion052]
FEATURE [Part::MultiFuse] Fusion058  label="bottom006"
  Shapes = -> [Fusion056,Cut023]
FEATURE [Part::MultiFuse] Fusion059  label="bottom007"
  Shapes = -> [Fusion058,Fillet005]
FEATURE [Part::MultiFuse] Fusion060  label="bottom008"
  Shapes = -> [Fusion059,Fusion]
FEATURE [Part::MultiFuse] Fusion061  label="top011"
  Shapes = -> [Cut006,Cut020]
FEATURE [Part::MultiFuse] Fusion062  label="top012"
  Shapes = -> [Fusion057,Fusion061]
FEATURE [Sketcher::SketchObject] Sketch035  label="topSketch007"
  FullyConstrained = true
  sketch-geometry (6):
    g0: LineSegment StartX=19 StartY=38 StartZ=0 EndX=117 EndY=38 EndZ=0
    g1: ArcOfCircle CenterX=19 CenterY=19 CenterZ=0 NormalX=0 NormalY=0 NormalZ=1 AngleXU=0 Radius=19 StartAngle=1.5708 EndAngle=3.14159
    g2: LineSegment StartX=117 StartY=38 StartZ=0 EndX=117 EndY=19 EndZ=0
    g3: LineSegment StartX=98 StartY=1.0161e-12 StartZ=0 EndX=5.22862e-06 EndY=1.0161e-12 EndZ=0
    g4: LineSegment StartX=5.22862e-06 StartY=19 StartZ=0 EndX=5.22862e-06 EndY=1.0161e-12 EndZ=0
    g5: ArcOfCircle CenterX=98 CenterY=19 CenterZ=0 NormalX=0 NormalY=0 NormalZ=1 AngleXU=0 Radius=19 StartAngle=4.71239 EndAngle=6.28319
  constraints (16):
    c: Horizontal(g0)
    c: Distance(g0) = 98
    c: Coincident(g1,g0)
    c: Block(g1)
    c: Coincident(g2,g0)
    c: Vertical(g2)
    c: Distance(g2) = 19
    c: Horizontal(g3)
    c: Coincident(g4,g1)
    c: Vertical(g4)
    c: Coincident(g3,g4)
    c: Block(g3)
    c: Coincident(g5,g2)
    c: Coincident(g5,g3)
    c: Block(g0)
    c: Block(g5)
FEATURE [Part::Extrusion] Extrude026  label="sideA001"
  Base = -> Sketch035
  Dir = (0,0,1)
  DirMode = 2
  FaceMakerClass = Part::FaceMakerBullseye
  LengthFwd = 3
  LengthRev = 0
  Placement = pos=(0,0,-2.7) rot=(0,0,1;0rad)
  Solid = true
  Symmetric = false
FEATURE [Sketcher::SketchObject] Sketch036  label="topSketch008"
  FullyConstrained = true
  sketch-geometry (6):
    g0: LineSegment StartX=19 StartY=38 StartZ=0 EndX=117 EndY=38 EndZ=0
    g1: ArcOfCircle CenterX=19 CenterY=19 CenterZ=0 NormalX=0 NormalY=0 NormalZ=1 AngleXU=0 Radius=19 StartAngle=1.5708 EndAngle=3.14159
    g2: LineSegment StartX=117 StartY=38 StartZ=0 EndX=117 EndY=19 EndZ=0
    g3: LineSegment StartX=98 StartY=1.0161e-12 StartZ=0 EndX=5.22862e-06 EndY=1.0161e-12 EndZ=0
    g4: LineSegment StartX=5.22862e-06 StartY=19 StartZ=0 EndX=5.22862e-06 EndY=1.0161e-12 EndZ=0
    g5: ArcOfCircle CenterX=98 CenterY=19 CenterZ=0 NormalX=0 NormalY=0 NormalZ=1 AngleXU=0 Radius=19 StartAngle=4.71239 EndAngle=6.28319
  constraints (16):
    c: Horizontal(g0)
    c: Distance(g0) = 98
    c: Coincident(g1,g0)
    c: Block(g1)
    c: Coincident(g2,g0)
    c: Vertical(g2)
    c: Distance(g2) = 19
    c: Horizontal(g3)
    c: Coincident(g4,g1)
    c: Vertical(g4)
    c: Coincident(g3,g4)
    c: Block(g3)
    c: Coincident(g5,g2)
    c: Coincident(g5,g3)
    c: Block(g0)
    c: Block(g5)
FEATURE [Part::Extrusion] Extrude027  label="sideB001"
  Base = -> Sketch036
  Dir = (0,0,1)
  DirMode = 2
  FaceMakerClass = Part::FaceMakerBullseye
  LengthFwd = 3
  LengthRev = 0
  Placement = pos=(0,0,71.7) rot=(0,0,1;0rad)
  Solid = true
  Symmetric = false
FEATURE [Part::MultiFuse] Fusion064  label="removeFromBottom"
  Shapes = -> [Extrude026,Extrude027]
FEATURE [Part::Cut] Cut024  label="bottom009"
  Base = -> Fusion060
  Tool = -> Fusion064
FEATURE [Sketcher::SketchObject] Sketch037  label="topSketch009"
  FullyConstrained = true
  sketch-geometry (6):
    g0: ArcOfCircle CenterX=19 CenterY=19 CenterZ=0 NormalX=0 NormalY=0 NormalZ=1 AngleXU=0 Radius=19 StartAngle=1.5708 EndAngle=3.14159
    g1: LineSegment StartX=5.22862e-06 StartY=19 StartZ=0 EndX=5.22862e-06 EndY=1.19904e-11 EndZ=0
    g2: LineSegment StartX=19 StartY=38 StartZ=0 EndX=124 EndY=38 EndZ=0
    g3: LineSegment StartX=5.22862e-06 StartY=1.19904e-11 StartZ=0 EndX=105 EndY=1.19904e-11 EndZ=0
    g4: ArcOfCircle CenterX=105 CenterY=19 CenterZ=0 NormalX=0 NormalY=0 NormalZ=1 AngleXU=0 Radius=19 StartAngle=4.71239 EndAngle=6.28319
    g5: LineSegment StartX=124 StartY=38 StartZ=0 EndX=124 EndY=19 EndZ=0
  constraints (16):
    c: Block(g0)
    c: Coincident(g1,g0)
    c: Vertical(g1)
    c: Horizontal(g2)
    c: Distance(g2) = 105
    c: Coincident(g2,g0)
    c: Distance(g1) = 19
    c: Coincident(g3,g1)
    c: Horizontal(g3)
    c: Distance(g3) = 105
    c: Block(g4)
    c: Coincident(g4,g3)
    c: Coincident(g5,g2)
    c: Coincident(g5,g4)
    c: Vertical(g5)
    c: Distance(g5) = 19
FEATURE [Part::Extrusion] Extrude028  label="sideB"
  Base = -> Sketch037
  Dir = (0,0,1)
  DirMode = 2
  FaceMakerClass = Part::FaceMakerBullseye
  LengthFwd = 3
  LengthRev = 0
  Placement = pos=(0,0,72) rot=(0,0,1;0rad)
  Solid = true
  Symmetric = false
FEATURE [Sketcher::SketchObject] Sketch038  label="topSketch010"
  FullyConstrained = true
  sketch-geometry (20):
    g0: LineSegment StartX=5.21097e-06 StartY=3 StartZ=0 EndX=5.21097e-06 EndY=19 EndZ=0
    g1: ArcOfCircle CenterX=19 CenterY=19 CenterZ=0 NormalX=0 NormalY=0 NormalZ=1 AngleXU=0 Radius=19 StartAngle=1.5708 EndAngle=3.14159
    g2: ArcOfCircle CenterX=19 CenterY=19 CenterZ=0 NormalX=0 NormalY=0 NormalZ=1 AngleXU=0 Radius=16 StartAngle=1.5708 EndAngle=3.14159
    g3: LineSegment StartX=114 StartY=35 StartZ=0 EndX=19 EndY=35 EndZ=0
    g4: LineSegment StartX=5.21097e-06 StartY=3 StartZ=0 EndX=5.21097e-06 EndY=0 EndZ=0
    g5: LineSegment StartX=3 StartY=0 StartZ=0 EndX=5.21097e-06 EndY=0 EndZ=0
    g6: LineSegment StartX=3 StartY=19 StartZ=0 EndX=3 EndY=0 EndZ=0
    g7: LineSegment StartX=19 StartY=38 StartZ=0 EndX=124 EndY=38 EndZ=0
    g8: Circle CenterX=119 CenterY=35 CenterZ=0 NormalX=0 NormalY=0 NormalZ=1 AngleXU=0 Radius=1
    g9: Circle CenterX=121 CenterY=35 CenterZ=0 NormalX=0 NormalY=0 NormalZ=1 AngleXU=0 Radius=1
    g10: Circle CenterX=121 CenterY=33 CenterZ=0 NormalX=0 NormalY=0 NormalZ=1 AngleXU=0 Radius=1
    g11: BSplineCurve PolesCount=3 KnotsCount=2 Degree=2 IsPeriodic=0
    g12: GeomPoint X=119 Y=35 Z=0
    g13: GeomPoint X=121 Y=33 Z=0
    g14: LineSegment StartX=119 StartY=35 StartZ=0 EndX=114 EndY=35 EndZ=0
    g15: ArcOfCircle CenterX=105 CenterY=19 CenterZ=0 NormalX=0 NormalY=0 NormalZ=1 AngleXU=0 Radius=19 StartAngle=5.7297 EndAngle=6.28319
    g16: ArcOfCircle CenterX=105 CenterY=19 CenterZ=0 NormalX=0 NormalY=0 NormalZ=1 AngleXU=0 Radius=16 StartAngle=5.60905 EndAngle=6.28319
    g17: LineSegment StartX=121 StartY=33 StartZ=0 EndX=121 EndY=19 EndZ=0
    g18: LineSegment StartX=124 StartY=38 StartZ=0 EndX=124 EndY=19 EndZ=0
    g19: LineSegment StartX=117.5 StartY=9.01251 StartZ=0 EndX=121.163 EndY=9.0125 EndZ=0
  constraints (46):
    c: Vertical(g0)
    c: Block(g0)
    c: Coincident(g1,g0)
    c: Block(g1)
    c: Coincident(g2,g1)
    c: Block(g2)
    c: Coincident(g3,g2)
    c: Horizontal(g3)
    c: Tangent(g3,g2)
    c: Coincident(g4,g0)
    c: Distance(g4) = 3
    c: Vertical(g4)
    c: Coincident(g5,g4)
    c: Horizontal(g5)
    c: Coincident(g6,g2)
    c: Coincident(g6,g5)
    c: Vertical(g6)
    c: Horizontal(g7)
    c: Distance(g7) = 105
    c: Coincident(g7,g1)
    c: Block(g3)
    c: Weight(g8) = 1
    c: Equal(g8,g9)
    c: Equal(g8,g10)
    c: InternalAlignment(g8,g11)
    c: InternalAlignment(g9,g11)
    c: InternalAlignment(g10,g11)
    c: InternalAlignment(g12,g11)
    c: InternalAlignment(g13,g11)
    c: Block(g11)
    c: Coincident(g14,g11)
    c: Coincident(g14,g3)
    c: Horizontal(g14)
    c: Block(g15)
    c: Coincident(g16,g15)
    c: Block(g16)
    c: Coincident(g17,g11)
    c: Coincident(g17,g16)
    c: Vertical(g17)
    c: Distance(g17) = 14
    c: Coincident(g18,g7)
    c: Coincident(g18,g15)
    c: Vertical(g18)
    c: Distance(g18) = 19
    c: Coincident(g19,g16)
    c: Coincident(g19,g15)
FEATURE [Part::Extrusion] Extrude029
  Base = -> Sketch038
  Dir = (0,0,1)
  DirMode = 2
  FaceMakerClass = Part::FaceMakerBullseye
  LengthFwd = 72
  LengthRev = 0
  Solid = true
  Symmetric = false
FEATURE [Part::Feature] Face085
  shape: bbox 4.8 x 25.5 x 2e-07 mm, 1 faces, 0 solids (baked)
FEATURE [Part::Revolution] Revolve089  label="moreFrontCaseScrewPost003"
  Angle = 360
  Axis = (0,1,0)
  Base = (0,0,0)
  FaceMakerClass = Part::FaceMakerBullseye
  Placement = pos=(109.5,4.5,3.5) rot=(0,0,1;0rad)
  Solid = false
  Source = -> Face085
  Symmetric = false
FEATURE [Part::Feature] Face086
  shape: bbox 4.8 x 25.5 x 2e-07 mm, 1 faces, 0 solids (baked)
FEATURE [Part::Revolution] Revolve090  label="moreFrontCaseScrewPost004"
  Angle = 360
  Axis = (0,1,0)
  Base = (0,0,0)
  FaceMakerClass = Part::FaceMakerBullseye
  Placement = pos=(109.5,4.5,68.5) rot=(0,0,1;0rad)
  Solid = false
  Source = -> Face086
  Symmetric = false
FEATURE [Part::Fillet] Fillet026  label="top013"
  Base = -> Extrude029
  Edges = 1 edges r=2: [Edge35]
FEATURE [Sketcher::SketchObject] Sketch039
  FullyConstrained = true
  sketch-geometry (7):
    g0: LineSegment StartX=0 StartY=0 StartZ=0 EndX=0 EndY=6 EndZ=0
    g1: Circle CenterX=0 CenterY=0 CenterZ=0 NormalX=0 NormalY=0 NormalZ=1 AngleXU=0 Radius=1
    g2: Circle CenterX=8 CenterY=6 CenterZ=0 NormalX=0 NormalY=0 NormalZ=1 AngleXU=0 Radius=1
    g3: BSplineCurve PolesCount=3 KnotsCount=2 Degree=2 IsPeriodic=0
    g4: GeomPoint X=0 Y=0 Z=0
    g5: GeomPoint X=8 Y=6 Z=0
    g6: LineSegment StartX=0 StartY=6 StartZ=0 EndX=8 EndY=6 EndZ=0
  constraints (14):
    c: Coincident(g0,g-1)
    c: Distance(g0) = 6
    c: Vertical(g0)
    c: Coincident(g3,g0)
    c: Weight(g1) = 1
    c: Equal(g1,g2)
    c: InternalAlignment(g1,g3)
    c: InternalAlignment(g2,g3)
    c: InternalAlignment(g4,g3)
    c: InternalAlignment(g5,g3)
    c: Block(g3)
    c: Coincident(g6,g0)
    c: Coincident(g6,g3)
    c: Horizontal(g6)
FEATURE [Sketcher::SketchObject] Sketch040
  FullyConstrained = true
  sketch-geometry (7):
    g0: LineSegment StartX=0 StartY=0 StartZ=0 EndX=0 EndY=6 EndZ=0
    g1: Circle CenterX=0 CenterY=0 CenterZ=0 NormalX=0 NormalY=0 NormalZ=1 AngleXU=0 Radius=1
    g2: Circle CenterX=8 CenterY=6 CenterZ=0 NormalX=0 NormalY=0 NormalZ=1 AngleXU=0 Radius=1
    g3: BSplineCurve PolesCount=3 KnotsCount=2 Degree=2 IsPeriodic=0
    g4: GeomPoint X=0 Y=0 Z=0
    g5: GeomPoint X=8 Y=6 Z=0
    g6: LineSegment StartX=0 StartY=6 StartZ=0 EndX=8 EndY=6 EndZ=0
  constraints (14):
    c: Coincident(g0,g-1)
    c: Distance(g0) = 6
    c: Vertical(g0)
    c: Coincident(g3,g0)
    c: Weight(g1) = 1
    c: Equal(g1,g2)
    c: InternalAlignment(g1,g3)
    c: InternalAlignment(g2,g3)
    c: InternalAlignment(g4,g3)
    c: InternalAlignment(g5,g3)
    c: Block(g3)
    c: Coincident(g6,g0)
    c: Coincident(g6,g3)
    c: Horizontal(g6)
FEATURE [Sketcher::SketchObject] Sketch041
  FullyConstrained = true
  sketch-geometry (7):
    g0: LineSegment StartX=0 StartY=0 StartZ=0 EndX=0 EndY=6 EndZ=0
    g1: Circle CenterX=0 CenterY=0 CenterZ=0 NormalX=0 NormalY=0 NormalZ=1 AngleXU=0 Radius=1
    g2: Circle CenterX=8 CenterY=6 CenterZ=0 NormalX=0 NormalY=0 NormalZ=1 AngleXU=0 Radius=1
    g3: BSplineCurve PolesCount=3 KnotsCount=2 Degree=2 IsPeriodic=0
    g4: GeomPoint X=0 Y=0 Z=0
    g5: GeomPoint X=8 Y=6 Z=0
    g6: LineSegment StartX=0 StartY=6 StartZ=0 EndX=8 EndY=6 EndZ=0
  constraints (14):
    c: Coincident(g0,g-1)
    c: Distance(g0) = 6
    c: Vertical(g0)
    c: Coincident(g3,g0)
    c: Weight(g1) = 1
    c: Equal(g1,g2)
    c: InternalAlignment(g1,g3)
    c: InternalAlignment(g2,g3)
    c: InternalAlignment(g4,g3)
    c: InternalAlignment(g5,g3)
    c: Block(g3)
    c: Coincident(g6,g0)
    c: Coincident(g6,g3)
    c: Horizontal(g6)
FEATURE [Sketcher::SketchObject] Sketch042
  FullyConstrained = true
  sketch-geometry (7):
    g0: LineSegment StartX=0 StartY=0 StartZ=0 EndX=0 EndY=6 EndZ=0
    g1: Circle CenterX=0 CenterY=0 CenterZ=0 NormalX=0 NormalY=0 NormalZ=1 AngleXU=0 Radius=1
    g2: Circle CenterX=8 CenterY=6 CenterZ=0 NormalX=0 NormalY=0 NormalZ=1 AngleXU=0 Radius=1
    g3: BSplineCurve PolesCount=3 KnotsCount=2 Degree=2 IsPeriodic=0
    g4: GeomPoint X=0 Y=0 Z=0
    g5: GeomPoint X=8 Y=6 Z=0
    g6: LineSegment StartX=0 StartY=6 StartZ=0 EndX=8 EndY=6 EndZ=0
  constraints (14):
    c: Coincident(g0,g-1)
    c: Distance(g0) = 6
    c: Vertical(g0)
    c: Coincident(g3,g0)
    c: Weight(g1) = 1
    c: Equal(g1,g2)
    c: InternalAlignment(g1,g3)
    c: InternalAlignment(g2,g3)
    c: InternalAlignment(g4,g3)
    c: InternalAlignment(g5,g3)
    c: Block(g3)
    c: Coincident(g6,g0)
    c: Coincident(g6,g3)
    c: Horizontal(g6)
FEATURE [Part::Extrusion] Extrude030  label="caseScrewPillarBracket008"
  Base = -> Sketch039
  Dir = (0,0,1)
  DirMode = 2
  FaceMakerClass = Part::FaceMakerBullseye
  LengthFwd = 2.4
  LengthRev = 0
  Placement = pos=(15.76,29,8.8) rot=(0,1,0;0rad)
  Solid = true
  Symmetric = false
FEATURE [Part::Extrusion] Extrude031  label="caseScrewPillarBracket009"
  Base = -> Sketch040
  Dir = (0,0,1)
  DirMode = 2
  FaceMakerClass = Part::FaceMakerBullseye
  LengthFwd = 2.4
  LengthRev = 0
  Placement = pos=(15.76,29,60.8) rot=(0,0,1;0rad)
  Solid = true
  Symmetric = false
FEATURE [Part::Extrusion] Extrude032  label="caseScrewPillarBracket010"
  Base = -> Sketch041
  Dir = (0,0,1)
  DirMode = 2
  FaceMakerClass = Part::FaceMakerBullseye
  LengthFwd = 2.4
  LengthRev = 0
  Placement = pos=(13.7,29,13.26) rot=(0,-1,0;1.5708rad)
  Solid = true
  Symmetric = false
FEATURE [Part::Extrusion] Extrude033  label="caseScrewPillarBracket011"
  Base = -> Sketch042
  Dir = (0,0,1)
  DirMode = 2
  FaceMakerClass = Part::FaceMakerBullseye
  LengthFwd = 2.4
  LengthRev = 0
  Placement = pos=(11.3,29,58.74) rot=(0,1,0;1.5708rad)
  Solid = true
  Symmetric = false
FEATURE [Sketcher::SketchObject] Sketch043
  FullyConstrained = true
  sketch-geometry (7):
    g0: LineSegment StartX=0 StartY=0 StartZ=0 EndX=0 EndY=6 EndZ=0
    g1: Circle CenterX=0 CenterY=0 CenterZ=0 NormalX=0 NormalY=0 NormalZ=1 AngleXU=0 Radius=1
    g2: Circle CenterX=8 CenterY=6 CenterZ=0 NormalX=0 NormalY=0 NormalZ=1 AngleXU=0 Radius=1
    g3: BSplineCurve PolesCount=3 KnotsCount=2 Degree=2 IsPeriodic=0
    g4: GeomPoint X=0 Y=0 Z=0
    g5: GeomPoint X=8 Y=6 Z=0
    g6: LineSegment StartX=0 StartY=6 StartZ=0 EndX=8 EndY=6 EndZ=0
  constraints (14):
    c: Coincident(g0,g-1)
    c: Distance(g0) = 6
    c: Vertical(g0)
    c: Coincident(g3,g0)
    c: Weight(g1) = 1
    c: Equal(g1,g2)
    c: InternalAlignment(g1,g3)
    c: InternalAlignment(g2,g3)
    c: InternalAlignment(g4,g3)
    c: InternalAlignment(g5,g3)
    c: Block(g3)
    c: Coincident(g6,g0)
    c: Coincident(g6,g3)
    c: Horizontal(g6)
FEATURE [Part::Extrusion] Extrude034  label="caseScrewPillarBracket012"
  Base = -> Sketch043
  Dir = (0,0,1)
  DirMode = 2
  FaceMakerClass = Part::FaceMakerBullseye
  LengthFwd = 2.4
  LengthRev = 0
  Placement = pos=(88.3,29,65.23) rot=(0,1,0;1.5708rad)
  Solid = true
  Symmetric = false
FEATURE [Sketcher::SketchObject] Sketch044
  FullyConstrained = true
  sketch-geometry (7):
    g0: LineSegment StartX=0 StartY=0 StartZ=0 EndX=0 EndY=6 EndZ=0
    g1: Circle CenterX=0 CenterY=0 CenterZ=0 NormalX=0 NormalY=0 NormalZ=1 AngleXU=0 Radius=1
    g2: Circle CenterX=8 CenterY=6 CenterZ=0 NormalX=0 NormalY=0 NormalZ=1 AngleXU=0 Radius=1
    g3: BSplineCurve PolesCount=3 KnotsCount=2 Degree=2 IsPeriodic=0
    g4: GeomPoint X=0 Y=0 Z=0
    g5: GeomPoint X=8 Y=6 Z=0
    g6: LineSegment StartX=0 StartY=6 StartZ=0 EndX=8 EndY=6 EndZ=0
  constraints (14):
    c: Coincident(g0,g-1)
    c: Distance(g0) = 6
    c: Vertical(g0)
    c: Coincident(g3,g0)
    c: Weight(g1) = 1
    c: Equal(g1,g2)
    c: InternalAlignment(g1,g3)
    c: InternalAlignment(g2,g3)
    c: InternalAlignment(g4,g3)
    c: InternalAlignment(g5,g3)
    c: Block(g3)
    c: Coincident(g6,g0)
    c: Coincident(g6,g3)
    c: Horizontal(g6)
FEATURE [Part::Extrusion] Extrude035  label="caseScrewPillarBracket013"
  Base = -> Sketch044
  Dir = (0,0,1)
  DirMode = 2
  FaceMakerClass = Part::FaceMakerBullseye
  LengthFwd = 2.4
  LengthRev = 0
  Placement = pos=(90.7,29,6.77) rot=(0,-1,0;1.5708rad)
  Solid = true
  Symmetric = false
FEATURE [Sketcher::SketchObject] Sketch045
  FullyConstrained = true
  sketch-geometry (7):
    g0: LineSegment StartX=0 StartY=0 StartZ=0 EndX=0 EndY=6 EndZ=0
    g1: Circle CenterX=0 CenterY=0 CenterZ=0 NormalX=0 NormalY=0 NormalZ=1 AngleXU=0 Radius=1
    g2: Circle CenterX=8 CenterY=6 CenterZ=0 NormalX=0 NormalY=0 NormalZ=1 AngleXU=0 Radius=1
    g3: BSplineCurve PolesCount=3 KnotsCount=2 Degree=2 IsPeriodic=0
    g4: GeomPoint X=0 Y=0 Z=0
    g5: GeomPoint X=8 Y=6 Z=0
    g6: LineSegment StartX=0 StartY=6 StartZ=0 EndX=8 EndY=6 EndZ=0
  constraints (14):
    c: Coincident(g0,g-1)
    c: Distance(g0) = 6
    c: Vertical(g0)
    c: Coincident(g3,g0)
    c: Weight(g1) = 1
    c: Equal(g1,g2)
    c: InternalAlignment(g1,g3)
    c: InternalAlignment(g2,g3)
    c: InternalAlignment(g4,g3)
    c: InternalAlignment(g5,g3)
    c: Block(g3)
    c: Coincident(g6,g0)
    c: Coincident(g6,g3)
    c: Horizontal(g6)
FEATURE [Sketcher::SketchObject] Sketch046
  FullyConstrained = true
  sketch-geometry (7):
    g0: LineSegment StartX=0 StartY=0 StartZ=0 EndX=0 EndY=6 EndZ=0
    g1: Circle CenterX=0 CenterY=0 CenterZ=0 NormalX=0 NormalY=0 NormalZ=1 AngleXU=0 Radius=1
    g2: Circle CenterX=8 CenterY=6 CenterZ=0 NormalX=0 NormalY=0 NormalZ=1 AngleXU=0 Radius=1
    g3: BSplineCurve PolesCount=3 KnotsCount=2 Degree=2 IsPeriodic=0
    g4: GeomPoint X=0 Y=0 Z=0
    g5: GeomPoint X=8 Y=6 Z=0
    g6: LineSegment StartX=0 StartY=6 StartZ=0 EndX=8 EndY=6 EndZ=0
  constraints (14):
    c: Coincident(g0,g-1)
    c: Distance(g0) = 6
    c: Vertical(g0)
    c: Coincident(g3,g0)
    c: Weight(g1) = 1
    c: Equal(g1,g2)
    c: InternalAlignment(g1,g3)
    c: InternalAlignment(g2,g3)
    c: InternalAlignment(g4,g3)
    c: InternalAlignment(g5,g3)
    c: Block(g3)
    c: Coincident(g6,g0)
    c: Coincident(g6,g3)
    c: Horizontal(g6)
FEATURE [Part::Extrusion] Extrude036  label="caseScrewPillarBracket014"
  Base = -> Sketch045
  Dir = (0,0,1)
  DirMode = 2
  FaceMakerClass = Part::FaceMakerBullseye
  LengthFwd = 2.4
  LengthRev = 0
  Placement = pos=(110.7,29,6.77) rot=(0,-1,0;1.5708rad)
  Solid = true
  Symmetric = false
FEATURE [Part::Extrusion] Extrude037  label="caseScrewPillarBracket015"
  Base = -> Sketch046
  Dir = (0,0,1)
  DirMode = 2
  FaceMakerClass = Part::FaceMakerBullseye
  LengthFwd = 2.4
  LengthRev = 0
  Placement = pos=(108.3,29,65.23) rot=(0,1,0;1.5708rad)
  Solid = true
  Symmetric = false
FEATURE [Part::Box] Box013  label="frontCaseScrewPillarBracket002"
  AttacherType = Attacher::AttachEngine3D
  Height = 2.4
  Length = 22
  Placement = pos=(87,28,2.3) rot=(0,0,1;0rad)
  Width = 7
FEATURE [Part::Box] Box014  label="frontCaseScrewPillarBracket003"
  AttacherType = Attacher::AttachEngine3D
  Height = 2.4
  Length = 22
  Placement = pos=(87,28,67.3) rot=(0,0,1;0rad)
  Width = 7
FEATURE [Part::Feature] Face087
  shape: bbox 4.8 x 30.2 x 2e-07 mm, 1 faces, 0 solids (baked)
FEATURE [Part::Revolution] Revolve091  label="frontCaseScrewPost004"
  Angle = 360
  Axis = (0,1,0)
  Base = (0,0,0)
  FaceMakerClass = Part::FaceMakerBullseye
  Placement = pos=(89.5,4.5,3.5) rot=(0,0,1;0rad)
  Solid = false
  Source = -> Face087
  Symmetric = false
FEATURE [Part::Feature] Face088
  shape: bbox 4.8 x 30.2 x 2e-07 mm, 1 faces, 0 solids (baked)
FEATURE [Part::Revolution] Revolve092  label="frontCaseScrewPost005"
  Angle = 360
  Axis = (0,1,0)
  Base = (0,0,0)
  FaceMakerClass = Part::FaceMakerBullseye
  Placement = pos=(89.5,4.5,68.5) rot=(0,0,1;0rad)
  Solid = false
  Source = -> Face088
  Symmetric = false
FEATURE [Part::Feature] Face089
  shape: bbox 3.5 x 30.2 x 2e-07 mm, 1 faces, 0 solids (baked)
FEATURE [Part::Revolution] Revolve093  label="backCaseScrewPost002"
  Angle = 360
  Axis = (0,1,0)
  Base = (0,0,0)
  FaceMakerClass = Part::FaceMakerBullseye
  Placement = pos=(12.5,4.5,10) rot=(0,0,1;0rad)
  Solid = false
  Source = -> Face089
  Symmetric = false
FEATURE [Part::Feature] Face090
  shape: bbox 3.5 x 30.2 x 2e-07 mm, 1 faces, 0 solids (baked)
FEATURE [Part::Revolution] Revolve094  label="backCaseScrewPost003"
  Angle = 360
  Axis = (0,1,0)
  Base = (0,0,0)
  FaceMakerClass = Part::FaceMakerBullseye
  Placement = pos=(12.5,4.5,62) rot=(0,0,1;0rad)
  Solid = false
  Source = -> Face090
  Symmetric = false
FEATURE [Part::Box] Box015  label="Cube011"
  AttacherType = Attacher::AttachEngine3D
  Height = 28.8
  Length = 3
  Placement = pos=(107.3,28,21.6) rot=(0,0,1;0rad)
  Width = 7
FEATURE [Part::Box] Box016  label="Cube012"
  AttacherType = Attacher::AttachEngine3D
  Height = 3
  Length = 7.4
  Placement = pos=(107.3,28,18.6) rot=(0,0,1;0rad)
  Width = 7
FEATURE [Part::Box] Box017  label="Cube013"
  AttacherType = Attacher::AttachEngine3D
  Height = 3
  Length = 7.4
  Placement = pos=(107.3,28,50.4) rot=(0,0,1;0rad)
  Width = 7
FEATURE [Part::Cylinder] Cylinder024
  Angle = 360
  AttacherType = Attacher::AttachEngine3D
  Height = 20
  Placement = pos=(0,0,36.15) rot=(0,0,1;0rad)
  Radius = 14.3
FEATURE [Part::Cylinder] Cylinder025
  Angle = 360
  AttacherType = Attacher::AttachEngine3D
  Height = 10
  Placement = pos=(0,0,36.15) rot=(0,0,1;0rad)
  Radius = 4
FEATURE [Part::MultiFuse] Fusion066  label="removeToCreteHoleForPlugHousing009"
  Placement = pos=(70,19,36) rot=(0,1,0;1.5708rad)
  Shapes = -> [Cylinder024,Cylinder025]
FEATURE [Part::MultiFuse] Fusion065  label="plugHousingBracketHolder002"
  Shapes = -> [Box017,Box015,Box016]
FEATURE [Part::Cut] Cut025  label="plugHousingBracketHolder003"
  Base = -> Fusion065
  Placement = pos=(7,0,0) rot=(0,0,1;0rad)
  Tool = -> Fusion066
FEATURE [Sketcher::SketchObject] Sketch047
  FullyConstrained = false
  Placement = pos=(0,0,0) rot=(1,0,0;1.5708rad)
  sketch-geometry (24):
    g0: ArcOfCircle CenterX=-4 CenterY=-10.5 CenterZ=0 NormalX=0 NormalY=0 NormalZ=1 AngleXU=0 Radius=1.5 StartAngle=6e-16 EndAngle=3.14159
    g1: ArcOfCircle CenterX=-34.2 CenterY=-10.5 CenterZ=0 NormalX=0 NormalY=0 NormalZ=1 AngleXU=0 Radius=1.5 StartAngle=0 EndAngle=3.14159
    g2: ArcOfCircle CenterX=-34.2 CenterY=-27.7 CenterZ=0 NormalX=0 NormalY=0 NormalZ=1 AngleXU=0 Radius=1.5 StartAngle=3.14159 EndAngle=6.28319
    g3: ArcOfCircle CenterX=-4 CenterY=-27.7 CenterZ=0 NormalX=0 NormalY=0 NormalZ=1 AngleXU=0 Radius=1.5 StartAngle=3.1416 EndAngle=6.28319
    g4: ArcOfCircle CenterX=-10 CenterY=-4.3 CenterZ=0 NormalX=0 NormalY=0 NormalZ=1 AngleXU=0 Radius=1.5 StartAngle=2e-16 EndAngle=3.14159
    g5: ArcOfCircle CenterX=-16.1 CenterY=-1.8 CenterZ=0 NormalX=0 NormalY=0 NormalZ=1 AngleXU=0 Radius=1.5 StartAngle=5e-16 EndAngle=3.14159
    g6: ArcOfCircle CenterX=-22.1 CenterY=-1.8 CenterZ=0 NormalX=0 NormalY=0 NormalZ=1 AngleXU=0 Radius=1.5 StartAngle=5e-16 EndAngle=3.14159
    g7: ArcOfCircle CenterX=-28.2 CenterY=-4.3 CenterZ=0 NormalX=0 NormalY=0 NormalZ=1 AngleXU=0 Radius=1.5 StartAngle=2e-16 EndAngle=3.14159
    g8: ArcOfCircle CenterX=-10 CenterY=-33.9 CenterZ=0 NormalX=0 NormalY=0 NormalZ=1 AngleXU=0 Radius=1.5 StartAngle=3.14159 EndAngle=6.28319
    g9: ArcOfCircle CenterX=-16.1 CenterY=-36.4 CenterZ=0 NormalX=0 NormalY=0 NormalZ=1 AngleXU=0 Radius=1.5 StartAngle=3.14159 EndAngle=6.28319
    g10: ArcOfCircle CenterX=-22.1 CenterY=-36.4 CenterZ=0 NormalX=0 NormalY=0 NormalZ=1 AngleXU=0 Radius=1.5 StartAngle=3.14159 EndAngle=6.28319
    g11: ArcOfCircle CenterX=-28.2 CenterY=-33.9 CenterZ=0 NormalX=0 NormalY=0 NormalZ=1 AngleXU=0 Radius=1.5 StartAngle=3.14159 EndAngle=6.28319
    g12: LineSegment StartX=-35.7 StartY=-10.5 StartZ=0 EndX=-35.7 EndY=-27.7 EndZ=0
    g13: LineSegment StartX=-32.7 StartY=-10.5 StartZ=0 EndX=-32.7 EndY=-27.7 EndZ=0
    g14: LineSegment StartX=-29.7 StartY=-33.9 StartZ=0 EndX=-29.7 EndY=-4.3 EndZ=0
    g15: LineSegment StartX=-26.7 StartY=-33.9 StartZ=0 EndX=-26.7 EndY=-4.3 EndZ=0
    g16: LineSegment StartX=-2.5 StartY=-10.5 StartZ=0 EndX=-2.5 EndY=-27.7 EndZ=0
    g17: LineSegment StartX=-8.5 StartY=-4.3 StartZ=0 EndX=-8.5 EndY=-33.9 EndZ=0
    g18: LineSegment StartX=-5.5 StartY=-10.5 StartZ=0 EndX=-5.5 EndY=-27.7 EndZ=0
    g19: LineSegment StartX=-11.5 StartY=-4.3 StartZ=0 EndX=-11.5 EndY=-33.9 EndZ=0
    g20: LineSegment StartX=-14.6 StartY=-1.8 StartZ=0 EndX=-14.6 EndY=-36.4 EndZ=0
    g21: LineSegment StartX=-17.6 StartY=-1.8 StartZ=0 EndX=-17.6 EndY=-36.4 EndZ=0
    g22: LineSegment StartX=-20.6 StartY=-36.4 StartZ=0 EndX=-20.6 EndY=-1.8 EndZ=0
    g23: LineSegment StartX=-23.6 StartY=-1.8 StartZ=0 EndX=-23.6 EndY=-36.4 EndZ=0
  constraints (48):
    c: Block(g0)
    c: Block(g1)
    c: Block(g2)
    c: Block(g3)
    c: Block(g4)
    c: Block(g5)
    c: Block(g6)
    c: Block(g7)
    c: Block(g8)
    c: Block(g9)
    c: Block(g10)
    c: Block(g11)
    c: Coincident(g12,g1)
    c: Coincident(g12,g2)
    c: Vertical(g12)
    c: Coincident(g13,g1)
    c: Coincident(g13,g2)
    c: Vertical(g13)
    c: Coincident(g14,g11)
    c: Coincident(g14,g7)
    c: Vertical(g14)
    c: Coincident(g15,g11)
    c: Coincident(g15,g7)
    c: Vertical(g15)
    c: Coincident(g16,g0)
    c: Coincident(g16,g3)
    c: Vertical(g16)
    c: Coincident(g17,g4)
    c: Coincident(g17,g8)
    c: Vertical(g17)
    c: Coincident(g18,g0)
    c: Coincident(g18,g3)
    c: Vertical(g18)
    c: Coincident(g19,g4)
    c: Coincident(g19,g8)
    c: Vertical(g19)
    c: Coincident(g20,g5)
    c: Coincident(g20,g9)
    c: Vertical(g20)
    c: Coincident(g21,g5)
    c: Coincident(g21,g9)
    c: Vertical(g21)
    c: Coincident(g22,g10)
    c: Coincident(g22,g6)
    c: Vertical(g22)
    c: Coincident(g23,g6)
    c: Coincident(g23,g10)
    c: Vertical(g23)
FEATURE [Part::Extrusion] Extrude038  label="removeToCreateFanGrillHoles001"
  Base = -> Sketch047
  Dir = (0,-1,6e-16)
  DirMode = 2
  FaceMakerClass = Part::FaceMakerBullseye
  LengthFwd = 10
  LengthRev = 0
  Placement = pos=(65.4,44,54.82) rot=(0,0,1;0rad)
  Solid = true
  Symmetric = false
FEATURE [Part::Feature] Wire004
  shape: bbox 11 x 5.2 x 2e-07 mm, 0 faces, 0 solids (baked)
FEATURE [Part::Revolution] Revolve095
  Angle = 360
  Axis = (0,1,0)
  Base = (0,0,0)
  FaceMakerClass = Part::FaceMakerBullseye
  Placement = pos=(30.3,38,19.7) rot=(0,0,1;0rad)
  Solid = true
  Source = -> Wire004
  Symmetric = false
FEATURE [Part::Feature] Wire005
  shape: bbox 11 x 5.2 x 2e-07 mm, 0 faces, 0 solids (baked)
FEATURE [Part::Revolution] Revolve096
  Angle = 360
  Axis = (0,1,0)
  Base = (0,0,0)
  FaceMakerClass = Part::FaceMakerBullseye
  Placement = pos=(30.3,38,51.7) rot=(0,0,1;0rad)
  Solid = true
  Source = -> Wire005
  Symmetric = false
FEATURE [Part::Feature] Wire006
  shape: bbox 11 x 5.2 x 2e-07 mm, 0 faces, 0 solids (baked)
FEATURE [Part::Revolution] Revolve097
  Angle = 360
  Axis = (0,1,0)
  Base = (0,0,0)
  FaceMakerClass = Part::FaceMakerBullseye
  Placement = pos=(62.3,38,51.7) rot=(0,0,1;0rad)
  Solid = true
  Source = -> Wire006
  Symmetric = false
FEATURE [Part::Feature] Wire007
  shape: bbox 11 x 5.2 x 2e-07 mm, 0 faces, 0 solids (baked)
FEATURE [Part::Revolution] Revolve098
  Angle = 360
  Axis = (0,1,0)
  Base = (0,0,0)
  FaceMakerClass = Part::FaceMakerBullseye
  Placement = pos=(62.3,38,19.7) rot=(0,0,1;0rad)
  Solid = true
  Source = -> Wire007
  Symmetric = false
FEATURE [Part::MultiFuse] Fusion067  label="fanScrewHousing002"
  Shapes = -> [Revolve098,Revolve097,Revolve096,Revolve095]
FEATURE [Part::Feature] Face091 .. Face094  x4 (patterned run collapsed; names and placements below)
  shape: bbox 3.5 x 17.8 x 2e-07 mm, 1 faces, 0 solids (baked)
FEATURE [Part::Revolution] Revolve099  label="removeToCreateScrewAndThreadedInsertHole026"
  Angle = 360
  Axis = (0,1,0)
  Base = (0,0,0)
  FaceMakerClass = Part::FaceMakerBullseye
  Placement = pos=(62.3,30.3,19.7) rot=(0,0,1;0rad)
  Solid = false
  Source = -> Face091
  Symmetric = false
FEATURE [Part::Revolution] Revolve100  label="removeToCreateScrewAndThreadedInsertHole027"
  Angle = 360
  Axis = (0,1,0)
  Base = (0,0,0)
  FaceMakerClass = Part::FaceMakerBullseye
  Placement = pos=(62.3,30.3,51.7) rot=(0,0,1;0rad)
  Solid = false
  Source = -> Face092
  Symmetric = false
FEATURE [Part::Revolution] Revolve101  label="removeToCreateScrewAndThreadedInsertHole028"
  Angle = 360
  Axis = (0,1,0)
  Base = (0,0,0)
  FaceMakerClass = Part::FaceMakerBullseye
  Placement = pos=(30.3,30.3,19.7) rot=(0,0,1;0rad)
  Solid = false
  Source = -> Face093
  Symmetric = false
FEATURE [Part::Revolution] Revolve102  label="removeToCreateScrewAndThreadedInsertHole029"
  Angle = 360
  Axis = (0,1,0)
  Base = (0,0,0)
  FaceMakerClass = Part::FaceMakerBullseye
  Placement = pos=(30.3,30.3,51.7) rot=(0,0,1;0rad)
  Solid = false
  Source = -> Face094
  Symmetric = false
FEATURE [Part::MultiFuse] Fusion068  label="createThreadedInsertHolesForFan002"
  Shapes = -> [Revolve099,Revolve100,Revolve101,Revolve102]
FEATURE [Part::Cut] Cut026  label="fanScrewHousing003"
  Base = -> Fusion067
  Tool = -> Fusion068
FEATURE [Sketcher::SketchObject] Sketch048
  FullyConstrained = false
  Placement = pos=(0,0,0) rot=(1,0,0;1.5708rad)
  sketch-geometry (24):
    g0: ArcOfCircle CenterX=-4 CenterY=-10.5 CenterZ=0 NormalX=0 NormalY=0 NormalZ=1 AngleXU=0 Radius=1.5 StartAngle=6e-16 EndAngle=3.14159
    g1: ArcOfCircle CenterX=-34.2 CenterY=-10.5 CenterZ=0 NormalX=0 NormalY=0 NormalZ=1 AngleXU=0 Radius=1.5 StartAngle=0 EndAngle=3.14159
    g2: ArcOfCircle CenterX=-34.2 CenterY=-27.7 CenterZ=0 NormalX=0 NormalY=0 NormalZ=1 AngleXU=0 Radius=1.5 StartAngle=3.14159 EndAngle=6.28319
    g3: ArcOfCircle CenterX=-4 CenterY=-27.7 CenterZ=0 NormalX=0 NormalY=0 NormalZ=1 AngleXU=0 Radius=1.5 StartAngle=3.1416 EndAngle=6.28319
    g4: ArcOfCircle CenterX=-10 CenterY=-4.3 CenterZ=0 NormalX=0 NormalY=0 NormalZ=1 AngleXU=0 Radius=1.5 StartAngle=2e-16 EndAngle=3.14159
    g5: ArcOfCircle CenterX=-16.1 CenterY=-1.8 CenterZ=0 NormalX=0 NormalY=0 NormalZ=1 AngleXU=0 Radius=1.5 StartAngle=5e-16 EndAngle=3.14159
    g6: ArcOfCircle CenterX=-22.1 CenterY=-1.8 CenterZ=0 NormalX=0 NormalY=0 NormalZ=1 AngleXU=0 Radius=1.5 StartAngle=5e-16 EndAngle=3.14159
    g7: ArcOfCircle CenterX=-28.2 CenterY=-4.3 CenterZ=0 NormalX=0 NormalY=0 NormalZ=1 AngleXU=0 Radius=1.5 StartAngle=2e-16 EndAngle=3.14159
    g8: ArcOfCircle CenterX=-10 CenterY=-33.9 CenterZ=0 NormalX=0 NormalY=0 NormalZ=1 AngleXU=0 Radius=1.5 StartAngle=3.14159 EndAngle=6.28319
    g9: ArcOfCircle CenterX=-16.1 CenterY=-36.4 CenterZ=0 NormalX=0 NormalY=0 NormalZ=1 AngleXU=0 Radius=1.5 StartAngle=3.14159 EndAngle=6.28319
    g10: ArcOfCircle CenterX=-22.1 CenterY=-36.4 CenterZ=0 NormalX=0 NormalY=0 NormalZ=1 AngleXU=0 Radius=1.5 StartAngle=3.14159 EndAngle=6.28319
    g11: ArcOfCircle CenterX=-28.2 CenterY=-33.9 CenterZ=0 NormalX=0 NormalY=0 NormalZ=1 AngleXU=0 Radius=1.5 StartAngle=3.14159 EndAngle=6.28319
    g12: LineSegment StartX=-35.7 StartY=-10.5 StartZ=0 EndX=-35.7 EndY=-27.7 EndZ=0
    g13: LineSegment StartX=-32.7 StartY=-10.5 StartZ=0 EndX=-32.7 EndY=-27.7 EndZ=0
    g14: LineSegment StartX=-29.7 StartY=-33.9 StartZ=0 EndX=-29.7 EndY=-4.3 EndZ=0
    g15: LineSegment StartX=-26.7 StartY=-33.9 StartZ=0 EndX=-26.7 EndY=-4.3 EndZ=0
    g16: LineSegment StartX=-2.5 StartY=-10.5 StartZ=0 EndX=-2.5 EndY=-27.7 EndZ=0
    g17: LineSegment StartX=-8.5 StartY=-4.3 StartZ=0 EndX=-8.5 EndY=-33.9 EndZ=0
    g18: LineSegment StartX=-5.5 StartY=-10.5 StartZ=0 EndX=-5.5 EndY=-27.7 EndZ=0
    g19: LineSegment StartX=-11.5 StartY=-4.3 StartZ=0 EndX=-11.5 EndY=-33.9 EndZ=0
    g20: LineSegment StartX=-14.6 StartY=-1.8 StartZ=0 EndX=-14.6 EndY=-36.4 EndZ=0
    g21: LineSegment StartX=-17.6 StartY=-1.8 StartZ=0 EndX=-17.6 EndY=-36.4 EndZ=0
    g22: LineSegment StartX=-20.6 StartY=-36.4 StartZ=0 EndX=-20.6 EndY=-1.8 EndZ=0
    g23: LineSegment StartX=-23.6 StartY=-1.8 StartZ=0 EndX=-23.6 EndY=-36.4 EndZ=0
  constraints (48):
    c: Block(g0)
    c: Block(g1)
    c: Block(g2)
    c: Block(g3)
    c: Block(g4)
    c: Block(g5)
    c: Block(g6)
    c: Block(g7)
    c: Block(g8)
    c: Block(g9)
    c: Block(g10)
    c: Block(g11)
    c: Coincident(g12,g1)
    c: Coincident(g12,g2)
    c: Vertical(g12)
    c: Coincident(g13,g1)
    c: Coincident(g13,g2)
    c: Vertical(g13)
    c: Coincident(g14,g11)
    c: Coincident(g14,g7)
    c: Vertical(g14)
    c: Coincident(g15,g11)
    c: Coincident(g15,g7)
    c: Vertical(g15)
    c: Coincident(g16,g0)
    c: Coincident(g16,g3)
    c: Vertical(g16)
    c: Coincident(g17,g4)
    c: Coincident(g17,g8)
    c: Vertical(g17)
    c: Coincident(g18,g0)
    c: Coincident(g18,g3)
    c: Vertical(g18)
    c: Coincident(g19,g4)
    c: Coincident(g19,g8)
    c: Vertical(g19)
    c: Coincident(g20,g5)
    c: Coincident(g20,g9)
    c: Vertical(g20)
    c: Coincident(g21,g5)
    c: Coincident(g21,g9)
    c: Vertical(g21)
    c: Coincident(g22,g10)
    c: Coincident(g22,g6)
    c: Vertical(g22)
    c: Coincident(g23,g6)
    c: Coincident(g23,g10)
    c: Vertical(g23)
FEATURE [Part::Extrusion] Extrude039  label="removeToCreateFanGrillHoles002"
  Base = -> Sketch048
  Dir = (0,-1,6e-16)
  DirMode = 2
  FaceMakerClass = Part::FaceMakerBullseye
  LengthFwd = 10
  LengthRev = 0
  Placement = pos=(65.4,44,54.82) rot=(0,0,1;0rad)
  Solid = true
  Symmetric = false
FEATURE [Part::Cut] Cut027  label="fanScrewHousing004"
  Base = -> Cut026
  Tool = -> Extrude038
FEATURE [Part::Cut] Cut028  label="top014"
  Base = -> Fillet026
  Tool = -> Extrude039
